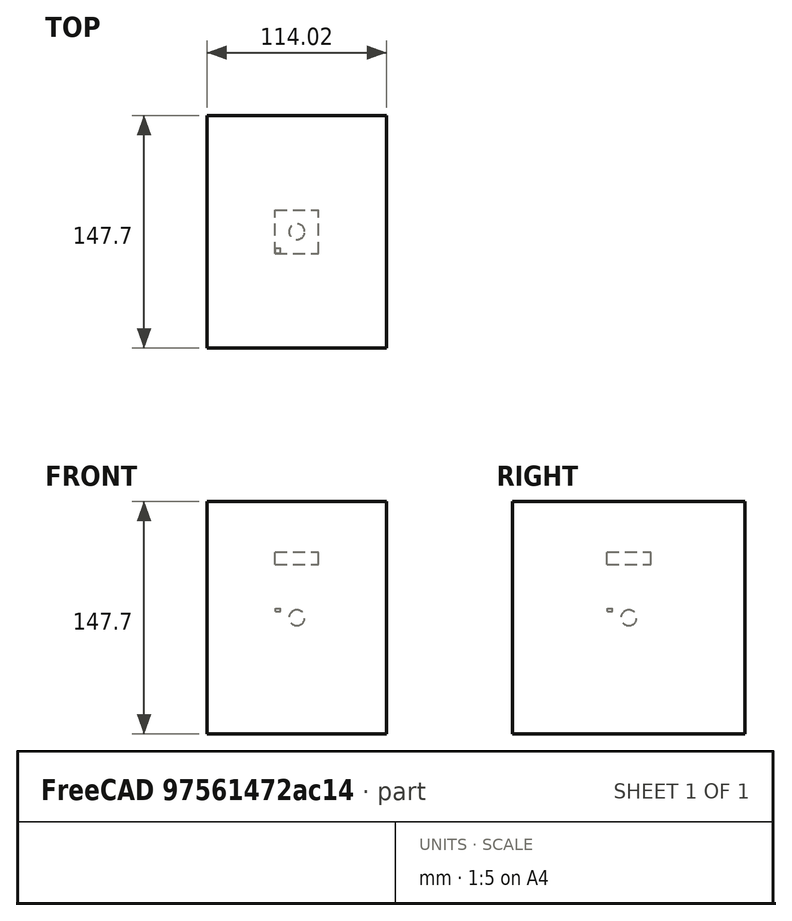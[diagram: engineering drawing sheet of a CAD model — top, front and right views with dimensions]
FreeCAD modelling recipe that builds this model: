
FCSTD DOCUMENT  (FreeCAD 1.0R39109 (Git))
Label: NewBS-NoArray-borderTest-1
License: All rights reserved
objects: App::DocumentObjectGroupPython×1272, App::Link×77, App::Part×7, Part::FeaturePython×4, App::FeaturePython×1
note: 4 computed .brp shape members not serialized (recipe doc carries the construction recipe); baked Part::Feature solids carry a one-line shape summary decoded from their .brp

FEATURE [App::DocumentObjectGroupPython] HALFPI  # scripted group (container) (typed FeaturePython)
  name = HALFPI
  value = pi/2.
FEATURE [App::DocumentObjectGroupPython] PI  # scripted group (container) (typed FeaturePython)
  name = PI
  value = 1.*pi
FEATURE [App::DocumentObjectGroupPython] TWOPI  # scripted group (container) (typed FeaturePython)
  name = TWOPI
  value = 2.*pi
FEATURE [App::DocumentObjectGroupPython] Constants  # scripted group (container) (typed FeaturePython)
  Group = -> [HALFPI,PI,TWOPI]
FEATURE [App::DocumentObjectGroupPython] Variables  # scripted group (container) (typed FeaturePython)
FEATURE [App::DocumentObjectGroupPython] Quantities  # scripted group (container) (typed FeaturePython)
FEATURE [App::DocumentObjectGroupPython] Isotopes  # scripted group (container) (typed FeaturePython)
FEATURE [App::DocumentObjectGroupPython] Elements  # scripted group (container) (typed FeaturePython)
FEATURE [App::DocumentObjectGroupPython] G4_AIR  label="G4_AIR : 1.000"  # scripted group (container) (typed FeaturePython)
  n = 1
FEATURE [App::DocumentObjectGroupPython] Air  # scripted group (container) (typed FeaturePython)
  Dunit = mg/cm3
  Dvalue = 1.29
  Group = -> [G4_AIR]
  RINDEX = AirRINDEX
  conduct = 2
  density = 1
  expand = 3
  name = Air
  specific = 4
FEATURE [App::DocumentObjectGroupPython] SY  # scripted group (container) (typed FeaturePython)
  coldim = 1
  values = 100000/MeV
FEATURE [App::DocumentObjectGroupPython] RS  # scripted group (container) (typed FeaturePython)
  coldim = 1
  values = 1
FEATURE [App::DocumentObjectGroupPython] FTC  # scripted group (container) (typed FeaturePython)
  coldim = 1
  values = 21.5*ns
FEATURE [App::DocumentObjectGroupPython] STC  # scripted group (container) (typed FeaturePython)
  coldim = 1
  values = 43.8*ns
FEATURE [App::DocumentObjectGroupPython] RY1  # scripted group (container) (typed FeaturePython)
  coldim = 1
  values = 95
FEATURE [App::DocumentObjectGroupPython] RY2  # scripted group (container) (typed FeaturePython)
  coldim = 1
  values = 5
FEATURE [App::DocumentObjectGroupPython] YR  # scripted group (container) (typed FeaturePython)
  coldim = 1
  values = 0.8
FEATURE [App::DocumentObjectGroupPython] SCINTLAR  # scripted group (container) (typed FeaturePython)
  coldim = 2
  values = <blob: 2358 chars omitted>
FEATURE [App::DocumentObjectGroupPython] RINDEXLAR  # scripted group (container) (typed FeaturePython)
  coldim = 2
  values = <blob: 9384 chars omitted>
FEATURE [App::DocumentObjectGroupPython] ABSLENGTHLAR  # scripted group (container) (typed FeaturePython)
  coldim = 2
  values = 7.74901*eV 10.0*m 7.77525*eV 10.0*m 7.80167*eV 10.0*m 7.82827*eV 10.0*m 7.85506*eV 10.0*m 7.88202*eV 10.0*m 7.90917*eV 10.0*m 7.93651*eV 10.0*m 7.96404*eV 10.0*m 7.99176*eV 10.0*m 8.01968*eV 10.0*m 8.04779*eV 10.0*m 8.07609*eV 10.0*m 8.1046*eV 10.0*m 8.13331*eV 10.0*m 8.16222*eV 10.0*m 8.19134*eV 10.0*m 8.22067*eV 10.0*m 8.25021*eV 10.0*m 8.27996*eV 10.0*m 8.30993*eV 10.0*m 8.34012*eV 10.0*m 8.37052*eV 10.0*m 8.40115*eV 10.0*m 8.432*eV 10.0*m 8.46308*eV 10.0*m 8.4944*eV 10.0*m 8.52594*eV 10.0*m 8.55772*eV 10.0*m 8.58973*eV 10.0*m 8.62199*eV 10.0*m 8.65449*eV 10.0*m 8.68723*eV 10.0*m 8.72023*eV 10.0*m 8.75347*eV 10.0*m 8.78697*eV 10.0*m 8.82073*eV 10.0*m 8.85475*eV 10.0*m 8.88903*eV 10.0*m 8.92358*eV 10.0*m 8.9584*eV 10.0*m 8.99349*eV 10.0*m 9.02885*eV 10.0*m 9.0645*eV 10.0*m 9.10043*eV 10.0*m 9.13664*eV 10.0*m 9.17314*eV 10.0*m 9.20994*eV 10.0*m 9.24703*eV 10.0*m 9.28442*eV 10.0*m 9.32212*eV 10.0*m 9.36012*eV 10.0*m 9.39844*eV 10.0*m 9.43707*eV 10.0*m 9.47602*eV 10.0*m 9.51529*eV 10.0*m 9.55489*eV 10.0*m 9.59481*eV 10.0*m 9.63508*eV 10.0*m 9.67568*eV 10.0*m 9.71663*eV 10.0*m 9.75792*eV 10.0*m 9.79957*eV 10.0*m 9.84158*eV 10.0*m 9.88394*eV 10.0*m 9.92668*eV 10.0*m 9.96978*eV 10.0*m 10.0133*eV 10.0*m 10.0571*eV 10.0*m 10.1014*eV 10.0*m 10.146*eV 10.0*m 10.191*eV 10.0*m 10.2365*eV 10.0*m 10.2823*eV 10.0*m 10.3286*eV 10.0*m 10.3752*eV 10.0*m 10.4223*eV 10.0*m 10.4699*eV 10.0*m 10.5178*eV 10.0*m 10.5662*eV 10.0*m 10.6151*eV 10.0*m 10.6644*eV 10.0*m 10.7142*eV 10.0*m 10.7644*eV 10.0*m 10.8151*eV 10.0*m 10.8663*eV 10.0*m 10.9179*eV 10.0*m 10.9701*eV 10.0*m 11.0228*eV 10.0*m 11.076*eV 10.0*m 11.1296*eV 10.0*m 11.1839*eV 10.0*m 11.2386*eV 10.0*m 11.2939*eV 10.0*m 11.3497*eV 10.0*m 11.4061*eV 10.0*m 11.463*eV 10.0*m 11.5206*eV 10.0*m 11.5787*eV 10.0*m 11.6373*eV 10.0*m
FEATURE [App::DocumentObjectGroupPython] RAYLEIGHLAR  # scripted group (container) (typed FeaturePython)
  coldim = 2
  values = 7.74901*eV 90.0*cm 7.77525*eV 90.0*cm 7.80167*eV 90.0*cm 7.82827*eV 90.0*cm 7.85506*eV 90.0*cm 7.88202*eV 90.0*cm 7.90917*eV 90.0*cm 7.93651*eV 90.0*cm 7.96404*eV 90.0*cm 7.99176*eV 90.0*cm 8.01968*eV 90.0*cm 8.04779*eV 90.0*cm 8.07609*eV 90.0*cm 8.1046*eV 90.0*cm 8.13331*eV 90.0*cm 8.16222*eV 90.0*cm 8.19134*eV 90.0*cm 8.22067*eV 90.0*cm 8.25021*eV 90.0*cm 8.27996*eV 90.0*cm 8.30993*eV 90.0*cm 8.34012*eV 90.0*cm 8.37052*eV 90.0*cm 8.40115*eV 90.0*cm 8.432*eV 90.0*cm 8.46308*eV 90.0*cm 8.4944*eV 90.0*cm 8.52594*eV 90.0*cm 8.55772*eV 90.0*cm 8.58973*eV 90.0*cm 8.62199*eV 90.0*cm 8.65449*eV 90.0*cm 8.68723*eV 90.0*cm 8.72023*eV 90.0*cm 8.75347*eV 90.0*cm 8.78697*eV 90.0*cm 8.82073*eV 90.0*cm 8.85475*eV 90.0*cm 8.88903*eV 90.0*cm 8.92358*eV 90.0*cm 8.9584*eV 90.0*cm 8.99349*eV 90.0*cm 9.02885*eV 90.0*cm 9.0645*eV 90.0*cm 9.10043*eV 90.0*cm 9.13664*eV 90.0*cm 9.17314*eV 90.0*cm 9.20994*eV 90.0*cm 9.24703*eV 90.0*cm 9.28442*eV 90.0*cm 9.32212*eV 90.0*cm 9.36012*eV 90.0*cm 9.39844*eV 90.0*cm 9.43707*eV 90.0*cm 9.47602*eV 90.0*cm 9.51529*eV 90.0*cm 9.55489*eV 90.0*cm 9.59481*eV 90.0*cm 9.63508*eV 90.0*cm 9.67568*eV 90.0*cm 9.71663*eV 90.0*cm 9.75792*eV 90.0*cm 9.79957*eV 90.0*cm 9.84158*eV 90.0*cm 9.88394*eV 90.0*cm 9.92668*eV 90.0*cm 9.96978*eV 90.0*cm 10.0133*eV 90.0*cm 10.0571*eV 90.0*cm 10.1014*eV 90.0*cm 10.146*eV 90.0*cm 10.191*eV 90.0*cm 10.2365*eV 90.0*cm 10.2823*eV 90.0*cm 10.3286*eV 90.0*cm 10.3752*eV 90.0*cm 10.4223*eV 90.0*cm 10.4699*eV 90.0*cm 10.5178*eV 90.0*cm 10.5662*eV 90.0*cm 10.6151*eV 90.0*cm 10.6644*eV 90.0*cm 10.7142*eV 90.0*cm 10.7644*eV 90.0*cm 10.8151*eV 90.0*cm 10.8663*eV 90.0*cm 10.9179*eV 90.0*cm 10.9701*eV 90.0*cm 11.0228*eV 90.0*cm 11.076*eV 90.0*cm 11.1296*eV 90.0*cm 11.1839*eV 90.0*cm 11.2386*eV 90.0*cm 11.2939*eV 90.0*cm 11.3497*eV 90.0*cm 11.4061*eV 90.0*cm 11.463*eV 90.0*cm 11.5206*eV 90.0*cm 11.5787*eV 90.0*cm 11.6373*eV 90.0*cm
FEATURE [App::DocumentObjectGroupPython] REFLECTIVITY  # scripted group (container) (typed FeaturePython)
  coldim = 2
  values = 2.034*eV 0.98 2.068*eV 0.98 2.103*eV 0.98 2.139*eV 0.98 2.177*eV 0.98 2.216*eV 0.98 2.256*eV 0.98 2.298*eV 0.98 2.341*eV 0.98 2.386*eV 0.98 2.433*eV 0.98 2.481*eV 0.98 2.532*eV 0.98 2.585*eV 0.98 2.64*eV 0.98 2.697*eV 0.98 2.757*eV 0.98 2.82*eV 0.98 2.885*eV 0.98 2.954*eV 0.98 3.026*eV 0.98 3.102*eV 0.98 3.181*eV 0.98 3.265*eV 0.98 3.353*eV 0.98 3.446*eV 0.98 3.545*eV 0.98 3.649*eV 0.98 3.76*eV 0.98 3.877*eV 0.98 4.002*eV 0.98 4.136*eV 0.98 5.0*eV 0.98 6.0*eV 0.98 7.0*eV 0.98 8.0*eV 0.98 9.0*eV 0.98 9.0*eV 0.98 10.0*eV 0.98 11.0*eV 0.98 11.6*eV 0.98
FEATURE [App::DocumentObjectGroupPython] EFFICIENCY  # scripted group (container) (typed FeaturePython)
  coldim = 2
  values = 2.034*eV 1 2.068*eV 1 2.103*eV 1 2.139*eV 1 2.177*eV 1 2.216*eV 1 2.256*eV 1 2.298*eV 1 2.341*eV 1 2.386*eV 1 2.433*eV 1 2.481*eV 1 2.532*eV 1 2.585*eV 1 2.64*eV 1 2.697*eV 1 2.757*eV 1 2.82*eV 1 2.885*eV 1 2.954*eV 1 3.026*eV 1 3.102*eV 1 3.181*eV  1 3.265*eV 1 3.353*eV 1 3.446*eV 1 3.545*eV 1 3.649*eV 1 3.76*eV 1 3.877*eV 1 4.002*eV 1 4.136*eV 1 5.0*eV 1 6.0*eV 1 7.0*eV 1 8.0*eV 1 9.0*eV 1 9.0*eV 1 10.0*eV 1 11.0*eV 1 11.6*eV 1
FEATURE [App::DocumentObjectGroupPython] AirRINDEX  # scripted group (container) (typed FeaturePython)
  coldim = 2
  values = 2.034*eV 1 2.068*eV 1 2.103*eV 1 2.139*eV 1 2.177*eV 1 2.216*eV 1 2.256*eV 1 2.298*eV 1 2.341*eV 1 2.386*eV 1 2.433*eV 1 2.481*eV 1 2.532*eV 1 2.585*eV 1 2.64*eV 1 2.697*eV 1 2.757*eV 1 2.82*eV 1 2.885*eV 1 2.954*eV 1 3.026*eV 1 3.102*eV 1 3.181*eV 1 3.265*eV 1 3.353*eV 1 3.446*eV 1 3.545*eV 1 3.649*eV 1 3.76*eV 1 3.877*eV 1 4.002*eV 1 4.136*eV 1 5.0*eV 1 6.0*eV 1 7.0*eV 1 8.0*eV 1 9.0*eV 1 10.0*eV 1 11.0*eV 1 11.6*eV 1
FEATURE [App::DocumentObjectGroupPython] Matrix  # scripted group (container) (typed FeaturePython)
  Group = -> [SY,RS,FTC,STC,RY1,RY2,YR,SCINTLAR,RINDEXLAR,ABSLENGTHLAR,RAYLEIGHLAR,REFLECTIVITY,EFFICIENCY,AirRINDEX]
FEATURE [App::DocumentObjectGroupPython] ScintWrap  # scripted group (container) (typed FeaturePython)
  EFFICIENCY = EFFICIENCY
  REFLECTIVITY = REFLECTIVITY
  finish = 39
  model = 0
  type = 2
  value = 1
FEATURE [App::DocumentObjectGroupPython] Surfaces  # scripted group (container) (typed FeaturePython)
  Group = -> [ScintWrap]
FEATURE [App::DocumentObjectGroupPython] Opticals  # scripted group (container) (typed FeaturePython)
  Group = -> [Matrix,Surfaces]
FEATURE [App::DocumentObjectGroupPython] G4Isotopes  # scripted group (container) (typed FeaturePython)
FEATURE [App::DocumentObjectGroupPython] H_element  # scripted group (container) (typed FeaturePython)
  Z = 1
  atom_value = 1.008
  formula = H
  name = H_element
FEATURE [App::DocumentObjectGroupPython] He_element  # scripted group (container) (typed FeaturePython)
  Z = 2
  atom_value = 4.0026
  formula = He
  name = He_element
FEATURE [App::DocumentObjectGroupPython] Li_element  # scripted group (container) (typed FeaturePython)
  Z = 3
  atom_value = 6.94
  formula = Li
  name = Li_element
FEATURE [App::DocumentObjectGroupPython] Be_element  # scripted group (container) (typed FeaturePython)
  Z = 4
  atom_value = 9.01218
  formula = Be
  name = Be_element
FEATURE [App::DocumentObjectGroupPython] B_element  # scripted group (container) (typed FeaturePython)
  Z = 5
  atom_value = 10.81
  formula = B
  name = B_element
FEATURE [App::DocumentObjectGroupPython] C_element  # scripted group (container) (typed FeaturePython)
  Z = 6
  atom_value = 12.011
  formula = C
  name = C_element
FEATURE [App::DocumentObjectGroupPython] N_element  # scripted group (container) (typed FeaturePython)
  Z = 7
  atom_value = 14.007
  formula = N
  name = N_element
FEATURE [App::DocumentObjectGroupPython] O_element  # scripted group (container) (typed FeaturePython)
  Z = 8
  atom_value = 15.999
  formula = O
  name = O_element
FEATURE [App::DocumentObjectGroupPython] F_element  # scripted group (container) (typed FeaturePython)
  Z = 9
  atom_value = 18.9984
  formula = F
  name = F_element
FEATURE [App::DocumentObjectGroupPython] Ne_element  # scripted group (container) (typed FeaturePython)
  Z = 10
  atom_value = 20.1797
  formula = Ne
  name = Ne_element
FEATURE [App::DocumentObjectGroupPython] Na_element  # scripted group (container) (typed FeaturePython)
  Z = 11
  atom_value = 22.9898
  formula = Na
  name = Na_element
FEATURE [App::DocumentObjectGroupPython] Mg_element  # scripted group (container) (typed FeaturePython)
  Z = 12
  atom_value = 24.305
  formula = Mg
  name = Mg_element
FEATURE [App::DocumentObjectGroupPython] Al_element  # scripted group (container) (typed FeaturePython)
  Z = 13
  atom_value = 26.9815
  formula = Al
  name = Al_element
FEATURE [App::DocumentObjectGroupPython] Si_element  # scripted group (container) (typed FeaturePython)
  Z = 14
  atom_value = 28.085
  formula = Si
  name = Si_element
FEATURE [App::DocumentObjectGroupPython] P_element  # scripted group (container) (typed FeaturePython)
  Z = 15
  atom_value = 30.9738
  formula = P
  name = P_element
FEATURE [App::DocumentObjectGroupPython] S_element  # scripted group (container) (typed FeaturePython)
  Z = 16
  atom_value = 32.06
  formula = S
  name = S_element
FEATURE [App::DocumentObjectGroupPython] Cl_element  # scripted group (container) (typed FeaturePython)
  Z = 17
  atom_value = 35.45
  formula = Cl
  name = Cl_element
FEATURE [App::DocumentObjectGroupPython] Ar_element  # scripted group (container) (typed FeaturePython)
  Z = 18
  atom_value = 39.95
  formula = Ar
  name = Ar_element
FEATURE [App::DocumentObjectGroupPython] K_element  # scripted group (container) (typed FeaturePython)
  Z = 19
  atom_value = 39.0983
  formula = K
  name = K_element
FEATURE [App::DocumentObjectGroupPython] Ca_element  # scripted group (container) (typed FeaturePython)
  Z = 20
  atom_value = 40.078
  formula = Ca
  name = Ca_element
FEATURE [App::DocumentObjectGroupPython] Sc_element  # scripted group (container) (typed FeaturePython)
  Z = 21
  atom_value = 44.9559
  formula = Sc
  name = Sc_element
FEATURE [App::DocumentObjectGroupPython] Ti_element  # scripted group (container) (typed FeaturePython)
  Z = 22
  atom_value = 47.867
  formula = Ti
  name = Ti_element
FEATURE [App::DocumentObjectGroupPython] V_element  # scripted group (container) (typed FeaturePython)
  Z = 23
  atom_value = 50.9415
  formula = V
  name = V_element
FEATURE [App::DocumentObjectGroupPython] Cr_element  # scripted group (container) (typed FeaturePython)
  Z = 24
  atom_value = 51.9961
  formula = Cr
  name = Cr_element
FEATURE [App::DocumentObjectGroupPython] Mn_element  # scripted group (container) (typed FeaturePython)
  Z = 25
  atom_value = 54.938
  formula = Mn
  name = Mn_element
FEATURE [App::DocumentObjectGroupPython] Fe_element  # scripted group (container) (typed FeaturePython)
  Z = 26
  atom_value = 55.845
  formula = Fe
  name = Fe_element
FEATURE [App::DocumentObjectGroupPython] Co_element  # scripted group (container) (typed FeaturePython)
  Z = 27
  atom_value = 58.9332
  formula = Co
  name = Co_element
FEATURE [App::DocumentObjectGroupPython] Ni_element  # scripted group (container) (typed FeaturePython)
  Z = 28
  atom_value = 58.6934
  formula = Ni
  name = Ni_element
FEATURE [App::DocumentObjectGroupPython] Cu_element  # scripted group (container) (typed FeaturePython)
  Z = 29
  atom_value = 63.546
  formula = Cu
  name = Cu_element
FEATURE [App::DocumentObjectGroupPython] Zn_element  # scripted group (container) (typed FeaturePython)
  Z = 30
  atom_value = 65.38
  formula = Zn
  name = Zn_element
FEATURE [App::DocumentObjectGroupPython] Ga_element  # scripted group (container) (typed FeaturePython)
  Z = 31
  atom_value = 69.723
  formula = Ga
  name = Ga_element
FEATURE [App::DocumentObjectGroupPython] Ge_element  # scripted group (container) (typed FeaturePython)
  Z = 32
  atom_value = 72.63
  formula = Ge
  name = Ge_element
FEATURE [App::DocumentObjectGroupPython] As_element  # scripted group (container) (typed FeaturePython)
  Z = 33
  atom_value = 74.9216
  formula = As
  name = As_element
FEATURE [App::DocumentObjectGroupPython] Se_element  # scripted group (container) (typed FeaturePython)
  Z = 34
  atom_value = 78.971
  formula = Se
  name = Se_element
FEATURE [App::DocumentObjectGroupPython] Br_element  # scripted group (container) (typed FeaturePython)
  Z = 35
  atom_value = 79.904
  formula = Br
  name = Br_element
FEATURE [App::DocumentObjectGroupPython] Kr_element  # scripted group (container) (typed FeaturePython)
  Z = 36
  atom_value = 83.798
  formula = Kr
  name = Kr_element
FEATURE [App::DocumentObjectGroupPython] Rb_element  # scripted group (container) (typed FeaturePython)
  Z = 37
  atom_value = 85.4678
  formula = Rb
  name = Rb_element
FEATURE [App::DocumentObjectGroupPython] Sr_element  # scripted group (container) (typed FeaturePython)
  Z = 38
  atom_value = 87.62
  formula = Sr
  name = Sr_element
FEATURE [App::DocumentObjectGroupPython] Y_element  # scripted group (container) (typed FeaturePython)
  Z = 39
  atom_value = 88.9058
  formula = Y
  name = Y_element
FEATURE [App::DocumentObjectGroupPython] Zr_element  # scripted group (container) (typed FeaturePython)
  Z = 40
  atom_value = 91.224
  formula = Zr
  name = Zr_element
FEATURE [App::DocumentObjectGroupPython] Nb_element  # scripted group (container) (typed FeaturePython)
  Z = 41
  atom_value = 92.9064
  formula = Nb
  name = Nb_element
FEATURE [App::DocumentObjectGroupPython] Mo_element  # scripted group (container) (typed FeaturePython)
  Z = 42
  atom_value = 95.95
  formula = Mo
  name = Mo_element
FEATURE [App::DocumentObjectGroupPython] Tc_element  # scripted group (container) (typed FeaturePython)
  Z = 43
  atom_value = 97
  formula = Tc
  name = Tc_element
FEATURE [App::DocumentObjectGroupPython] Ru_element  # scripted group (container) (typed FeaturePython)
  Z = 44
  atom_value = 101.07
  formula = Ru
  name = Ru_element
FEATURE [App::DocumentObjectGroupPython] Rh_element  # scripted group (container) (typed FeaturePython)
  Z = 45
  atom_value = 102.905
  formula = Rh
  name = Rh_element
FEATURE [App::DocumentObjectGroupPython] Pd_element  # scripted group (container) (typed FeaturePython)
  Z = 46
  atom_value = 106.42
  formula = Pd
  name = Pd_element
FEATURE [App::DocumentObjectGroupPython] Ag_element  # scripted group (container) (typed FeaturePython)
  Z = 47
  atom_value = 107.868
  formula = Ag
  name = Ag_element
FEATURE [App::DocumentObjectGroupPython] Cd_element  # scripted group (container) (typed FeaturePython)
  Z = 48
  atom_value = 112.414
  formula = Cd
  name = Cd_element
FEATURE [App::DocumentObjectGroupPython] In_element  # scripted group (container) (typed FeaturePython)
  Z = 49
  atom_value = 114.818
  formula = In
  name = In_element
FEATURE [App::DocumentObjectGroupPython] Sn_element  # scripted group (container) (typed FeaturePython)
  Z = 50
  atom_value = 118.71
  formula = Sn
  name = Sn_element
FEATURE [App::DocumentObjectGroupPython] Sb_element  # scripted group (container) (typed FeaturePython)
  Z = 51
  atom_value = 121.76
  formula = Sb
  name = Sb_element
FEATURE [App::DocumentObjectGroupPython] Te_element  # scripted group (container) (typed FeaturePython)
  Z = 52
  atom_value = 127.6
  formula = Te
  name = Te_element
FEATURE [App::DocumentObjectGroupPython] I_element  # scripted group (container) (typed FeaturePython)
  Z = 53
  atom_value = 126.904
  formula = I
  name = I_element
FEATURE [App::DocumentObjectGroupPython] Xe_element  # scripted group (container) (typed FeaturePython)
  Z = 54
  atom_value = 131.293
  formula = Xe
  name = Xe_element
FEATURE [App::DocumentObjectGroupPython] Cs_element  # scripted group (container) (typed FeaturePython)
  Z = 55
  atom_value = 132.905
  formula = Cs
  name = Cs_element
FEATURE [App::DocumentObjectGroupPython] Ba_element  # scripted group (container) (typed FeaturePython)
  Z = 56
  atom_value = 137.327
  formula = Ba
  name = Ba_element
FEATURE [App::DocumentObjectGroupPython] La_element  # scripted group (container) (typed FeaturePython)
  Z = 57
  atom_value = 138.905
  formula = La
  name = La_element
FEATURE [App::DocumentObjectGroupPython] Ce_element  # scripted group (container) (typed FeaturePython)
  Z = 58
  atom_value = 140.116
  formula = Ce
  name = Ce_element
FEATURE [App::DocumentObjectGroupPython] Pr_element  # scripted group (container) (typed FeaturePython)
  Z = 59
  atom_value = 140.908
  formula = Pr
  name = Pr_element
FEATURE [App::DocumentObjectGroupPython] Nd_element  # scripted group (container) (typed FeaturePython)
  Z = 60
  atom_value = 144.242
  formula = Nd
  name = Nd_element
FEATURE [App::DocumentObjectGroupPython] Pm_element  # scripted group (container) (typed FeaturePython)
  Z = 61
  atom_value = 145
  formula = Pm
  name = Pm_element
FEATURE [App::DocumentObjectGroupPython] Sm_element  # scripted group (container) (typed FeaturePython)
  Z = 62
  atom_value = 150.36
  formula = Sm
  name = Sm_element
FEATURE [App::DocumentObjectGroupPython] Eu_element  # scripted group (container) (typed FeaturePython)
  Z = 63
  atom_value = 151.964
  formula = Eu
  name = Eu_element
FEATURE [App::DocumentObjectGroupPython] Gd_element  # scripted group (container) (typed FeaturePython)
  Z = 64
  atom_value = 157.25
  formula = Gd
  name = Gd_element
FEATURE [App::DocumentObjectGroupPython] Tb_element  # scripted group (container) (typed FeaturePython)
  Z = 65
  atom_value = 158.925
  formula = Tb
  name = Tb_element
FEATURE [App::DocumentObjectGroupPython] Dy_element  # scripted group (container) (typed FeaturePython)
  Z = 66
  atom_value = 162.5
  formula = Dy
  name = Dy_element
FEATURE [App::DocumentObjectGroupPython] Ho_element  # scripted group (container) (typed FeaturePython)
  Z = 67
  atom_value = 164.93
  formula = Ho
  name = Ho_element
FEATURE [App::DocumentObjectGroupPython] Er_element  # scripted group (container) (typed FeaturePython)
  Z = 68
  atom_value = 167.259
  formula = Er
  name = Er_element
FEATURE [App::DocumentObjectGroupPython] Tm_element  # scripted group (container) (typed FeaturePython)
  Z = 69
  atom_value = 168.934
  formula = Tm
  name = Tm_element
FEATURE [App::DocumentObjectGroupPython] Yb_element  # scripted group (container) (typed FeaturePython)
  Z = 70
  atom_value = 173.045
  formula = Yb
  name = Yb_element
FEATURE [App::DocumentObjectGroupPython] Lu_element  # scripted group (container) (typed FeaturePython)
  Z = 71
  atom_value = 174.967
  formula = Lu
  name = Lu_element
FEATURE [App::DocumentObjectGroupPython] Hf_element  # scripted group (container) (typed FeaturePython)
  Z = 72
  atom_value = 178.49
  formula = Hf
  name = Hf_element
FEATURE [App::DocumentObjectGroupPython] Ta_element  # scripted group (container) (typed FeaturePython)
  Z = 73
  atom_value = 180.948
  formula = Ta
  name = Ta_element
FEATURE [App::DocumentObjectGroupPython] W_element  # scripted group (container) (typed FeaturePython)
  Z = 74
  atom_value = 183.84
  formula = W
  name = W_element
FEATURE [App::DocumentObjectGroupPython] Re_element  # scripted group (container) (typed FeaturePython)
  Z = 75
  atom_value = 186.207
  formula = Re
  name = Re_element
FEATURE [App::DocumentObjectGroupPython] Os_element  # scripted group (container) (typed FeaturePython)
  Z = 76
  atom_value = 190.23
  formula = Os
  name = Os_element
FEATURE [App::DocumentObjectGroupPython] Ir_element  # scripted group (container) (typed FeaturePython)
  Z = 77
  atom_value = 192.217
  formula = Ir
  name = Ir_element
FEATURE [App::DocumentObjectGroupPython] Pt_element  # scripted group (container) (typed FeaturePython)
  Z = 78
  atom_value = 195.084
  formula = Pt
  name = Pt_element
FEATURE [App::DocumentObjectGroupPython] Au_element  # scripted group (container) (typed FeaturePython)
  Z = 79
  atom_value = 196.967
  formula = Au
  name = Au_element
FEATURE [App::DocumentObjectGroupPython] Hg_element  # scripted group (container) (typed FeaturePython)
  Z = 80
  atom_value = 200.592
  formula = Hg
  name = Hg_element
FEATURE [App::DocumentObjectGroupPython] Tl_element  # scripted group (container) (typed FeaturePython)
  Z = 81
  atom_value = 204.38
  formula = Tl
  name = Tl_element
FEATURE [App::DocumentObjectGroupPython] Pb_element  # scripted group (container) (typed FeaturePython)
  Z = 82
  atom_value = 207.2
  formula = Pb
  name = Pb_element
FEATURE [App::DocumentObjectGroupPython] Bi_element  # scripted group (container) (typed FeaturePython)
  Z = 83
  atom_value = 208.98
  formula = Bi
  name = Bi_element
FEATURE [App::DocumentObjectGroupPython] Po_element  # scripted group (container) (typed FeaturePython)
  Z = 84
  atom_value = 209
  formula = Po
  name = Po_element
FEATURE [App::DocumentObjectGroupPython] At_element  # scripted group (container) (typed FeaturePython)
  Z = 85
  atom_value = 210
  formula = At
  name = At_element
FEATURE [App::DocumentObjectGroupPython] Rn_element  # scripted group (container) (typed FeaturePython)
  Z = 86
  atom_value = 222
  formula = Rn
  name = Rn_element
FEATURE [App::DocumentObjectGroupPython] Fr_element  # scripted group (container) (typed FeaturePython)
  Z = 87
  atom_value = 223
  formula = Fr
  name = Fr_element
FEATURE [App::DocumentObjectGroupPython] Ra_element  # scripted group (container) (typed FeaturePython)
  Z = 88
  atom_value = 226
  formula = Ra
  name = Ra_element
FEATURE [App::DocumentObjectGroupPython] Ac_element  # scripted group (container) (typed FeaturePython)
  Z = 89
  atom_value = 227
  formula = Ac
  name = Ac_element
FEATURE [App::DocumentObjectGroupPython] Th_element  # scripted group (container) (typed FeaturePython)
  Z = 90
  atom_value = 232.038
  formula = Th
  name = Th_element
FEATURE [App::DocumentObjectGroupPython] Pa_element  # scripted group (container) (typed FeaturePython)
  Z = 91
  atom_value = 231.036
  formula = Pa
  name = Pa_element
FEATURE [App::DocumentObjectGroupPython] U_element  # scripted group (container) (typed FeaturePython)
  Z = 92
  atom_value = 238.029
  formula = U
  name = U_element
FEATURE [App::DocumentObjectGroupPython] Np_element  # scripted group (container) (typed FeaturePython)
  Z = 93
  atom_value = 237
  formula = Np
  name = Np_element
FEATURE [App::DocumentObjectGroupPython] Pu_element  # scripted group (container) (typed FeaturePython)
  Z = 94
  atom_value = 244
  formula = Pu
  name = Pu_element
FEATURE [App::DocumentObjectGroupPython] Am_element  # scripted group (container) (typed FeaturePython)
  Z = 95
  atom_value = 243
  formula = Am
  name = Am_element
FEATURE [App::DocumentObjectGroupPython] Cm_element  # scripted group (container) (typed FeaturePython)
  Z = 96
  atom_value = 247
  formula = Cm
  name = Cm_element
FEATURE [App::DocumentObjectGroupPython] Bk_element  # scripted group (container) (typed FeaturePython)
  Z = 97
  atom_value = 247
  formula = Bk
  name = Bk_element
FEATURE [App::DocumentObjectGroupPython] Cf_element  # scripted group (container) (typed FeaturePython)
  Z = 98
  atom_value = 251
  formula = Cf
  name = Cf_element
FEATURE [App::DocumentObjectGroupPython] G4Elements  # scripted group (container) (typed FeaturePython)
  Group = -> [H_element,He_element,Li_element,Be_element,B_element,C_element,N_element,O_element,F_element,Ne_element,Na_element,Mg_element,Al_element,Si_element,P_element,S_element,Cl_element,Ar_element,K_element,Ca_element,Sc_element,Ti_element,V_element,Cr_element,Mn_element,Fe_element,Co_element,Ni_element,Cu_element,Zn_element,Ga_element,Ge_element,As_element,Se_element,Br_element,Kr_element,Rb_element,+61 more]
FEATURE [App::DocumentObjectGroupPython] H_element001  label="H_element : 0.101"  # scripted group (container) (typed FeaturePython)
  n = 0.101327
FEATURE [App::DocumentObjectGroupPython] C_element001  label="C_element : 0.775"  # scripted group (container) (typed FeaturePython)
  n = 0.7755
FEATURE [App::DocumentObjectGroupPython] N_element001  label="N_element : 0.035"  # scripted group (container) (typed FeaturePython)
  n = 0.035057
FEATURE [App::DocumentObjectGroupPython] O_element001  label="O_element : 0.052"  # scripted group (container) (typed FeaturePython)
  n = 0.0523159
FEATURE [App::DocumentObjectGroupPython] F_element001  label="F_element : 0.017"  # scripted group (container) (typed FeaturePython)
  n = 0.017422
FEATURE [App::DocumentObjectGroupPython] Ca_element001  label="Ca_element : 0.018"  # scripted group (container) (typed FeaturePython)
  n = 0.018378
FEATURE [App::DocumentObjectGroupPython] G4_A_150_TISSUE  label="G4_A-150_TISSUE"  # scripted group (container) (typed FeaturePython)
  Dunit = g/cm3
  Dvalue = 1.127
  Group = -> [H_element001,C_element001,N_element001,O_element001,F_element001,Ca_element001]
  conduct = 2
  density = 1
  expand = 3
  formula = G4_A-150_TISSUE
  name = G4_A-150_TISSUE
  specific = 4
FEATURE [App::DocumentObjectGroupPython] C_element002  label="C_element : 3"  # scripted group (container) (typed FeaturePython)
  n = 3
  ref = C_element
FEATURE [App::DocumentObjectGroupPython] H_element002  label="H_element : 6"  # scripted group (container) (typed FeaturePython)
  n = 6
  ref = H_element
FEATURE [App::DocumentObjectGroupPython] O_element002  label="O_element : 1"  # scripted group (container) (typed FeaturePython)
  n = 1
  ref = O_element
FEATURE [App::DocumentObjectGroupPython] G4_ACETONE  # scripted group (container) (typed FeaturePython)
  Dunit = g/cm3
  Dvalue = 0.7899
  Group = -> [C_element002,H_element002,O_element002]
  conduct = 2
  density = 1
  expand = 3
  formula = G4_ACETONE
  name = G4_ACETONE
  specific = 4
FEATURE [App::DocumentObjectGroupPython] C_element003  label="C_element : 2"  # scripted group (container) (typed FeaturePython)
  n = 2
  ref = C_element
FEATURE [App::DocumentObjectGroupPython] H_element003  label="H_element : 2"  # scripted group (container) (typed FeaturePython)
  n = 2
  ref = H_element
FEATURE [App::DocumentObjectGroupPython] G4_ACETYLENE  # scripted group (container) (typed FeaturePython)
  Dunit = g/cm3
  Dvalue = 0.0010967
  Group = -> [C_element003,H_element003]
  conduct = 2
  density = 1
  expand = 3
  formula = G4_ACETYLENE
  name = G4_ACETYLENE
  specific = 4
FEATURE [App::DocumentObjectGroupPython] C_element004  label="C_element : 5"  # scripted group (container) (typed FeaturePython)
  n = 5
  ref = C_element
FEATURE [App::DocumentObjectGroupPython] H_element004  label="H_element : 5"  # scripted group (container) (typed FeaturePython)
  n = 5
  ref = H_element
FEATURE [App::DocumentObjectGroupPython] N_element002  label="N_element : 5"  # scripted group (container) (typed FeaturePython)
  n = 5
  ref = N_element
FEATURE [App::DocumentObjectGroupPython] G4_ADENINE  # scripted group (container) (typed FeaturePython)
  Dunit = g/cm3
  Dvalue = 1.6
  Group = -> [C_element004,H_element004,N_element002]
  conduct = 2
  density = 1
  expand = 3
  formula = G4_ADENINE
  name = G4_ADENINE
  specific = 4
FEATURE [App::DocumentObjectGroupPython] H_element005  label="H_element : 0.114"  # scripted group (container) (typed FeaturePython)
  n = 0.114
FEATURE [App::DocumentObjectGroupPython] C_element005  label="C_element : 0.598"  # scripted group (container) (typed FeaturePython)
  n = 0.598
FEATURE [App::DocumentObjectGroupPython] N_element003  label="N_element : 0.007"  # scripted group (container) (typed FeaturePython)
  n = 0.007
FEATURE [App::DocumentObjectGroupPython] O_element003  label="O_element : 0.278"  # scripted group (container) (typed FeaturePython)
  n = 0.278
FEATURE [App::DocumentObjectGroupPython] Na_element001  label="Na_element : 0.001"  # scripted group (container) (typed FeaturePython)
  n = 0.001
FEATURE [App::DocumentObjectGroupPython] S_element001  label="S_element : 0.001"  # scripted group (container) (typed FeaturePython)
  n = 0.001
FEATURE [App::DocumentObjectGroupPython] Cl_element001  label="Cl_element : 0.001"  # scripted group (container) (typed FeaturePython)
  n = 0.001
FEATURE [App::DocumentObjectGroupPython] G4_ADIPOSE_TISSUE_ICRP  # scripted group (container) (typed FeaturePython)
  Dunit = g/cm3
  Dvalue = 0.95
  Group = -> [H_element005,C_element005,N_element003,O_element003,Na_element001,S_element001,Cl_element001]
  conduct = 2
  density = 1
  expand = 3
  formula = G4_ADIPOSE_TISSUE_ICRP
  name = G4_ADIPOSE_TISSUE_ICRP
  specific = 4
FEATURE [App::DocumentObjectGroupPython] C_element006  label="C_element : 0.000"  # scripted group (container) (typed FeaturePython)
  n = 0.000124
FEATURE [App::DocumentObjectGroupPython] N_element004  label="N_element : 0.755"  # scripted group (container) (typed FeaturePython)
  n = 0.755268
FEATURE [App::DocumentObjectGroupPython] O_element004  label="O_element : 0.232"  # scripted group (container) (typed FeaturePython)
  n = 0.231781
FEATURE [App::DocumentObjectGroupPython] Ar_element001  label="Ar_element : 0.013"  # scripted group (container) (typed FeaturePython)
  n = 0.012827
FEATURE [App::DocumentObjectGroupPython] G4_AIR001  label="G4_AIR"  # scripted group (container) (typed FeaturePython)
  Dunit = g/cm3
  Dvalue = 0.00120479
  Group = -> [C_element006,N_element004,O_element004,Ar_element001]
  conduct = 2
  density = 1
  expand = 3
  formula = G4_AIR
  name = G4_AIR
  specific = 4
FEATURE [App::DocumentObjectGroupPython] C_element007  label="C_element : 006"  # scripted group (container) (typed FeaturePython)
  n = 3
  ref = C_element
FEATURE [App::DocumentObjectGroupPython] H_element006  label="H_element : 7"  # scripted group (container) (typed FeaturePython)
  n = 7
  ref = H_element
FEATURE [App::DocumentObjectGroupPython] N_element005  label="N_element : 1"  # scripted group (container) (typed FeaturePython)
  n = 1
  ref = N_element
FEATURE [App::DocumentObjectGroupPython] O_element005  label="O_element : 2"  # scripted group (container) (typed FeaturePython)
  n = 2
  ref = O_element
FEATURE [App::DocumentObjectGroupPython] G4_ALANINE  # scripted group (container) (typed FeaturePython)
  Dunit = g/cm3
  Dvalue = 1.42
  Group = -> [C_element007,H_element006,N_element005,O_element005]
  conduct = 2
  density = 1
  expand = 3
  formula = G4_ALANINE
  name = G4_ALANINE
  specific = 4
FEATURE [App::DocumentObjectGroupPython] Al_element001  label="Al_element : 2"  # scripted group (container) (typed FeaturePython)
  n = 2
  ref = Al_element
FEATURE [App::DocumentObjectGroupPython] O_element006  label="O_element : 3"  # scripted group (container) (typed FeaturePython)
  n = 3
  ref = O_element
FEATURE [App::DocumentObjectGroupPython] G4_ALUMINUM_OXIDE  # scripted group (container) (typed FeaturePython)
  Dunit = g/cm3
  Dvalue = 3.97
  Group = -> [Al_element001,O_element006]
  conduct = 2
  density = 1
  expand = 3
  formula = G4_ALUMINUM_OXIDE
  name = G4_ALUMINUM_OXIDE
  specific = 4
FEATURE [App::DocumentObjectGroupPython] H_element007  label="H_element : 0.106"  # scripted group (container) (typed FeaturePython)
  n = 0.10593
FEATURE [App::DocumentObjectGroupPython] C_element008  label="C_element : 0.789"  # scripted group (container) (typed FeaturePython)
  n = 0.788974
FEATURE [App::DocumentObjectGroupPython] O_element007  label="O_element : 0.105"  # scripted group (container) (typed FeaturePython)
  n = 0.105096
FEATURE [App::DocumentObjectGroupPython] G4_AMBER  # scripted group (container) (typed FeaturePython)
  Dunit = g/cm3
  Dvalue = 1.1
  Group = -> [H_element007,C_element008,O_element007]
  conduct = 2
  density = 1
  expand = 3
  formula = G4_AMBER
  name = G4_AMBER
  specific = 4
FEATURE [App::DocumentObjectGroupPython] N_element006  label="N_element : 006"  # scripted group (container) (typed FeaturePython)
  n = 1
  ref = N_element
FEATURE [App::DocumentObjectGroupPython] H_element008  label="H_element : 3"  # scripted group (container) (typed FeaturePython)
  n = 3
  ref = H_element
FEATURE [App::DocumentObjectGroupPython] G4_AMMONIA  # scripted group (container) (typed FeaturePython)
  Dunit = g/cm3
  Dvalue = 0.000826019
  Group = -> [N_element006,H_element008]
  conduct = 2
  density = 1
  expand = 3
  formula = G4_AMMONIA
  name = G4_AMMONIA
  specific = 4
FEATURE [App::DocumentObjectGroupPython] C_element009  label="C_element : 6"  # scripted group (container) (typed FeaturePython)
  n = 6
  ref = C_element
FEATURE [App::DocumentObjectGroupPython] H_element009  label="H_element : 008"  # scripted group (container) (typed FeaturePython)
  n = 7
  ref = H_element
FEATURE [App::DocumentObjectGroupPython] N_element007  label="N_element : 007"  # scripted group (container) (typed FeaturePython)
  n = 1
  ref = N_element
FEATURE [App::DocumentObjectGroupPython] G4_ANILINE  # scripted group (container) (typed FeaturePython)
  Dunit = g/cm3
  Dvalue = 1.0235
  Group = -> [C_element009,H_element009,N_element007]
  conduct = 2
  density = 1
  expand = 3
  formula = G4_ANILINE
  name = G4_ANILINE
  specific = 4
FEATURE [App::DocumentObjectGroupPython] C_element010  label="C_element : 14"  # scripted group (container) (typed FeaturePython)
  n = 14
  ref = C_element
FEATURE [App::DocumentObjectGroupPython] H_element010  label="H_element : 10"  # scripted group (container) (typed FeaturePython)
  n = 10
  ref = H_element
FEATURE [App::DocumentObjectGroupPython] G4_ANTHRACENE  # scripted group (container) (typed FeaturePython)
  Dunit = g/cm3
  Dvalue = 1.283
  Group = -> [C_element010,H_element010]
  conduct = 2
  density = 1
  expand = 3
  formula = G4_ANTHRACENE
  name = G4_ANTHRACENE
  specific = 4
FEATURE [App::DocumentObjectGroupPython] H_element011  label="H_element : 0.065"  # scripted group (container) (typed FeaturePython)
  n = 0.0654709
FEATURE [App::DocumentObjectGroupPython] C_element011  label="C_element : 0.537"  # scripted group (container) (typed FeaturePython)
  n = 0.536944
FEATURE [App::DocumentObjectGroupPython] N_element008  label="N_element : 0.021"  # scripted group (container) (typed FeaturePython)
  n = 0.0215
FEATURE [App::DocumentObjectGroupPython] O_element008  label="O_element : 0.032"  # scripted group (container) (typed FeaturePython)
  n = 0.032085
FEATURE [App::DocumentObjectGroupPython] F_element002  label="F_element : 0.167"  # scripted group (container) (typed FeaturePython)
  n = 0.167411
FEATURE [App::DocumentObjectGroupPython] Ca_element002  label="Ca_element : 0.177"  # scripted group (container) (typed FeaturePython)
  n = 0.176589
FEATURE [App::DocumentObjectGroupPython] G4_B_100_BONE  label="G4_B-100_BONE"  # scripted group (container) (typed FeaturePython)
  Dunit = g/cm3
  Dvalue = 1.45
  Group = -> [H_element011,C_element011,N_element008,O_element008,F_element002,Ca_element002]
  conduct = 2
  density = 1
  expand = 3
  formula = G4_B-100_BONE
  name = G4_B-100_BONE
  specific = 4
FEATURE [App::DocumentObjectGroupPython] H_element012  label="H_element : 0.057"  # scripted group (container) (typed FeaturePython)
  n = 0.057441
FEATURE [App::DocumentObjectGroupPython] C_element012  label="C_element : 0.790"  # scripted group (container) (typed FeaturePython)
  n = 0.774591
FEATURE [App::DocumentObjectGroupPython] O_element009  label="O_element : 0.168"  # scripted group (container) (typed FeaturePython)
  n = 0.167968
FEATURE [App::DocumentObjectGroupPython] G4_BAKELITE  # scripted group (container) (typed FeaturePython)
  Dunit = g/cm3
  Dvalue = 1.25
  Group = -> [H_element012,C_element012,O_element009]
  conduct = 2
  density = 1
  expand = 3
  formula = G4_BAKELITE
  name = G4_BAKELITE
  specific = 4
FEATURE [App::DocumentObjectGroupPython] Ba_element001  label="Ba_element : 1"  # scripted group (container) (typed FeaturePython)
  n = 1
  ref = Ba_element
FEATURE [App::DocumentObjectGroupPython] F_element003  label="F_element : 2"  # scripted group (container) (typed FeaturePython)
  n = 2
  ref = F_element
FEATURE [App::DocumentObjectGroupPython] G4_BARIUM_FLUORIDE  # scripted group (container) (typed FeaturePython)
  Dunit = g/cm3
  Dvalue = 4.89
  Group = -> [Ba_element001,F_element003]
  conduct = 2
  density = 1
  expand = 3
  formula = G4_BARIUM_FLUORIDE
  name = G4_BARIUM_FLUORIDE
  specific = 4
FEATURE [App::DocumentObjectGroupPython] Ba_element002  label="Ba_element : 002"  # scripted group (container) (typed FeaturePython)
  n = 1
  ref = Ba_element
FEATURE [App::DocumentObjectGroupPython] S_element002  label="S_element : 1"  # scripted group (container) (typed FeaturePython)
  n = 1
  ref = S_element
FEATURE [App::DocumentObjectGroupPython] O_element010  label="O_element : 4"  # scripted group (container) (typed FeaturePython)
  n = 4
  ref = O_element
FEATURE [App::DocumentObjectGroupPython] G4_BARIUM_SULFATE  # scripted group (container) (typed FeaturePython)
  Dunit = g/cm3
  Dvalue = 4.5
  Group = -> [Ba_element002,S_element002,O_element010]
  conduct = 2
  density = 1
  expand = 3
  formula = G4_BARIUM_SULFATE
  name = G4_BARIUM_SULFATE
  specific = 4
FEATURE [App::DocumentObjectGroupPython] C_element013  label="C_element : 007"  # scripted group (container) (typed FeaturePython)
  n = 6
  ref = C_element
FEATURE [App::DocumentObjectGroupPython] H_element013  label="H_element : 009"  # scripted group (container) (typed FeaturePython)
  n = 6
  ref = H_element
FEATURE [App::DocumentObjectGroupPython] G4_BENZENE  # scripted group (container) (typed FeaturePython)
  Dunit = g/cm3
  Dvalue = 0.87865
  Group = -> [C_element013,H_element013]
  conduct = 2
  density = 1
  expand = 3
  formula = G4_BENZENE
  name = G4_BENZENE
  specific = 4
FEATURE [App::DocumentObjectGroupPython] Be_element001  label="Be_element : 1"  # scripted group (container) (typed FeaturePython)
  n = 1
  ref = Be_element
FEATURE [App::DocumentObjectGroupPython] O_element011  label="O_element : 005"  # scripted group (container) (typed FeaturePython)
  n = 1
  ref = O_element
FEATURE [App::DocumentObjectGroupPython] G4_BERYLLIUM_OXIDE  # scripted group (container) (typed FeaturePython)
  Dunit = g/cm3
  Dvalue = 3.01
  Group = -> [Be_element001,O_element011]
  conduct = 2
  density = 1
  expand = 3
  formula = G4_BERYLLIUM_OXIDE
  name = G4_BERYLLIUM_OXIDE
  specific = 4
FEATURE [App::DocumentObjectGroupPython] Bi_element001  label="Bi_element : 4"  # scripted group (container) (typed FeaturePython)
  n = 4
  ref = Bi_element
FEATURE [App::DocumentObjectGroupPython] Ge_element001  label="Ge_element : 3"  # scripted group (container) (typed FeaturePython)
  n = 3
  ref = Ge_element
FEATURE [App::DocumentObjectGroupPython] O_element012  label="O_element : 12"  # scripted group (container) (typed FeaturePython)
  n = 12
  ref = O_element
FEATURE [App::DocumentObjectGroupPython] G4_BGO  # scripted group (container) (typed FeaturePython)
  Dunit = g/cm3
  Dvalue = 7.13
  Group = -> [Bi_element001,Ge_element001,O_element012]
  conduct = 2
  density = 1
  expand = 3
  formula = G4_BGO
  name = G4_BGO
  specific = 4
FEATURE [App::DocumentObjectGroupPython] H_element014  label="H_element : 0.102"  # scripted group (container) (typed FeaturePython)
  n = 0.102
FEATURE [App::DocumentObjectGroupPython] C_element014  label="C_element : 0.110"  # scripted group (container) (typed FeaturePython)
  n = 0.11
FEATURE [App::DocumentObjectGroupPython] N_element009  label="N_element : 0.033"  # scripted group (container) (typed FeaturePython)
  n = 0.033
FEATURE [App::DocumentObjectGroupPython] O_element013  label="O_element : 0.745"  # scripted group (container) (typed FeaturePython)
  n = 0.745
FEATURE [App::DocumentObjectGroupPython] Na_element002  label="Na_element : 0.002"  # scripted group (container) (typed FeaturePython)
  n = 0.001
FEATURE [App::DocumentObjectGroupPython] P_element001  label="P_element : 0.001"  # scripted group (container) (typed FeaturePython)
  n = 0.001
FEATURE [App::DocumentObjectGroupPython] S_element003  label="S_element : 0.002"  # scripted group (container) (typed FeaturePython)
  n = 0.002
FEATURE [App::DocumentObjectGroupPython] Cl_element002  label="Cl_element : 0.003"  # scripted group (container) (typed FeaturePython)
  n = 0.003
FEATURE [App::DocumentObjectGroupPython] K_element001  label="K_element : 0.002"  # scripted group (container) (typed FeaturePython)
  n = 0.002
FEATURE [App::DocumentObjectGroupPython] Fe_element001  label="Fe_element : 0.001"  # scripted group (container) (typed FeaturePython)
  n = 0.001
FEATURE [App::DocumentObjectGroupPython] G4_BLOOD_ICRP  # scripted group (container) (typed FeaturePython)
  Dunit = g/cm3
  Dvalue = 1.06
  Group = -> [H_element014,C_element014,N_element009,O_element013,Na_element002,P_element001,S_element003,Cl_element002,K_element001,Fe_element001]
  conduct = 2
  density = 1
  expand = 3
  formula = G4_BLOOD_ICRP
  name = G4_BLOOD_ICRP
  specific = 4
FEATURE [App::DocumentObjectGroupPython] H_element015  label="H_element : 0.064"  # scripted group (container) (typed FeaturePython)
  n = 0.064
FEATURE [App::DocumentObjectGroupPython] C_element015  label="C_element : 0.278"  # scripted group (container) (typed FeaturePython)
  n = 0.278
FEATURE [App::DocumentObjectGroupPython] N_element010  label="N_element : 0.027"  # scripted group (container) (typed FeaturePython)
  n = 0.027
FEATURE [App::DocumentObjectGroupPython] O_element014  label="O_element : 0.410"  # scripted group (container) (typed FeaturePython)
  n = 0.41
FEATURE [App::DocumentObjectGroupPython] Mg_element001  label="Mg_element : 0.002"  # scripted group (container) (typed FeaturePython)
  n = 0.002
FEATURE [App::DocumentObjectGroupPython] P_element002  label="P_element : 0.070"  # scripted group (container) (typed FeaturePython)
  n = 0.07
FEATURE [App::DocumentObjectGroupPython] S_element004  label="S_element : 0.003"  # scripted group (container) (typed FeaturePython)
  n = 0.002
FEATURE [App::DocumentObjectGroupPython] Ca_element003  label="Ca_element : 0.147"  # scripted group (container) (typed FeaturePython)
  n = 0.147
FEATURE [App::DocumentObjectGroupPython] G4_BONE_COMPACT_ICRU  # scripted group (container) (typed FeaturePython)
  Dunit = g/cm3
  Dvalue = 1.85
  Group = -> [H_element015,C_element015,N_element010,O_element014,Mg_element001,P_element002,S_element004,Ca_element003]
  conduct = 2
  density = 1
  expand = 3
  formula = G4_BONE_COMPACT_ICRU
  name = G4_BONE_COMPACT_ICRU
  specific = 4
FEATURE [App::DocumentObjectGroupPython] H_element016  label="H_element : 0.034"  # scripted group (container) (typed FeaturePython)
  n = 0.034
FEATURE [App::DocumentObjectGroupPython] C_element016  label="C_element : 0.155"  # scripted group (container) (typed FeaturePython)
  n = 0.155
FEATURE [App::DocumentObjectGroupPython] N_element011  label="N_element : 0.042"  # scripted group (container) (typed FeaturePython)
  n = 0.042
FEATURE [App::DocumentObjectGroupPython] O_element015  label="O_element : 0.435"  # scripted group (container) (typed FeaturePython)
  n = 0.435
FEATURE [App::DocumentObjectGroupPython] Na_element003  label="Na_element : 0.003"  # scripted group (container) (typed FeaturePython)
  n = 0.001
FEATURE [App::DocumentObjectGroupPython] Mg_element002  label="Mg_element : 0.003"  # scripted group (container) (typed FeaturePython)
  n = 0.002
FEATURE [App::DocumentObjectGroupPython] P_element003  label="P_element : 0.103"  # scripted group (container) (typed FeaturePython)
  n = 0.103
FEATURE [App::DocumentObjectGroupPython] S_element005  label="S_element : 0.004"  # scripted group (container) (typed FeaturePython)
  n = 0.003
FEATURE [App::DocumentObjectGroupPython] Ca_element004  label="Ca_element : 0.225"  # scripted group (container) (typed FeaturePython)
  n = 0.225
FEATURE [App::DocumentObjectGroupPython] G4_BONE_CORTICAL_ICRP  # scripted group (container) (typed FeaturePython)
  Dunit = g/cm3
  Dvalue = 1.92
  Group = -> [H_element016,C_element016,N_element011,O_element015,Na_element003,Mg_element002,P_element003,S_element005,Ca_element004]
  conduct = 2
  density = 1
  expand = 3
  formula = G4_BONE_CORTICAL_ICRP
  name = G4_BONE_CORTICAL_ICRP
  specific = 4
FEATURE [App::DocumentObjectGroupPython] B_element001  label="B_element : 4"  # scripted group (container) (typed FeaturePython)
  n = 4
  ref = B_element
FEATURE [App::DocumentObjectGroupPython] C_element017  label="C_element : 1"  # scripted group (container) (typed FeaturePython)
  n = 1
  ref = C_element
FEATURE [App::DocumentObjectGroupPython] G4_BORON_CARBIDE  # scripted group (container) (typed FeaturePython)
  Dunit = g/cm3
  Dvalue = 2.52
  Group = -> [B_element001,C_element017]
  conduct = 2
  density = 1
  expand = 3
  formula = G4_BORON_CARBIDE
  name = G4_BORON_CARBIDE
  specific = 4
FEATURE [App::DocumentObjectGroupPython] B_element002  label="B_element : 2"  # scripted group (container) (typed FeaturePython)
  n = 2
  ref = B_element
FEATURE [App::DocumentObjectGroupPython] O_element016  label="O_element : 006"  # scripted group (container) (typed FeaturePython)
  n = 3
  ref = O_element
FEATURE [App::DocumentObjectGroupPython] G4_BORON_OXIDE  # scripted group (container) (typed FeaturePython)
  Dunit = g/cm3
  Dvalue = 1.812
  Group = -> [B_element002,O_element016]
  conduct = 2
  density = 1
  expand = 3
  formula = G4_BORON_OXIDE
  name = G4_BORON_OXIDE
  specific = 4
FEATURE [App::DocumentObjectGroupPython] H_element017  label="H_element : 0.107"  # scripted group (container) (typed FeaturePython)
  n = 0.107
FEATURE [App::DocumentObjectGroupPython] C_element018  label="C_element : 0.145"  # scripted group (container) (typed FeaturePython)
  n = 0.145
FEATURE [App::DocumentObjectGroupPython] N_element012  label="N_element : 0.022"  # scripted group (container) (typed FeaturePython)
  n = 0.022
FEATURE [App::DocumentObjectGroupPython] O_element017  label="O_element : 0.712"  # scripted group (container) (typed FeaturePython)
  n = 0.712
FEATURE [App::DocumentObjectGroupPython] Na_element004  label="Na_element : 0.004"  # scripted group (container) (typed FeaturePython)
  n = 0.002
FEATURE [App::DocumentObjectGroupPython] P_element004  label="P_element : 0.004"  # scripted group (container) (typed FeaturePython)
  n = 0.004
FEATURE [App::DocumentObjectGroupPython] S_element006  label="S_element : 0.005"  # scripted group (container) (typed FeaturePython)
  n = 0.002
FEATURE [App::DocumentObjectGroupPython] Cl_element003  label="Cl_element : 0.004"  # scripted group (container) (typed FeaturePython)
  n = 0.003
FEATURE [App::DocumentObjectGroupPython] K_element002  label="K_element : 0.003"  # scripted group (container) (typed FeaturePython)
  n = 0.003
FEATURE [App::DocumentObjectGroupPython] G4_BRAIN_ICRP  # scripted group (container) (typed FeaturePython)
  Dunit = g/cm3
  Dvalue = 1.04
  Group = -> [H_element017,C_element018,N_element012,O_element017,Na_element004,P_element004,S_element006,Cl_element003,K_element002]
  conduct = 2
  density = 1
  expand = 3
  formula = G4_BRAIN_ICRP
  name = G4_BRAIN_ICRP
  specific = 4
FEATURE [App::DocumentObjectGroupPython] C_element019  label="C_element : 4"  # scripted group (container) (typed FeaturePython)
  n = 4
  ref = C_element
FEATURE [App::DocumentObjectGroupPython] H_element018  label="H_element : 010"  # scripted group (container) (typed FeaturePython)
  n = 10
  ref = H_element
FEATURE [App::DocumentObjectGroupPython] G4_BUTANE  # scripted group (container) (typed FeaturePython)
  Dunit = g/cm3
  Dvalue = 0.00249343
  Group = -> [C_element019,H_element018]
  conduct = 2
  density = 1
  expand = 3
  formula = G4_BUTANE
  name = G4_BUTANE
  specific = 4
FEATURE [App::DocumentObjectGroupPython] C_element020  label="C_element : 008"  # scripted group (container) (typed FeaturePython)
  n = 4
  ref = C_element
FEATURE [App::DocumentObjectGroupPython] H_element019  label="H_element : 011"  # scripted group (container) (typed FeaturePython)
  n = 10
  ref = H_element
FEATURE [App::DocumentObjectGroupPython] O_element018  label="O_element : 007"  # scripted group (container) (typed FeaturePython)
  n = 1
  ref = O_element
FEATURE [App::DocumentObjectGroupPython] G4_N_BUTYL_ALCOHOL  label="G4_N-BUTYL_ALCOHOL"  # scripted group (container) (typed FeaturePython)
  Dunit = g/cm3
  Dvalue = 0.8098
  Group = -> [C_element020,H_element019,O_element018]
  conduct = 2
  density = 1
  expand = 3
  formula = G4_N-BUTYL_ALCOHOL
  name = G4_N-BUTYL_ALCOHOL
  specific = 4
FEATURE [App::DocumentObjectGroupPython] H_element020  label="H_element : 0.025"  # scripted group (container) (typed FeaturePython)
  n = 0.02468
FEATURE [App::DocumentObjectGroupPython] C_element021  label="C_element : 0.502"  # scripted group (container) (typed FeaturePython)
  n = 0.501611
FEATURE [App::DocumentObjectGroupPython] O_element019  label="O_element : 0.005"  # scripted group (container) (typed FeaturePython)
  n = 0.004527
FEATURE [App::DocumentObjectGroupPython] F_element004  label="F_element : 0.465"  # scripted group (container) (typed FeaturePython)
  n = 0.465209
FEATURE [App::DocumentObjectGroupPython] Si_element001  label="Si_element : 0.004"  # scripted group (container) (typed FeaturePython)
  n = 0.003973
FEATURE [App::DocumentObjectGroupPython] G4_C_552  label="G4_C-552"  # scripted group (container) (typed FeaturePython)
  Dunit = g/cm3
  Dvalue = 1.76
  Group = -> [H_element020,C_element021,O_element019,F_element004,Si_element001]
  conduct = 2
  density = 1
  expand = 3
  formula = G4_C-552
  name = G4_C-552
  specific = 4
FEATURE [App::DocumentObjectGroupPython] Cd_element001  label="Cd_element : 1"  # scripted group (container) (typed FeaturePython)
  n = 1
  ref = Cd_element
FEATURE [App::DocumentObjectGroupPython] Te_element001  label="Te_element : 1"  # scripted group (container) (typed FeaturePython)
  n = 1
  ref = Te_element
FEATURE [App::DocumentObjectGroupPython] G4_CADMIUM_TELLURIDE  # scripted group (container) (typed FeaturePython)
  Dunit = g/cm3
  Dvalue = 6.2
  Group = -> [Cd_element001,Te_element001]
  conduct = 2
  density = 1
  expand = 3
  formula = G4_CADMIUM_TELLURIDE
  name = G4_CADMIUM_TELLURIDE
  specific = 4
FEATURE [App::DocumentObjectGroupPython] Cd_element002  label="Cd_element : 002"  # scripted group (container) (typed FeaturePython)
  n = 1
  ref = Cd_element
FEATURE [App::DocumentObjectGroupPython] W_element001  label="W_element : 1"  # scripted group (container) (typed FeaturePython)
  n = 1
  ref = W_element
FEATURE [App::DocumentObjectGroupPython] O_element020  label="O_element : 008"  # scripted group (container) (typed FeaturePython)
  n = 4
  ref = O_element
FEATURE [App::DocumentObjectGroupPython] G4_CADMIUM_TUNGSTATE  # scripted group (container) (typed FeaturePython)
  Dunit = g/cm3
  Dvalue = 7.9
  Group = -> [Cd_element002,W_element001,O_element020]
  conduct = 2
  density = 1
  expand = 3
  formula = G4_CADMIUM_TUNGSTATE
  name = G4_CADMIUM_TUNGSTATE
  specific = 4
FEATURE [App::DocumentObjectGroupPython] Ca_element005  label="Ca_element : 1"  # scripted group (container) (typed FeaturePython)
  n = 1
  ref = Ca_element
FEATURE [App::DocumentObjectGroupPython] C_element022  label="C_element : 009"  # scripted group (container) (typed FeaturePython)
  n = 1
  ref = C_element
FEATURE [App::DocumentObjectGroupPython] O_element021  label="O_element : 009"  # scripted group (container) (typed FeaturePython)
  n = 3
  ref = O_element
FEATURE [App::DocumentObjectGroupPython] G4_CALCIUM_CARBONATE  # scripted group (container) (typed FeaturePython)
  Dunit = g/cm3
  Dvalue = 2.8
  Group = -> [Ca_element005,C_element022,O_element021]
  conduct = 2
  density = 1
  expand = 3
  formula = G4_CALCIUM_CARBONATE
  name = G4_CALCIUM_CARBONATE
  specific = 4
FEATURE [App::DocumentObjectGroupPython] Ca_element006  label="Ca_element : 002"  # scripted group (container) (typed FeaturePython)
  n = 1
  ref = Ca_element
FEATURE [App::DocumentObjectGroupPython] F_element005  label="F_element : 003"  # scripted group (container) (typed FeaturePython)
  n = 2
  ref = F_element
FEATURE [App::DocumentObjectGroupPython] G4_CALCIUM_FLUORIDE  # scripted group (container) (typed FeaturePython)
  Dunit = g/cm3
  Dvalue = 3.18
  Group = -> [Ca_element006,F_element005]
  conduct = 2
  density = 1
  expand = 3
  formula = G4_CALCIUM_FLUORIDE
  name = G4_CALCIUM_FLUORIDE
  specific = 4
FEATURE [App::DocumentObjectGroupPython] Ca_element007  label="Ca_element : 003"  # scripted group (container) (typed FeaturePython)
  n = 1
  ref = Ca_element
FEATURE [App::DocumentObjectGroupPython] O_element022  label="O_element : 010"  # scripted group (container) (typed FeaturePython)
  n = 1
  ref = O_element
FEATURE [App::DocumentObjectGroupPython] G4_CALCIUM_OXIDE  # scripted group (container) (typed FeaturePython)
  Dunit = g/cm3
  Dvalue = 3.3
  Group = -> [Ca_element007,O_element022]
  conduct = 2
  density = 1
  expand = 3
  formula = G4_CALCIUM_OXIDE
  name = G4_CALCIUM_OXIDE
  specific = 4
FEATURE [App::DocumentObjectGroupPython] Ca_element008  label="Ca_element : 004"  # scripted group (container) (typed FeaturePython)
  n = 1
  ref = Ca_element
FEATURE [App::DocumentObjectGroupPython] S_element007  label="S_element : 002"  # scripted group (container) (typed FeaturePython)
  n = 1
  ref = S_element
FEATURE [App::DocumentObjectGroupPython] O_element023  label="O_element : 011"  # scripted group (container) (typed FeaturePython)
  n = 4
  ref = O_element
FEATURE [App::DocumentObjectGroupPython] G4_CALCIUM_SULFATE  # scripted group (container) (typed FeaturePython)
  Dunit = g/cm3
  Dvalue = 2.96
  Group = -> [Ca_element008,S_element007,O_element023]
  conduct = 2
  density = 1
  expand = 3
  formula = G4_CALCIUM_SULFATE
  name = G4_CALCIUM_SULFATE
  specific = 4
FEATURE [App::DocumentObjectGroupPython] Ca_element009  label="Ca_element : 005"  # scripted group (container) (typed FeaturePython)
  n = 1
  ref = Ca_element
FEATURE [App::DocumentObjectGroupPython] W_element002  label="W_element : 002"  # scripted group (container) (typed FeaturePython)
  n = 1
  ref = W_element
FEATURE [App::DocumentObjectGroupPython] O_element024  label="O_element : 012"  # scripted group (container) (typed FeaturePython)
  n = 4
  ref = O_element
FEATURE [App::DocumentObjectGroupPython] G4_CALCIUM_TUNGSTATE  # scripted group (container) (typed FeaturePython)
  Dunit = g/cm3
  Dvalue = 6.062
  Group = -> [Ca_element009,W_element002,O_element024]
  conduct = 2
  density = 1
  expand = 3
  formula = G4_CALCIUM_TUNGSTATE
  name = G4_CALCIUM_TUNGSTATE
  specific = 4
FEATURE [App::DocumentObjectGroupPython] C_element023  label="C_element : 010"  # scripted group (container) (typed FeaturePython)
  n = 1
  ref = C_element
FEATURE [App::DocumentObjectGroupPython] O_element025  label="O_element : 013"  # scripted group (container) (typed FeaturePython)
  n = 2
  ref = O_element
FEATURE [App::DocumentObjectGroupPython] G4_CARBON_DIOXIDE  # scripted group (container) (typed FeaturePython)
  Dunit = g/cm3
  Dvalue = 0.00184212
  Group = -> [C_element023,O_element025]
  conduct = 2
  density = 1
  expand = 3
  formula = G4_CARBON_DIOXIDE
  name = G4_CARBON_DIOXIDE
  specific = 4
FEATURE [App::DocumentObjectGroupPython] C_element024  label="C_element : 011"  # scripted group (container) (typed FeaturePython)
  n = 1
  ref = C_element
FEATURE [App::DocumentObjectGroupPython] Cl_element004  label="Cl_element : 4"  # scripted group (container) (typed FeaturePython)
  n = 4
  ref = Cl_element
FEATURE [App::DocumentObjectGroupPython] G4_CARBON_TETRACHLORIDE  # scripted group (container) (typed FeaturePython)
  Dunit = g/cm3
  Dvalue = 1.594
  Group = -> [C_element024,Cl_element004]
  conduct = 2
  density = 1
  expand = 3
  formula = G4_CARBON_TETRACHLORIDE
  name = G4_CARBON_TETRACHLORIDE
  specific = 4
FEATURE [App::DocumentObjectGroupPython] C_element025  label="C_element : 012"  # scripted group (container) (typed FeaturePython)
  n = 6
  ref = C_element
FEATURE [App::DocumentObjectGroupPython] H_element021  label="H_element : 012"  # scripted group (container) (typed FeaturePython)
  n = 10
  ref = H_element
FEATURE [App::DocumentObjectGroupPython] O_element026  label="O_element : 5"  # scripted group (container) (typed FeaturePython)
  n = 5
  ref = O_element
FEATURE [App::DocumentObjectGroupPython] G4_CELLULOSE_CELLOPHANE  # scripted group (container) (typed FeaturePython)
  Dunit = g/cm3
  Dvalue = 1.42
  Group = -> [C_element025,H_element021,O_element026]
  conduct = 2
  density = 1
  expand = 3
  formula = G4_CELLULOSE_CELLOPHANE
  name = G4_CELLULOSE_CELLOPHANE
  specific = 4
FEATURE [App::DocumentObjectGroupPython] H_element022  label="H_element : 0.067"  # scripted group (container) (typed FeaturePython)
  n = 0.067125
FEATURE [App::DocumentObjectGroupPython] C_element026  label="C_element : 0.545"  # scripted group (container) (typed FeaturePython)
  n = 0.545403
FEATURE [App::DocumentObjectGroupPython] O_element027  label="O_element : 0.387"  # scripted group (container) (typed FeaturePython)
  n = 0.387472
FEATURE [App::DocumentObjectGroupPython] G4_CELLULOSE_BUTYRATE  # scripted group (container) (typed FeaturePython)
  Dunit = g/cm3
  Dvalue = 1.2
  Group = -> [H_element022,C_element026,O_element027]
  conduct = 2
  density = 1
  expand = 3
  formula = G4_CELLULOSE_BUTYRATE
  name = G4_CELLULOSE_BUTYRATE
  specific = 4
FEATURE [App::DocumentObjectGroupPython] H_element023  label="H_element : 0.029"  # scripted group (container) (typed FeaturePython)
  n = 0.029216
FEATURE [App::DocumentObjectGroupPython] C_element027  label="C_element : 0.271"  # scripted group (container) (typed FeaturePython)
  n = 0.271296
FEATURE [App::DocumentObjectGroupPython] N_element013  label="N_element : 0.121"  # scripted group (container) (typed FeaturePython)
  n = 0.121276
FEATURE [App::DocumentObjectGroupPython] O_element028  label="O_element : 0.578"  # scripted group (container) (typed FeaturePython)
  n = 0.578212
FEATURE [App::DocumentObjectGroupPython] G4_CELLULOSE_NITRATE  # scripted group (container) (typed FeaturePython)
  Dunit = g/cm3
  Dvalue = 1.49
  Group = -> [H_element023,C_element027,N_element013,O_element028]
  conduct = 2
  density = 1
  expand = 3
  formula = G4_CELLULOSE_NITRATE
  name = G4_CELLULOSE_NITRATE
  specific = 4
FEATURE [App::DocumentObjectGroupPython] H_element024  label="H_element : 0.108"  # scripted group (container) (typed FeaturePython)
  n = 0.107596
FEATURE [App::DocumentObjectGroupPython] N_element014  label="N_element : 0.001"  # scripted group (container) (typed FeaturePython)
  n = 0.0008
FEATURE [App::DocumentObjectGroupPython] O_element029  label="O_element : 0.875"  # scripted group (container) (typed FeaturePython)
  n = 0.874976
FEATURE [App::DocumentObjectGroupPython] S_element008  label="S_element : 0.015"  # scripted group (container) (typed FeaturePython)
  n = 0.014627
FEATURE [App::DocumentObjectGroupPython] Ce_element001  label="Ce_element : 0.002"  # scripted group (container) (typed FeaturePython)
  n = 0.002001
FEATURE [App::DocumentObjectGroupPython] G4_CERIC_SULFATE  # scripted group (container) (typed FeaturePython)
  Dunit = g/cm3
  Dvalue = 1.03
  Group = -> [H_element024,N_element014,O_element029,S_element008,Ce_element001]
  conduct = 2
  density = 1
  expand = 3
  formula = G4_CERIC_SULFATE
  name = G4_CERIC_SULFATE
  specific = 4
FEATURE [App::DocumentObjectGroupPython] Cs_element001  label="Cs_element : 1"  # scripted group (container) (typed FeaturePython)
  n = 1
  ref = Cs_element
FEATURE [App::DocumentObjectGroupPython] F_element006  label="F_element : 1"  # scripted group (container) (typed FeaturePython)
  n = 1
  ref = F_element
FEATURE [App::DocumentObjectGroupPython] G4_CESIUM_FLUORIDE  # scripted group (container) (typed FeaturePython)
  Dunit = g/cm3
  Dvalue = 4.115
  Group = -> [Cs_element001,F_element006]
  conduct = 2
  density = 1
  expand = 3
  formula = G4_CESIUM_FLUORIDE
  name = G4_CESIUM_FLUORIDE
  specific = 4
FEATURE [App::DocumentObjectGroupPython] Cs_element002  label="Cs_element : 002"  # scripted group (container) (typed FeaturePython)
  n = 1
  ref = Cs_element
FEATURE [App::DocumentObjectGroupPython] I_element001  label="I_element : 1"  # scripted group (container) (typed FeaturePython)
  n = 1
  ref = I_element
FEATURE [App::DocumentObjectGroupPython] G4_CESIUM_IODIDE001  label="G4_CESIUM_IODIDE"  # scripted group (container) (typed FeaturePython)
  Dunit = g/cm3
  Dvalue = 4.51
  Group = -> [Cs_element002,I_element001]
  conduct = 2
  density = 1
  expand = 3
  formula = G4_CESIUM_IODIDE
  name = G4_CESIUM_IODIDE
  specific = 4
FEATURE [App::DocumentObjectGroupPython] C_element028  label="C_element : 013"  # scripted group (container) (typed FeaturePython)
  n = 6
  ref = C_element
FEATURE [App::DocumentObjectGroupPython] H_element025  label="H_element : 013"  # scripted group (container) (typed FeaturePython)
  n = 5
  ref = H_element
FEATURE [App::DocumentObjectGroupPython] Cl_element005  label="Cl_element : 1"  # scripted group (container) (typed FeaturePython)
  n = 1
  ref = Cl_element
FEATURE [App::DocumentObjectGroupPython] G4_CHLOROBENZENE  # scripted group (container) (typed FeaturePython)
  Dunit = g/cm3
  Dvalue = 1.1058
  Group = -> [C_element028,H_element025,Cl_element005]
  conduct = 2
  density = 1
  expand = 3
  formula = G4_CHLOROBENZENE
  name = G4_CHLOROBENZENE
  specific = 4
FEATURE [App::DocumentObjectGroupPython] C_element029  label="C_element : 014"  # scripted group (container) (typed FeaturePython)
  n = 1
  ref = C_element
FEATURE [App::DocumentObjectGroupPython] H_element026  label="H_element : 1"  # scripted group (container) (typed FeaturePython)
  n = 1
  ref = H_element
FEATURE [App::DocumentObjectGroupPython] Cl_element006  label="Cl_element : 3"  # scripted group (container) (typed FeaturePython)
  n = 3
  ref = Cl_element
FEATURE [App::DocumentObjectGroupPython] G4_CHLOROFORM  # scripted group (container) (typed FeaturePython)
  Dunit = g/cm3
  Dvalue = 1.4832
  Group = -> [C_element029,H_element026,Cl_element006]
  conduct = 2
  density = 1
  expand = 3
  formula = G4_CHLOROFORM
  name = G4_CHLOROFORM
  specific = 4
FEATURE [App::DocumentObjectGroupPython] H_element027  label="H_element : 0.010"  # scripted group (container) (typed FeaturePython)
  n = 0.01
FEATURE [App::DocumentObjectGroupPython] C_element030  label="C_element : 0.001"  # scripted group (container) (typed FeaturePython)
  n = 0.001
FEATURE [App::DocumentObjectGroupPython] O_element030  label="O_element : 0.529"  # scripted group (container) (typed FeaturePython)
  n = 0.529107
FEATURE [App::DocumentObjectGroupPython] Na_element005  label="Na_element : 0.016"  # scripted group (container) (typed FeaturePython)
  n = 0.016
FEATURE [App::DocumentObjectGroupPython] Mg_element003  label="Mg_element : 0.004"  # scripted group (container) (typed FeaturePython)
  n = 0.002
FEATURE [App::DocumentObjectGroupPython] Al_element002  label="Al_element : 0.034"  # scripted group (container) (typed FeaturePython)
  n = 0.033872
FEATURE [App::DocumentObjectGroupPython] Si_element002  label="Si_element : 0.337"  # scripted group (container) (typed FeaturePython)
  n = 0.337021
FEATURE [App::DocumentObjectGroupPython] K_element003  label="K_element : 0.013"  # scripted group (container) (typed FeaturePython)
  n = 0.013
FEATURE [App::DocumentObjectGroupPython] Ca_element010  label="Ca_element : 0.044"  # scripted group (container) (typed FeaturePython)
  n = 0.044
FEATURE [App::DocumentObjectGroupPython] Fe_element002  label="Fe_element : 0.014"  # scripted group (container) (typed FeaturePython)
  n = 0.014
FEATURE [App::DocumentObjectGroupPython] G4_CONCRETE  # scripted group (container) (typed FeaturePython)
  Dunit = g/cm3
  Dvalue = 2.3
  Group = -> [H_element027,C_element030,O_element030,Na_element005,Mg_element003,Al_element002,Si_element002,K_element003,Ca_element010,Fe_element002]
  conduct = 2
  density = 1
  expand = 3
  formula = G4_CONCRETE
  name = G4_CONCRETE
  specific = 4
FEATURE [App::DocumentObjectGroupPython] C_element031  label="C_element : 015"  # scripted group (container) (typed FeaturePython)
  n = 6
  ref = C_element
FEATURE [App::DocumentObjectGroupPython] H_element028  label="H_element : 12"  # scripted group (container) (typed FeaturePython)
  n = 12
  ref = H_element
FEATURE [App::DocumentObjectGroupPython] G4_CYCLOHEXANE  # scripted group (container) (typed FeaturePython)
  Dunit = g/cm3
  Dvalue = 0.779
  Group = -> [C_element031,H_element028]
  conduct = 2
  density = 1
  expand = 3
  formula = G4_CYCLOHEXANE
  name = G4_CYCLOHEXANE
  specific = 4
FEATURE [App::DocumentObjectGroupPython] C_element032  label="C_element : 016"  # scripted group (container) (typed FeaturePython)
  n = 6
  ref = C_element
FEATURE [App::DocumentObjectGroupPython] H_element029  label="H_element : 4"  # scripted group (container) (typed FeaturePython)
  n = 4
  ref = H_element
FEATURE [App::DocumentObjectGroupPython] Cl_element007  label="Cl_element : 2"  # scripted group (container) (typed FeaturePython)
  n = 2
  ref = Cl_element
FEATURE [App::DocumentObjectGroupPython] G4_1_2_DICHLOROBENZENE  label="G4_1.2-DICHLOROBENZENE"  # scripted group (container) (typed FeaturePython)
  Dunit = g/cm3
  Dvalue = 1.3048
  Group = -> [C_element032,H_element029,Cl_element007]
  conduct = 2
  density = 1
  expand = 3
  formula = G4_1.2-DICHLOROBENZENE
  name = G4_1.2-DICHLOROBENZENE
  specific = 4
FEATURE [App::DocumentObjectGroupPython] C_element033  label="C_element : 017"  # scripted group (container) (typed FeaturePython)
  n = 4
  ref = C_element
FEATURE [App::DocumentObjectGroupPython] H_element030  label="H_element : 8"  # scripted group (container) (typed FeaturePython)
  n = 8
  ref = H_element
FEATURE [App::DocumentObjectGroupPython] O_element031  label="O_element : 014"  # scripted group (container) (typed FeaturePython)
  n = 1
  ref = O_element
FEATURE [App::DocumentObjectGroupPython] Cl_element008  label="Cl_element : 005"  # scripted group (container) (typed FeaturePython)
  n = 2
  ref = Cl_element
FEATURE [App::DocumentObjectGroupPython] G4_DICHLORODIETHYL_ETHER  # scripted group (container) (typed FeaturePython)
  Dunit = g/cm3
  Dvalue = 1.2199
  Group = -> [C_element033,H_element030,O_element031,Cl_element008]
  conduct = 2
  density = 1
  expand = 3
  formula = G4_DICHLORODIETHYL_ETHER
  name = G4_DICHLORODIETHYL_ETHER
  specific = 4
FEATURE [App::DocumentObjectGroupPython] C_element034  label="C_element : 018"  # scripted group (container) (typed FeaturePython)
  n = 2
  ref = C_element
FEATURE [App::DocumentObjectGroupPython] H_element031  label="H_element : 014"  # scripted group (container) (typed FeaturePython)
  n = 4
  ref = H_element
FEATURE [App::DocumentObjectGroupPython] Cl_element009  label="Cl_element : 006"  # scripted group (container) (typed FeaturePython)
  n = 2
  ref = Cl_element
FEATURE [App::DocumentObjectGroupPython] G4_1_2_DICHLOROETHANE  label="G4_1.2-DICHLOROETHANE"  # scripted group (container) (typed FeaturePython)
  Dunit = g/cm3
  Dvalue = 1.2351
  Group = -> [C_element034,H_element031,Cl_element009]
  conduct = 2
  density = 1
  expand = 3
  formula = G4_1.2-DICHLOROETHANE
  name = G4_1.2-DICHLOROETHANE
  specific = 4
FEATURE [App::DocumentObjectGroupPython] C_element035  label="C_element : 019"  # scripted group (container) (typed FeaturePython)
  n = 4
  ref = C_element
FEATURE [App::DocumentObjectGroupPython] H_element032  label="H_element : 015"  # scripted group (container) (typed FeaturePython)
  n = 10
  ref = H_element
FEATURE [App::DocumentObjectGroupPython] O_element032  label="O_element : 015"  # scripted group (container) (typed FeaturePython)
  n = 1
  ref = O_element
FEATURE [App::DocumentObjectGroupPython] G4_DIETHYL_ETHER  # scripted group (container) (typed FeaturePython)
  Dunit = g/cm3
  Dvalue = 0.71378
  Group = -> [C_element035,H_element032,O_element032]
  conduct = 2
  density = 1
  expand = 3
  formula = G4_DIETHYL_ETHER
  name = G4_DIETHYL_ETHER
  specific = 4
FEATURE [App::DocumentObjectGroupPython] C_element036  label="C_element : 020"  # scripted group (container) (typed FeaturePython)
  n = 3
  ref = C_element
FEATURE [App::DocumentObjectGroupPython] H_element033  label="H_element : 016"  # scripted group (container) (typed FeaturePython)
  n = 7
  ref = H_element
FEATURE [App::DocumentObjectGroupPython] N_element015  label="N_element : 008"  # scripted group (container) (typed FeaturePython)
  n = 1
  ref = N_element
FEATURE [App::DocumentObjectGroupPython] O_element033  label="O_element : 016"  # scripted group (container) (typed FeaturePython)
  n = 1
  ref = O_element
FEATURE [App::DocumentObjectGroupPython] G4_N_N_DIMETHYL_FORMAMIDE  label="G4_N.N-DIMETHYL_FORMAMIDE"  # scripted group (container) (typed FeaturePython)
  Dunit = g/cm3
  Dvalue = 0.9487
  Group = -> [C_element036,H_element033,N_element015,O_element033]
  conduct = 2
  density = 1
  expand = 3
  formula = G4_N.N-DIMETHYL_FORMAMIDE
  name = G4_N.N-DIMETHYL_FORMAMIDE
  specific = 4
FEATURE [App::DocumentObjectGroupPython] C_element037  label="C_element : 021"  # scripted group (container) (typed FeaturePython)
  n = 2
  ref = C_element
FEATURE [App::DocumentObjectGroupPython] H_element034  label="H_element : 017"  # scripted group (container) (typed FeaturePython)
  n = 6
  ref = H_element
FEATURE [App::DocumentObjectGroupPython] O_element034  label="O_element : 017"  # scripted group (container) (typed FeaturePython)
  n = 1
  ref = O_element
FEATURE [App::DocumentObjectGroupPython] S_element009  label="S_element : 003"  # scripted group (container) (typed FeaturePython)
  n = 1
  ref = S_element
FEATURE [App::DocumentObjectGroupPython] G4_DIMETHYL_SULFOXIDE  # scripted group (container) (typed FeaturePython)
  Dunit = g/cm3
  Dvalue = 1.1014
  Group = -> [C_element037,H_element034,O_element034,S_element009]
  conduct = 2
  density = 1
  expand = 3
  formula = G4_DIMETHYL_SULFOXIDE
  name = G4_DIMETHYL_SULFOXIDE
  specific = 4
FEATURE [App::DocumentObjectGroupPython] C_element038  label="C_element : 022"  # scripted group (container) (typed FeaturePython)
  n = 2
  ref = C_element
FEATURE [App::DocumentObjectGroupPython] H_element035  label="H_element : 018"  # scripted group (container) (typed FeaturePython)
  n = 6
  ref = H_element
FEATURE [App::DocumentObjectGroupPython] G4_ETHANE  # scripted group (container) (typed FeaturePython)
  Dunit = g/cm3
  Dvalue = 0.00125324
  Group = -> [C_element038,H_element035]
  conduct = 2
  density = 1
  expand = 3
  formula = G4_ETHANE
  name = G4_ETHANE
  specific = 4
FEATURE [App::DocumentObjectGroupPython] C_element039  label="C_element : 023"  # scripted group (container) (typed FeaturePython)
  n = 2
  ref = C_element
FEATURE [App::DocumentObjectGroupPython] H_element036  label="H_element : 019"  # scripted group (container) (typed FeaturePython)
  n = 6
  ref = H_element
FEATURE [App::DocumentObjectGroupPython] O_element035  label="O_element : 018"  # scripted group (container) (typed FeaturePython)
  n = 1
  ref = O_element
FEATURE [App::DocumentObjectGroupPython] G4_ETHYL_ALCOHOL  # scripted group (container) (typed FeaturePython)
  Dunit = g/cm3
  Dvalue = 0.7893
  Group = -> [C_element039,H_element036,O_element035]
  conduct = 2
  density = 1
  expand = 3
  formula = G4_ETHYL_ALCOHOL
  name = G4_ETHYL_ALCOHOL
  specific = 4
FEATURE [App::DocumentObjectGroupPython] H_element037  label="H_element : 0.090"  # scripted group (container) (typed FeaturePython)
  n = 0.090027
FEATURE [App::DocumentObjectGroupPython] C_element040  label="C_element : 0.585"  # scripted group (container) (typed FeaturePython)
  n = 0.585182
FEATURE [App::DocumentObjectGroupPython] O_element036  label="O_element : 0.325"  # scripted group (container) (typed FeaturePython)
  n = 0.324791
FEATURE [App::DocumentObjectGroupPython] G4_ETHYL_CELLULOSE  # scripted group (container) (typed FeaturePython)
  Dunit = g/cm3
  Dvalue = 1.13
  Group = -> [H_element037,C_element040,O_element036]
  conduct = 2
  density = 1
  expand = 3
  formula = G4_ETHYL_CELLULOSE
  name = G4_ETHYL_CELLULOSE
  specific = 4
FEATURE [App::DocumentObjectGroupPython] C_element041  label="C_element : 024"  # scripted group (container) (typed FeaturePython)
  n = 2
  ref = C_element
FEATURE [App::DocumentObjectGroupPython] H_element038  label="H_element : 020"  # scripted group (container) (typed FeaturePython)
  n = 4
  ref = H_element
FEATURE [App::DocumentObjectGroupPython] G4_ETHYLENE  # scripted group (container) (typed FeaturePython)
  Dunit = g/cm3
  Dvalue = 0.00117497
  Group = -> [C_element041,H_element038]
  conduct = 2
  density = 1
  expand = 3
  formula = G4_ETHYLENE
  name = G4_ETHYLENE
  specific = 4
FEATURE [App::DocumentObjectGroupPython] H_element039  label="H_element : 0.096"  # scripted group (container) (typed FeaturePython)
  n = 0.096
FEATURE [App::DocumentObjectGroupPython] C_element042  label="C_element : 0.195"  # scripted group (container) (typed FeaturePython)
  n = 0.195
FEATURE [App::DocumentObjectGroupPython] N_element016  label="N_element : 0.057"  # scripted group (container) (typed FeaturePython)
  n = 0.057
FEATURE [App::DocumentObjectGroupPython] O_element037  label="O_element : 0.646"  # scripted group (container) (typed FeaturePython)
  n = 0.646
FEATURE [App::DocumentObjectGroupPython] Na_element006  label="Na_element : 0.017"  # scripted group (container) (typed FeaturePython)
  n = 0.001
FEATURE [App::DocumentObjectGroupPython] P_element005  label="P_element : 0.104"  # scripted group (container) (typed FeaturePython)
  n = 0.001
FEATURE [App::DocumentObjectGroupPython] S_element010  label="S_element : 0.016"  # scripted group (container) (typed FeaturePython)
  n = 0.003
FEATURE [App::DocumentObjectGroupPython] Cl_element010  label="Cl_element : 0.005"  # scripted group (container) (typed FeaturePython)
  n = 0.001
FEATURE [App::DocumentObjectGroupPython] G4_EYE_LENS_ICRP  # scripted group (container) (typed FeaturePython)
  Dunit = g/cm3
  Dvalue = 1.07
  Group = -> [H_element039,C_element042,N_element016,O_element037,Na_element006,P_element005,S_element010,Cl_element010]
  conduct = 2
  density = 1
  expand = 3
  formula = G4_EYE_LENS_ICRP
  name = G4_EYE_LENS_ICRP
  specific = 4
FEATURE [App::DocumentObjectGroupPython] Fe_element003  label="Fe_element : 2"  # scripted group (container) (typed FeaturePython)
  n = 2
  ref = Fe_element
FEATURE [App::DocumentObjectGroupPython] O_element038  label="O_element : 019"  # scripted group (container) (typed FeaturePython)
  n = 3
  ref = O_element
FEATURE [App::DocumentObjectGroupPython] G4_FERRIC_OXIDE  # scripted group (container) (typed FeaturePython)
  Dunit = g/cm3
  Dvalue = 5.2
  Group = -> [Fe_element003,O_element038]
  conduct = 2
  density = 1
  expand = 3
  formula = G4_FERRIC_OXIDE
  name = G4_FERRIC_OXIDE
  specific = 4
FEATURE [App::DocumentObjectGroupPython] Fe_element004  label="Fe_element : 1"  # scripted group (container) (typed FeaturePython)
  n = 1
  ref = Fe_element
FEATURE [App::DocumentObjectGroupPython] B_element003  label="B_element : 1"  # scripted group (container) (typed FeaturePython)
  n = 1
  ref = B_element
FEATURE [App::DocumentObjectGroupPython] G4_FERROBORIDE  # scripted group (container) (typed FeaturePython)
  Dunit = g/cm3
  Dvalue = 7.15
  Group = -> [Fe_element004,B_element003]
  conduct = 2
  density = 1
  expand = 3
  formula = G4_FERROBORIDE
  name = G4_FERROBORIDE
  specific = 4
FEATURE [App::DocumentObjectGroupPython] Fe_element005  label="Fe_element : 003"  # scripted group (container) (typed FeaturePython)
  n = 1
  ref = Fe_element
FEATURE [App::DocumentObjectGroupPython] O_element039  label="O_element : 020"  # scripted group (container) (typed FeaturePython)
  n = 1
  ref = O_element
FEATURE [App::DocumentObjectGroupPython] G4_FERROUS_OXIDE  # scripted group (container) (typed FeaturePython)
  Dunit = g/cm3
  Dvalue = 5.7
  Group = -> [Fe_element005,O_element039]
  conduct = 2
  density = 1
  expand = 3
  formula = G4_FERROUS_OXIDE
  name = G4_FERROUS_OXIDE
  specific = 4
FEATURE [App::DocumentObjectGroupPython] H_element040  label="H_element : 0.115"  # scripted group (container) (typed FeaturePython)
  n = 0.108259
FEATURE [App::DocumentObjectGroupPython] N_element017  label="N_element : 0.000"  # scripted group (container) (typed FeaturePython)
  n = 2.7e-05
FEATURE [App::DocumentObjectGroupPython] O_element040  label="O_element : 0.879"  # scripted group (container) (typed FeaturePython)
  n = 0.878636
FEATURE [App::DocumentObjectGroupPython] Na_element007  label="Na_element : 0.000"  # scripted group (container) (typed FeaturePython)
  n = 2.2e-05
FEATURE [App::DocumentObjectGroupPython] S_element011  label="S_element : 0.013"  # scripted group (container) (typed FeaturePython)
  n = 0.012968
FEATURE [App::DocumentObjectGroupPython] Cl_element011  label="Cl_element : 0.000"  # scripted group (container) (typed FeaturePython)
  n = 3.4e-05
FEATURE [App::DocumentObjectGroupPython] Fe_element006  label="Fe_element : 0.000"  # scripted group (container) (typed FeaturePython)
  n = 5.4e-05
FEATURE [App::DocumentObjectGroupPython] G4_FERROUS_SULFATE  # scripted group (container) (typed FeaturePython)
  Dunit = g/cm3
  Dvalue = 1.024
  Group = -> [H_element040,N_element017,O_element040,Na_element007,S_element011,Cl_element011,Fe_element006]
  conduct = 2
  density = 1
  expand = 3
  formula = G4_FERROUS_SULFATE
  name = G4_FERROUS_SULFATE
  specific = 4
FEATURE [App::DocumentObjectGroupPython] C_element043  label="C_element : 0.099"  # scripted group (container) (typed FeaturePython)
  n = 0.099335
FEATURE [App::DocumentObjectGroupPython] F_element007  label="F_element : 0.314"  # scripted group (container) (typed FeaturePython)
  n = 0.314247
FEATURE [App::DocumentObjectGroupPython] Cl_element012  label="Cl_element : 0.586"  # scripted group (container) (typed FeaturePython)
  n = 0.586418
FEATURE [App::DocumentObjectGroupPython] G4_FREON_12  label="G4_FREON-12"  # scripted group (container) (typed FeaturePython)
  Dunit = g/cm3
  Dvalue = 1.12
  Group = -> [C_element043,F_element007,Cl_element012]
  conduct = 2
  density = 1
  expand = 3
  formula = G4_FREON-12
  name = G4_FREON-12
  specific = 4
FEATURE [App::DocumentObjectGroupPython] C_element044  label="C_element : 0.057"  # scripted group (container) (typed FeaturePython)
  n = 0.057245
FEATURE [App::DocumentObjectGroupPython] F_element008  label="F_element : 0.181"  # scripted group (container) (typed FeaturePython)
  n = 0.181096
FEATURE [App::DocumentObjectGroupPython] Br_element001  label="Br_element : 0.762"  # scripted group (container) (typed FeaturePython)
  n = 0.761659
FEATURE [App::DocumentObjectGroupPython] G4_FREON_12B2  label="G4_FREON-12B2"  # scripted group (container) (typed FeaturePython)
  Dunit = g/cm3
  Dvalue = 1.8
  Group = -> [C_element044,F_element008,Br_element001]
  conduct = 2
  density = 1
  expand = 3
  formula = G4_FREON-12B2
  name = G4_FREON-12B2
  specific = 4
FEATURE [App::DocumentObjectGroupPython] C_element045  label="C_element : 0.115"  # scripted group (container) (typed FeaturePython)
  n = 0.114983
FEATURE [App::DocumentObjectGroupPython] F_element009  label="F_element : 0.546"  # scripted group (container) (typed FeaturePython)
  n = 0.545621
FEATURE [App::DocumentObjectGroupPython] Cl_element013  label="Cl_element : 0.339"  # scripted group (container) (typed FeaturePython)
  n = 0.339396
FEATURE [App::DocumentObjectGroupPython] G4_FREON_13  label="G4_FREON-13"  # scripted group (container) (typed FeaturePython)
  Dunit = g/cm3
  Dvalue = 0.95
  Group = -> [C_element045,F_element009,Cl_element013]
  conduct = 2
  density = 1
  expand = 3
  formula = G4_FREON-13
  name = G4_FREON-13
  specific = 4
FEATURE [App::DocumentObjectGroupPython] C_element046  label="C_element : 025"  # scripted group (container) (typed FeaturePython)
  n = 1
  ref = C_element
FEATURE [App::DocumentObjectGroupPython] F_element010  label="F_element : 3"  # scripted group (container) (typed FeaturePython)
  n = 3
  ref = F_element
FEATURE [App::DocumentObjectGroupPython] Br_element002  label="Br_element : 1"  # scripted group (container) (typed FeaturePython)
  n = 1
  ref = Br_element
FEATURE [App::DocumentObjectGroupPython] G4_FREON_13B1  label="G4_FREON-13B1"  # scripted group (container) (typed FeaturePython)
  Dunit = g/cm3
  Dvalue = 1.5
  Group = -> [C_element046,F_element010,Br_element002]
  conduct = 2
  density = 1
  expand = 3
  formula = G4_FREON-13B1
  name = G4_FREON-13B1
  specific = 4
FEATURE [App::DocumentObjectGroupPython] C_element047  label="C_element : 0.061"  # scripted group (container) (typed FeaturePython)
  n = 0.061309
FEATURE [App::DocumentObjectGroupPython] F_element011  label="F_element : 0.291"  # scripted group (container) (typed FeaturePython)
  n = 0.290924
FEATURE [App::DocumentObjectGroupPython] I_element002  label="I_element : 0.648"  # scripted group (container) (typed FeaturePython)
  n = 0.647767
FEATURE [App::DocumentObjectGroupPython] G4_FREON_13I1  label="G4_FREON-13I1"  # scripted group (container) (typed FeaturePython)
  Dunit = g/cm3
  Dvalue = 1.8
  Group = -> [C_element047,F_element011,I_element002]
  conduct = 2
  density = 1
  expand = 3
  formula = G4_FREON-13I1
  name = G4_FREON-13I1
  specific = 4
FEATURE [App::DocumentObjectGroupPython] Gd_element001  label="Gd_element : 2"  # scripted group (container) (typed FeaturePython)
  n = 2
  ref = Gd_element
FEATURE [App::DocumentObjectGroupPython] O_element041  label="O_element : 021"  # scripted group (container) (typed FeaturePython)
  n = 2
  ref = O_element
FEATURE [App::DocumentObjectGroupPython] S_element012  label="S_element : 004"  # scripted group (container) (typed FeaturePython)
  n = 1
  ref = S_element
FEATURE [App::DocumentObjectGroupPython] G4_GADOLINIUM_OXYSULFIDE  # scripted group (container) (typed FeaturePython)
  Dunit = g/cm3
  Dvalue = 7.44
  Group = -> [Gd_element001,O_element041,S_element012]
  conduct = 2
  density = 1
  expand = 3
  formula = G4_GADOLINIUM_OXYSULFIDE
  name = G4_GADOLINIUM_OXYSULFIDE
  specific = 4
FEATURE [App::DocumentObjectGroupPython] Ga_element001  label="Ga_element : 1"  # scripted group (container) (typed FeaturePython)
  n = 1
  ref = Ga_element
FEATURE [App::DocumentObjectGroupPython] As_element001  label="As_element : 1"  # scripted group (container) (typed FeaturePython)
  n = 1
  ref = As_element
FEATURE [App::DocumentObjectGroupPython] G4_GALLIUM_ARSENIDE  # scripted group (container) (typed FeaturePython)
  Dunit = g/cm3
  Dvalue = 5.31
  Group = -> [Ga_element001,As_element001]
  conduct = 2
  density = 1
  expand = 3
  formula = G4_GALLIUM_ARSENIDE
  name = G4_GALLIUM_ARSENIDE
  specific = 4
FEATURE [App::DocumentObjectGroupPython] H_element041  label="H_element : 0.081"  # scripted group (container) (typed FeaturePython)
  n = 0.08118
FEATURE [App::DocumentObjectGroupPython] C_element048  label="C_element : 0.416"  # scripted group (container) (typed FeaturePython)
  n = 0.41606
FEATURE [App::DocumentObjectGroupPython] N_element018  label="N_element : 0.111"  # scripted group (container) (typed FeaturePython)
  n = 0.11124
FEATURE [App::DocumentObjectGroupPython] O_element042  label="O_element : 0.381"  # scripted group (container) (typed FeaturePython)
  n = 0.38064
FEATURE [App::DocumentObjectGroupPython] S_element013  label="S_element : 0.011"  # scripted group (container) (typed FeaturePython)
  n = 0.01088
FEATURE [App::DocumentObjectGroupPython] G4_GEL_PHOTO_EMULSION  # scripted group (container) (typed FeaturePython)
  Dunit = g/cm3
  Dvalue = 1.2914
  Group = -> [H_element041,C_element048,N_element018,O_element042,S_element013]
  conduct = 2
  density = 1
  expand = 3
  formula = G4_GEL_PHOTO_EMULSION
  name = G4_GEL_PHOTO_EMULSION
  specific = 4
FEATURE [App::DocumentObjectGroupPython] B_element004  label="B_element : 0.040"  # scripted group (container) (typed FeaturePython)
  n = 0.0400639
FEATURE [App::DocumentObjectGroupPython] O_element043  label="O_element : 0.540"  # scripted group (container) (typed FeaturePython)
  n = 0.539561
FEATURE [App::DocumentObjectGroupPython] Na_element008  label="Na_element : 0.028"  # scripted group (container) (typed FeaturePython)
  n = 0.0281909
FEATURE [App::DocumentObjectGroupPython] Al_element003  label="Al_element : 0.012"  # scripted group (container) (typed FeaturePython)
  n = 0.011644
FEATURE [App::DocumentObjectGroupPython] Si_element003  label="Si_element : 0.377"  # scripted group (container) (typed FeaturePython)
  n = 0.377219
FEATURE [App::DocumentObjectGroupPython] K_element004  label="K_element : 0.014"  # scripted group (container) (typed FeaturePython)
  n = 0.00332099
FEATURE [App::DocumentObjectGroupPython] G4_Pyrex_Glass  # scripted group (container) (typed FeaturePython)
  Dunit = g/cm3
  Dvalue = 2.23
  Group = -> [B_element004,O_element043,Na_element008,Al_element003,Si_element003,K_element004]
  conduct = 2
  density = 1
  expand = 3
  formula = G4_Pyrex_Glass
  name = G4_Pyrex_Glass
  specific = 4
FEATURE [App::DocumentObjectGroupPython] O_element044  label="O_element : 0.156"  # scripted group (container) (typed FeaturePython)
  n = 0.156453
FEATURE [App::DocumentObjectGroupPython] Si_element004  label="Si_element : 0.081"  # scripted group (container) (typed FeaturePython)
  n = 0.080866
FEATURE [App::DocumentObjectGroupPython] Ti_element001  label="Ti_element : 0.008"  # scripted group (container) (typed FeaturePython)
  n = 0.008092
FEATURE [App::DocumentObjectGroupPython] As_element002  label="As_element : 0.003"  # scripted group (container) (typed FeaturePython)
  n = 0.002651
FEATURE [App::DocumentObjectGroupPython] Pb_element001  label="Pb_element : 0.752"  # scripted group (container) (typed FeaturePython)
  n = 0.751938
FEATURE [App::DocumentObjectGroupPython] G4_GLASS_LEAD  # scripted group (container) (typed FeaturePython)
  Dunit = g/cm3
  Dvalue = 6.22
  Group = -> [O_element044,Si_element004,Ti_element001,As_element002,Pb_element001]
  conduct = 2
  density = 1
  expand = 3
  formula = G4_GLASS_LEAD
  name = G4_GLASS_LEAD
  specific = 4
FEATURE [App::DocumentObjectGroupPython] O_element045  label="O_element : 0.460"  # scripted group (container) (typed FeaturePython)
  n = 0.4598
FEATURE [App::DocumentObjectGroupPython] Na_element009  label="Na_element : 0.096"  # scripted group (container) (typed FeaturePython)
  n = 0.0964411
FEATURE [App::DocumentObjectGroupPython] Si_element005  label="Si_element : 0.378"  # scripted group (container) (typed FeaturePython)
  n = 0.336553
FEATURE [App::DocumentObjectGroupPython] Ca_element011  label="Ca_element : 0.107"  # scripted group (container) (typed FeaturePython)
  n = 0.107205
FEATURE [App::DocumentObjectGroupPython] G4_GLASS_PLATE  # scripted group (container) (typed FeaturePython)
  Dunit = g/cm3
  Dvalue = 2.4
  Group = -> [O_element045,Na_element009,Si_element005,Ca_element011]
  conduct = 2
  density = 1
  expand = 3
  formula = G4_GLASS_PLATE
  name = G4_GLASS_PLATE
  specific = 4
FEATURE [App::DocumentObjectGroupPython] C_element049  label="C_element : 026"  # scripted group (container) (typed FeaturePython)
  n = 5
  ref = C_element
FEATURE [App::DocumentObjectGroupPython] H_element042  label="H_element : 021"  # scripted group (container) (typed FeaturePython)
  n = 10
  ref = H_element
FEATURE [App::DocumentObjectGroupPython] N_element019  label="N_element : 2"  # scripted group (container) (typed FeaturePython)
  n = 2
  ref = N_element
FEATURE [App::DocumentObjectGroupPython] O_element046  label="O_element : 022"  # scripted group (container) (typed FeaturePython)
  n = 3
  ref = O_element
FEATURE [App::DocumentObjectGroupPython] G4_GLUTAMINE  # scripted group (container) (typed FeaturePython)
  Dunit = g/cm3
  Dvalue = 1.46
  Group = -> [C_element049,H_element042,N_element019,O_element046]
  conduct = 2
  density = 1
  expand = 3
  formula = G4_GLUTAMINE
  name = G4_GLUTAMINE
  specific = 4
FEATURE [App::DocumentObjectGroupPython] C_element050  label="C_element : 027"  # scripted group (container) (typed FeaturePython)
  n = 3
  ref = C_element
FEATURE [App::DocumentObjectGroupPython] H_element043  label="H_element : 022"  # scripted group (container) (typed FeaturePython)
  n = 8
  ref = H_element
FEATURE [App::DocumentObjectGroupPython] O_element047  label="O_element : 023"  # scripted group (container) (typed FeaturePython)
  n = 3
  ref = O_element
FEATURE [App::DocumentObjectGroupPython] G4_GLYCEROL  # scripted group (container) (typed FeaturePython)
  Dunit = g/cm3
  Dvalue = 1.2613
  Group = -> [C_element050,H_element043,O_element047]
  conduct = 2
  density = 1
  expand = 3
  formula = G4_GLYCEROL
  name = G4_GLYCEROL
  specific = 4
FEATURE [App::DocumentObjectGroupPython] C_element051  label="C_element : 028"  # scripted group (container) (typed FeaturePython)
  n = 5
  ref = C_element
FEATURE [App::DocumentObjectGroupPython] H_element044  label="H_element : 023"  # scripted group (container) (typed FeaturePython)
  n = 5
  ref = H_element
FEATURE [App::DocumentObjectGroupPython] N_element020  label="N_element : 009"  # scripted group (container) (typed FeaturePython)
  n = 5
  ref = N_element
FEATURE [App::DocumentObjectGroupPython] O_element048  label="O_element : 024"  # scripted group (container) (typed FeaturePython)
  n = 1
  ref = O_element
FEATURE [App::DocumentObjectGroupPython] G4_GUANINE  # scripted group (container) (typed FeaturePython)
  Dunit = g/cm3
  Dvalue = 2.2
  Group = -> [C_element051,H_element044,N_element020,O_element048]
  conduct = 2
  density = 1
  expand = 3
  formula = G4_GUANINE
  name = G4_GUANINE
  specific = 4
FEATURE [App::DocumentObjectGroupPython] Ca_element012  label="Ca_element : 006"  # scripted group (container) (typed FeaturePython)
  n = 1
  ref = Ca_element
FEATURE [App::DocumentObjectGroupPython] S_element014  label="S_element : 005"  # scripted group (container) (typed FeaturePython)
  n = 1
  ref = S_element
FEATURE [App::DocumentObjectGroupPython] O_element049  label="O_element : 6"  # scripted group (container) (typed FeaturePython)
  n = 6
  ref = O_element
FEATURE [App::DocumentObjectGroupPython] H_element045  label="H_element : 024"  # scripted group (container) (typed FeaturePython)
  n = 4
  ref = H_element
FEATURE [App::DocumentObjectGroupPython] G4_GYPSUM  # scripted group (container) (typed FeaturePython)
  Dunit = g/cm3
  Dvalue = 2.32
  Group = -> [Ca_element012,S_element014,O_element049,H_element045]
  conduct = 2
  density = 1
  expand = 3
  formula = G4_GYPSUM
  name = G4_GYPSUM
  specific = 4
FEATURE [App::DocumentObjectGroupPython] C_element052  label="C_element : 7"  # scripted group (container) (typed FeaturePython)
  n = 7
  ref = C_element
FEATURE [App::DocumentObjectGroupPython] H_element046  label="H_element : 16"  # scripted group (container) (typed FeaturePython)
  n = 16
  ref = H_element
FEATURE [App::DocumentObjectGroupPython] G4_N_HEPTANE  label="G4_N-HEPTANE"  # scripted group (container) (typed FeaturePython)
  Dunit = g/cm3
  Dvalue = 0.68376
  Group = -> [C_element052,H_element046]
  conduct = 2
  density = 1
  expand = 3
  formula = G4_N-HEPTANE
  name = G4_N-HEPTANE
  specific = 4
FEATURE [App::DocumentObjectGroupPython] C_element053  label="C_element : 029"  # scripted group (container) (typed FeaturePython)
  n = 6
  ref = C_element
FEATURE [App::DocumentObjectGroupPython] H_element047  label="H_element : 14"  # scripted group (container) (typed FeaturePython)
  n = 14
  ref = H_element
FEATURE [App::DocumentObjectGroupPython] G4_N_HEXANE  label="G4_N-HEXANE"  # scripted group (container) (typed FeaturePython)
  Dunit = g/cm3
  Dvalue = 0.6603
  Group = -> [C_element053,H_element047]
  conduct = 2
  density = 1
  expand = 3
  formula = G4_N-HEXANE
  name = G4_N-HEXANE
  specific = 4
FEATURE [App::DocumentObjectGroupPython] C_element054  label="C_element : 22"  # scripted group (container) (typed FeaturePython)
  n = 22
  ref = C_element
FEATURE [App::DocumentObjectGroupPython] H_element048  label="H_element : 025"  # scripted group (container) (typed FeaturePython)
  n = 10
  ref = H_element
FEATURE [App::DocumentObjectGroupPython] N_element021  label="N_element : 010"  # scripted group (container) (typed FeaturePython)
  n = 2
  ref = N_element
FEATURE [App::DocumentObjectGroupPython] O_element050  label="O_element : 025"  # scripted group (container) (typed FeaturePython)
  n = 5
  ref = O_element
FEATURE [App::DocumentObjectGroupPython] G4_KAPTON  # scripted group (container) (typed FeaturePython)
  Dunit = g/cm3
  Dvalue = 1.42
  Group = -> [C_element054,H_element048,N_element021,O_element050]
  conduct = 2
  density = 1
  expand = 3
  formula = G4_KAPTON
  name = G4_KAPTON
  specific = 4
FEATURE [App::DocumentObjectGroupPython] La_element001  label="La_element : 1"  # scripted group (container) (typed FeaturePython)
  n = 1
  ref = La_element
FEATURE [App::DocumentObjectGroupPython] Br_element003  label="Br_element : 002"  # scripted group (container) (typed FeaturePython)
  n = 1
  ref = Br_element
FEATURE [App::DocumentObjectGroupPython] O_element051  label="O_element : 026"  # scripted group (container) (typed FeaturePython)
  n = 1
  ref = O_element
FEATURE [App::DocumentObjectGroupPython] G4_LANTHANUM_OXYBROMIDE  # scripted group (container) (typed FeaturePython)
  Dunit = g/cm3
  Dvalue = 6.28
  Group = -> [La_element001,Br_element003,O_element051]
  conduct = 2
  density = 1
  expand = 3
  formula = G4_LANTHANUM_OXYBROMIDE
  name = G4_LANTHANUM_OXYBROMIDE
  specific = 4
FEATURE [App::DocumentObjectGroupPython] La_element002  label="La_element : 2"  # scripted group (container) (typed FeaturePython)
  n = 2
  ref = La_element
FEATURE [App::DocumentObjectGroupPython] O_element052  label="O_element : 027"  # scripted group (container) (typed FeaturePython)
  n = 2
  ref = O_element
FEATURE [App::DocumentObjectGroupPython] S_element015  label="S_element : 006"  # scripted group (container) (typed FeaturePython)
  n = 1
  ref = S_element
FEATURE [App::DocumentObjectGroupPython] G4_LANTHANUM_OXYSULFIDE  # scripted group (container) (typed FeaturePython)
  Dunit = g/cm3
  Dvalue = 5.86
  Group = -> [La_element002,O_element052,S_element015]
  conduct = 2
  density = 1
  expand = 3
  formula = G4_LANTHANUM_OXYSULFIDE
  name = G4_LANTHANUM_OXYSULFIDE
  specific = 4
FEATURE [App::DocumentObjectGroupPython] O_element053  label="O_element : 0.072"  # scripted group (container) (typed FeaturePython)
  n = 0.071682
FEATURE [App::DocumentObjectGroupPython] Pb_element002  label="Pb_element : 0.928"  # scripted group (container) (typed FeaturePython)
  n = 0.928318
FEATURE [App::DocumentObjectGroupPython] G4_LEAD_OXIDE  # scripted group (container) (typed FeaturePython)
  Dunit = g/cm3
  Dvalue = 9.53
  Group = -> [O_element053,Pb_element002]
  conduct = 2
  density = 1
  expand = 3
  formula = G4_LEAD_OXIDE
  name = G4_LEAD_OXIDE
  specific = 4
FEATURE [App::DocumentObjectGroupPython] Li_element001  label="Li_element : 1"  # scripted group (container) (typed FeaturePython)
  n = 1
  ref = Li_element
FEATURE [App::DocumentObjectGroupPython] N_element022  label="N_element : 011"  # scripted group (container) (typed FeaturePython)
  n = 1
  ref = N_element
FEATURE [App::DocumentObjectGroupPython] H_element049  label="H_element : 026"  # scripted group (container) (typed FeaturePython)
  n = 2
  ref = H_element
FEATURE [App::DocumentObjectGroupPython] G4_LITHIUM_AMIDE  # scripted group (container) (typed FeaturePython)
  Dunit = g/cm3
  Dvalue = 1.178
  Group = -> [Li_element001,N_element022,H_element049]
  conduct = 2
  density = 1
  expand = 3
  formula = G4_LITHIUM_AMIDE
  name = G4_LITHIUM_AMIDE
  specific = 4
FEATURE [App::DocumentObjectGroupPython] Li_element002  label="Li_element : 2"  # scripted group (container) (typed FeaturePython)
  n = 2
  ref = Li_element
FEATURE [App::DocumentObjectGroupPython] C_element055  label="C_element : 030"  # scripted group (container) (typed FeaturePython)
  n = 1
  ref = C_element
FEATURE [App::DocumentObjectGroupPython] O_element054  label="O_element : 028"  # scripted group (container) (typed FeaturePython)
  n = 3
  ref = O_element
FEATURE [App::DocumentObjectGroupPython] G4_LITHIUM_CARBONATE  # scripted group (container) (typed FeaturePython)
  Dunit = g/cm3
  Dvalue = 2.11
  Group = -> [Li_element002,C_element055,O_element054]
  conduct = 2
  density = 1
  expand = 3
  formula = G4_LITHIUM_CARBONATE
  name = G4_LITHIUM_CARBONATE
  specific = 4
FEATURE [App::DocumentObjectGroupPython] Li_element003  label="Li_element : 003"  # scripted group (container) (typed FeaturePython)
  n = 1
  ref = Li_element
FEATURE [App::DocumentObjectGroupPython] F_element012  label="F_element : 004"  # scripted group (container) (typed FeaturePython)
  n = 1
  ref = F_element
FEATURE [App::DocumentObjectGroupPython] G4_LITHIUM_FLUORIDE  # scripted group (container) (typed FeaturePython)
  Dunit = g/cm3
  Dvalue = 2.635
  Group = -> [Li_element003,F_element012]
  conduct = 2
  density = 1
  expand = 3
  formula = G4_LITHIUM_FLUORIDE
  name = G4_LITHIUM_FLUORIDE
  specific = 4
FEATURE [App::DocumentObjectGroupPython] Li_element004  label="Li_element : 004"  # scripted group (container) (typed FeaturePython)
  n = 1
  ref = Li_element
FEATURE [App::DocumentObjectGroupPython] H_element050  label="H_element : 027"  # scripted group (container) (typed FeaturePython)
  n = 1
  ref = H_element
FEATURE [App::DocumentObjectGroupPython] G4_LITHIUM_HYDRIDE  # scripted group (container) (typed FeaturePython)
  Dunit = g/cm3
  Dvalue = 0.82
  Group = -> [Li_element004,H_element050]
  conduct = 2
  density = 1
  expand = 3
  formula = G4_LITHIUM_HYDRIDE
  name = G4_LITHIUM_HYDRIDE
  specific = 4
FEATURE [App::DocumentObjectGroupPython] Li_element005  label="Li_element : 005"  # scripted group (container) (typed FeaturePython)
  n = 1
  ref = Li_element
FEATURE [App::DocumentObjectGroupPython] I_element003  label="I_element : 002"  # scripted group (container) (typed FeaturePython)
  n = 1
  ref = I_element
FEATURE [App::DocumentObjectGroupPython] G4_LITHIUM_IODIDE  # scripted group (container) (typed FeaturePython)
  Dunit = g/cm3
  Dvalue = 3.494
  Group = -> [Li_element005,I_element003]
  conduct = 2
  density = 1
  expand = 3
  formula = G4_LITHIUM_IODIDE
  name = G4_LITHIUM_IODIDE
  specific = 4
FEATURE [App::DocumentObjectGroupPython] Li_element006  label="Li_element : 006"  # scripted group (container) (typed FeaturePython)
  n = 2
  ref = Li_element
FEATURE [App::DocumentObjectGroupPython] O_element055  label="O_element : 029"  # scripted group (container) (typed FeaturePython)
  n = 1
  ref = O_element
FEATURE [App::DocumentObjectGroupPython] G4_LITHIUM_OXIDE  # scripted group (container) (typed FeaturePython)
  Dunit = g/cm3
  Dvalue = 2.013
  Group = -> [Li_element006,O_element055]
  conduct = 2
  density = 1
  expand = 3
  formula = G4_LITHIUM_OXIDE
  name = G4_LITHIUM_OXIDE
  specific = 4
FEATURE [App::DocumentObjectGroupPython] Li_element007  label="Li_element : 007"  # scripted group (container) (typed FeaturePython)
  n = 2
  ref = Li_element
FEATURE [App::DocumentObjectGroupPython] B_element005  label="B_element : 005"  # scripted group (container) (typed FeaturePython)
  n = 4
  ref = B_element
FEATURE [App::DocumentObjectGroupPython] O_element056  label="O_element : 7"  # scripted group (container) (typed FeaturePython)
  n = 7
  ref = O_element
FEATURE [App::DocumentObjectGroupPython] G4_LITHIUM_TETRABORATE  # scripted group (container) (typed FeaturePython)
  Dunit = g/cm3
  Dvalue = 2.44
  Group = -> [Li_element007,B_element005,O_element056]
  conduct = 2
  density = 1
  expand = 3
  formula = G4_LITHIUM_TETRABORATE
  name = G4_LITHIUM_TETRABORATE
  specific = 4
FEATURE [App::DocumentObjectGroupPython] H_element051  label="H_element : 0.105"  # scripted group (container) (typed FeaturePython)
  n = 0.105
FEATURE [App::DocumentObjectGroupPython] C_element056  label="C_element : 0.083"  # scripted group (container) (typed FeaturePython)
  n = 0.083
FEATURE [App::DocumentObjectGroupPython] N_element023  label="N_element : 0.023"  # scripted group (container) (typed FeaturePython)
  n = 0.023
FEATURE [App::DocumentObjectGroupPython] O_element057  label="O_element : 0.779"  # scripted group (container) (typed FeaturePython)
  n = 0.779
FEATURE [App::DocumentObjectGroupPython] Na_element010  label="Na_element : 0.097"  # scripted group (container) (typed FeaturePython)
  n = 0.002
FEATURE [App::DocumentObjectGroupPython] P_element006  label="P_element : 0.105"  # scripted group (container) (typed FeaturePython)
  n = 0.001
FEATURE [App::DocumentObjectGroupPython] S_element016  label="S_element : 0.017"  # scripted group (container) (typed FeaturePython)
  n = 0.002
FEATURE [App::DocumentObjectGroupPython] Cl_element014  label="Cl_element : 0.587"  # scripted group (container) (typed FeaturePython)
  n = 0.003
FEATURE [App::DocumentObjectGroupPython] K_element005  label="K_element : 0.015"  # scripted group (container) (typed FeaturePython)
  n = 0.002
FEATURE [App::DocumentObjectGroupPython] G4_LUNG_ICRP  # scripted group (container) (typed FeaturePython)
  Dunit = g/cm3
  Dvalue = 1.04
  Group = -> [H_element051,C_element056,N_element023,O_element057,Na_element010,P_element006,S_element016,Cl_element014,K_element005]
  conduct = 2
  density = 1
  expand = 3
  formula = G4_LUNG_ICRP
  name = G4_LUNG_ICRP
  specific = 4
FEATURE [App::DocumentObjectGroupPython] H_element052  label="H_element : 0.116"  # scripted group (container) (typed FeaturePython)
  n = 0.114318
FEATURE [App::DocumentObjectGroupPython] C_element057  label="C_element : 0.656"  # scripted group (container) (typed FeaturePython)
  n = 0.655824
FEATURE [App::DocumentObjectGroupPython] O_element058  label="O_element : 0.092"  # scripted group (container) (typed FeaturePython)
  n = 0.0921831
FEATURE [App::DocumentObjectGroupPython] Mg_element004  label="Mg_element : 0.135"  # scripted group (container) (typed FeaturePython)
  n = 0.134792
FEATURE [App::DocumentObjectGroupPython] Ca_element013  label="Ca_element : 0.003"  # scripted group (container) (typed FeaturePython)
  n = 0.002883
FEATURE [App::DocumentObjectGroupPython] G4_M3_WAX  # scripted group (container) (typed FeaturePython)
  Dunit = g/cm3
  Dvalue = 1.05
  Group = -> [H_element052,C_element057,O_element058,Mg_element004,Ca_element013]
  conduct = 2
  density = 1
  expand = 3
  formula = G4_M3_WAX
  name = G4_M3_WAX
  specific = 4
FEATURE [App::DocumentObjectGroupPython] Mg_element005  label="Mg_element : 1"  # scripted group (container) (typed FeaturePython)
  n = 1
  ref = Mg_element
FEATURE [App::DocumentObjectGroupPython] C_element058  label="C_element : 031"  # scripted group (container) (typed FeaturePython)
  n = 1
  ref = C_element
FEATURE [App::DocumentObjectGroupPython] O_element059  label="O_element : 030"  # scripted group (container) (typed FeaturePython)
  n = 3
  ref = O_element
FEATURE [App::DocumentObjectGroupPython] G4_MAGNESIUM_CARBONATE  # scripted group (container) (typed FeaturePython)
  Dunit = g/cm3
  Dvalue = 2.958
  Group = -> [Mg_element005,C_element058,O_element059]
  conduct = 2
  density = 1
  expand = 3
  formula = G4_MAGNESIUM_CARBONATE
  name = G4_MAGNESIUM_CARBONATE
  specific = 4
FEATURE [App::DocumentObjectGroupPython] Mg_element006  label="Mg_element : 002"  # scripted group (container) (typed FeaturePython)
  n = 1
  ref = Mg_element
FEATURE [App::DocumentObjectGroupPython] F_element013  label="F_element : 005"  # scripted group (container) (typed FeaturePython)
  n = 2
  ref = F_element
FEATURE [App::DocumentObjectGroupPython] G4_MAGNESIUM_FLUORIDE  # scripted group (container) (typed FeaturePython)
  Dunit = g/cm3
  Dvalue = 3
  Group = -> [Mg_element006,F_element013]
  conduct = 2
  density = 1
  expand = 3
  formula = G4_MAGNESIUM_FLUORIDE
  name = G4_MAGNESIUM_FLUORIDE
  specific = 4
FEATURE [App::DocumentObjectGroupPython] Mg_element007  label="Mg_element : 003"  # scripted group (container) (typed FeaturePython)
  n = 1
  ref = Mg_element
FEATURE [App::DocumentObjectGroupPython] O_element060  label="O_element : 031"  # scripted group (container) (typed FeaturePython)
  n = 1
  ref = O_element
FEATURE [App::DocumentObjectGroupPython] G4_MAGNESIUM_OXIDE  # scripted group (container) (typed FeaturePython)
  Dunit = g/cm3
  Dvalue = 3.58
  Group = -> [Mg_element007,O_element060]
  conduct = 2
  density = 1
  expand = 3
  formula = G4_MAGNESIUM_OXIDE
  name = G4_MAGNESIUM_OXIDE
  specific = 4
FEATURE [App::DocumentObjectGroupPython] Mg_element008  label="Mg_element : 004"  # scripted group (container) (typed FeaturePython)
  n = 1
  ref = Mg_element
FEATURE [App::DocumentObjectGroupPython] B_element006  label="B_element : 006"  # scripted group (container) (typed FeaturePython)
  n = 4
  ref = B_element
FEATURE [App::DocumentObjectGroupPython] O_element061  label="O_element : 032"  # scripted group (container) (typed FeaturePython)
  n = 7
  ref = O_element
FEATURE [App::DocumentObjectGroupPython] G4_MAGNESIUM_TETRABORATE  # scripted group (container) (typed FeaturePython)
  Dunit = g/cm3
  Dvalue = 2.53
  Group = -> [Mg_element008,B_element006,O_element061]
  conduct = 2
  density = 1
  expand = 3
  formula = G4_MAGNESIUM_TETRABORATE
  name = G4_MAGNESIUM_TETRABORATE
  specific = 4
FEATURE [App::DocumentObjectGroupPython] Hg_element001  label="Hg_element : 1"  # scripted group (container) (typed FeaturePython)
  n = 1
  ref = Hg_element
FEATURE [App::DocumentObjectGroupPython] I_element004  label="I_element : 2"  # scripted group (container) (typed FeaturePython)
  n = 2
  ref = I_element
FEATURE [App::DocumentObjectGroupPython] G4_MERCURIC_IODIDE  # scripted group (container) (typed FeaturePython)
  Dunit = g/cm3
  Dvalue = 6.36
  Group = -> [Hg_element001,I_element004]
  conduct = 2
  density = 1
  expand = 3
  formula = G4_MERCURIC_IODIDE
  name = G4_MERCURIC_IODIDE
  specific = 4
FEATURE [App::DocumentObjectGroupPython] C_element059  label="C_element : 032"  # scripted group (container) (typed FeaturePython)
  n = 1
  ref = C_element
FEATURE [App::DocumentObjectGroupPython] H_element053  label="H_element : 028"  # scripted group (container) (typed FeaturePython)
  n = 4
  ref = H_element
FEATURE [App::DocumentObjectGroupPython] G4_METHANE  # scripted group (container) (typed FeaturePython)
  Dunit = g/cm3
  Dvalue = 0.000667151
  Group = -> [C_element059,H_element053]
  conduct = 2
  density = 1
  expand = 3
  formula = G4_METHANE
  name = G4_METHANE
  specific = 4
FEATURE [App::DocumentObjectGroupPython] C_element060  label="C_element : 033"  # scripted group (container) (typed FeaturePython)
  n = 1
  ref = C_element
FEATURE [App::DocumentObjectGroupPython] H_element054  label="H_element : 029"  # scripted group (container) (typed FeaturePython)
  n = 4
  ref = H_element
FEATURE [App::DocumentObjectGroupPython] O_element062  label="O_element : 033"  # scripted group (container) (typed FeaturePython)
  n = 1
  ref = O_element
FEATURE [App::DocumentObjectGroupPython] G4_METHANOL  # scripted group (container) (typed FeaturePython)
  Dunit = g/cm3
  Dvalue = 0.7914
  Group = -> [C_element060,H_element054,O_element062]
  conduct = 2
  density = 1
  expand = 3
  formula = G4_METHANOL
  name = G4_METHANOL
  specific = 4
FEATURE [App::DocumentObjectGroupPython] H_element055  label="H_element : 0.134"  # scripted group (container) (typed FeaturePython)
  n = 0.13404
FEATURE [App::DocumentObjectGroupPython] C_element061  label="C_element : 0.778"  # scripted group (container) (typed FeaturePython)
  n = 0.77796
FEATURE [App::DocumentObjectGroupPython] O_element063  label="O_element : 0.035"  # scripted group (container) (typed FeaturePython)
  n = 0.03502
FEATURE [App::DocumentObjectGroupPython] Mg_element009  label="Mg_element : 0.039"  # scripted group (container) (typed FeaturePython)
  n = 0.038594
FEATURE [App::DocumentObjectGroupPython] Ti_element002  label="Ti_element : 0.014"  # scripted group (container) (typed FeaturePython)
  n = 0.014386
FEATURE [App::DocumentObjectGroupPython] G4_MIX_D_WAX  # scripted group (container) (typed FeaturePython)
  Dunit = g/cm3
  Dvalue = 0.99
  Group = -> [H_element055,C_element061,O_element063,Mg_element009,Ti_element002]
  conduct = 2
  density = 1
  expand = 3
  formula = G4_MIX_D_WAX
  name = G4_MIX_D_WAX
  specific = 4
FEATURE [App::DocumentObjectGroupPython] H_element056  label="H_element : 0.135"  # scripted group (container) (typed FeaturePython)
  n = 0.081192
FEATURE [App::DocumentObjectGroupPython] C_element062  label="C_element : 0.583"  # scripted group (container) (typed FeaturePython)
  n = 0.583442
FEATURE [App::DocumentObjectGroupPython] N_element024  label="N_element : 0.018"  # scripted group (container) (typed FeaturePython)
  n = 0.017798
FEATURE [App::DocumentObjectGroupPython] O_element064  label="O_element : 0.186"  # scripted group (container) (typed FeaturePython)
  n = 0.186381
FEATURE [App::DocumentObjectGroupPython] Mg_element010  label="Mg_element : 0.130"  # scripted group (container) (typed FeaturePython)
  n = 0.130287
FEATURE [App::DocumentObjectGroupPython] Cl_element015  label="Cl_element : 0.588"  # scripted group (container) (typed FeaturePython)
  n = 0.0009
FEATURE [App::DocumentObjectGroupPython] G4_MS20_TISSUE  # scripted group (container) (typed FeaturePython)
  Dunit = g/cm3
  Dvalue = 1
  Group = -> [H_element056,C_element062,N_element024,O_element064,Mg_element010,Cl_element015]
  conduct = 2
  density = 1
  expand = 3
  formula = G4_MS20_TISSUE
  name = G4_MS20_TISSUE
  specific = 4
FEATURE [App::DocumentObjectGroupPython] H_element057  label="H_element : 0.136"  # scripted group (container) (typed FeaturePython)
  n = 0.102
FEATURE [App::DocumentObjectGroupPython] C_element063  label="C_element : 0.143"  # scripted group (container) (typed FeaturePython)
  n = 0.143
FEATURE [App::DocumentObjectGroupPython] N_element025  label="N_element : 0.034"  # scripted group (container) (typed FeaturePython)
  n = 0.034
FEATURE [App::DocumentObjectGroupPython] O_element065  label="O_element : 0.710"  # scripted group (container) (typed FeaturePython)
  n = 0.71
FEATURE [App::DocumentObjectGroupPython] Na_element011  label="Na_element : 0.098"  # scripted group (container) (typed FeaturePython)
  n = 0.001
FEATURE [App::DocumentObjectGroupPython] P_element007  label="P_element : 0.002"  # scripted group (container) (typed FeaturePython)
  n = 0.002
FEATURE [App::DocumentObjectGroupPython] S_element017  label="S_element : 0.018"  # scripted group (container) (typed FeaturePython)
  n = 0.003
FEATURE [App::DocumentObjectGroupPython] Cl_element016  label="Cl_element : 0.589"  # scripted group (container) (typed FeaturePython)
  n = 0.001
FEATURE [App::DocumentObjectGroupPython] K_element006  label="K_element : 0.004"  # scripted group (container) (typed FeaturePython)
  n = 0.004
FEATURE [App::DocumentObjectGroupPython] G4_MUSCLE_SKELETAL_ICRP  # scripted group (container) (typed FeaturePython)
  Dunit = g/cm3
  Dvalue = 1.05
  Group = -> [H_element057,C_element063,N_element025,O_element065,Na_element011,P_element007,S_element017,Cl_element016,K_element006]
  conduct = 2
  density = 1
  expand = 3
  formula = G4_MUSCLE_SKELETAL_ICRP
  name = G4_MUSCLE_SKELETAL_ICRP
  specific = 4
FEATURE [App::DocumentObjectGroupPython] H_element058  label="H_element : 0.137"  # scripted group (container) (typed FeaturePython)
  n = 0.102102
FEATURE [App::DocumentObjectGroupPython] C_element064  label="C_element : 0.123"  # scripted group (container) (typed FeaturePython)
  n = 0.123123
FEATURE [App::DocumentObjectGroupPython] N_element026  label="N_element : 0.756"  # scripted group (container) (typed FeaturePython)
  n = 0.035035
FEATURE [App::DocumentObjectGroupPython] O_element066  label="O_element : 0.730"  # scripted group (container) (typed FeaturePython)
  n = 0.72973
FEATURE [App::DocumentObjectGroupPython] Na_element012  label="Na_element : 0.099"  # scripted group (container) (typed FeaturePython)
  n = 0.001001
FEATURE [App::DocumentObjectGroupPython] P_element008  label="P_element : 0.106"  # scripted group (container) (typed FeaturePython)
  n = 0.002002
FEATURE [App::DocumentObjectGroupPython] S_element018  label="S_element : 0.019"  # scripted group (container) (typed FeaturePython)
  n = 0.004004
FEATURE [App::DocumentObjectGroupPython] K_element007  label="K_element : 0.016"  # scripted group (container) (typed FeaturePython)
  n = 0.003003
FEATURE [App::DocumentObjectGroupPython] G4_MUSCLE_STRIATED_ICRU  # scripted group (container) (typed FeaturePython)
  Dunit = g/cm3
  Dvalue = 1.04
  Group = -> [H_element058,C_element064,N_element026,O_element066,Na_element012,P_element008,S_element018,K_element007]
  conduct = 2
  density = 1
  expand = 3
  formula = G4_MUSCLE_STRIATED_ICRU
  name = G4_MUSCLE_STRIATED_ICRU
  specific = 4
FEATURE [App::DocumentObjectGroupPython] H_element059  label="H_element : 0.098"  # scripted group (container) (typed FeaturePython)
  n = 0.0982341
FEATURE [App::DocumentObjectGroupPython] C_element065  label="C_element : 0.156"  # scripted group (container) (typed FeaturePython)
  n = 0.156214
FEATURE [App::DocumentObjectGroupPython] N_element027  label="N_element : 0.757"  # scripted group (container) (typed FeaturePython)
  n = 0.035451
FEATURE [App::DocumentObjectGroupPython] O_element067  label="O_element : 0.880"  # scripted group (container) (typed FeaturePython)
  n = 0.710101
FEATURE [App::DocumentObjectGroupPython] G4_MUSCLE_WITH_SUCROSE  # scripted group (container) (typed FeaturePython)
  Dunit = g/cm3
  Dvalue = 1.11
  Group = -> [H_element059,C_element065,N_element027,O_element067]
  conduct = 2
  density = 1
  expand = 3
  formula = G4_MUSCLE_WITH_SUCROSE
  name = G4_MUSCLE_WITH_SUCROSE
  specific = 4
FEATURE [App::DocumentObjectGroupPython] H_element060  label="H_element : 0.138"  # scripted group (container) (typed FeaturePython)
  n = 0.101969
FEATURE [App::DocumentObjectGroupPython] C_element066  label="C_element : 0.120"  # scripted group (container) (typed FeaturePython)
  n = 0.120058
FEATURE [App::DocumentObjectGroupPython] N_element028  label="N_element : 0.758"  # scripted group (container) (typed FeaturePython)
  n = 0.035451
FEATURE [App::DocumentObjectGroupPython] O_element068  label="O_element : 0.743"  # scripted group (container) (typed FeaturePython)
  n = 0.742522
FEATURE [App::DocumentObjectGroupPython] G4_MUSCLE_WITHOUT_SUCROSE  # scripted group (container) (typed FeaturePython)
  Dunit = g/cm3
  Dvalue = 1.07
  Group = -> [H_element060,C_element066,N_element028,O_element068]
  conduct = 2
  density = 1
  expand = 3
  formula = G4_MUSCLE_WITHOUT_SUCROSE
  name = G4_MUSCLE_WITHOUT_SUCROSE
  specific = 4
FEATURE [App::DocumentObjectGroupPython] C_element067  label="C_element : 10"  # scripted group (container) (typed FeaturePython)
  n = 10
  ref = C_element
FEATURE [App::DocumentObjectGroupPython] H_element061  label="H_element : 030"  # scripted group (container) (typed FeaturePython)
  n = 8
  ref = H_element
FEATURE [App::DocumentObjectGroupPython] G4_NAPHTHALENE  # scripted group (container) (typed FeaturePython)
  Dunit = g/cm3
  Dvalue = 1.145
  Group = -> [C_element067,H_element061]
  conduct = 2
  density = 1
  expand = 3
  formula = G4_NAPHTHALENE
  name = G4_NAPHTHALENE
  specific = 4
FEATURE [App::DocumentObjectGroupPython] C_element068  label="C_element : 034"  # scripted group (container) (typed FeaturePython)
  n = 6
  ref = C_element
FEATURE [App::DocumentObjectGroupPython] H_element062  label="H_element : 031"  # scripted group (container) (typed FeaturePython)
  n = 5
  ref = H_element
FEATURE [App::DocumentObjectGroupPython] N_element029  label="N_element : 012"  # scripted group (container) (typed FeaturePython)
  n = 1
  ref = N_element
FEATURE [App::DocumentObjectGroupPython] O_element069  label="O_element : 034"  # scripted group (container) (typed FeaturePython)
  n = 2
  ref = O_element
FEATURE [App::DocumentObjectGroupPython] G4_NITROBENZENE  # scripted group (container) (typed FeaturePython)
  Dunit = g/cm3
  Dvalue = 1.19867
  Group = -> [C_element068,H_element062,N_element029,O_element069]
  conduct = 2
  density = 1
  expand = 3
  formula = G4_NITROBENZENE
  name = G4_NITROBENZENE
  specific = 4
FEATURE [App::DocumentObjectGroupPython] N_element030  label="N_element : 013"  # scripted group (container) (typed FeaturePython)
  n = 2
  ref = N_element
FEATURE [App::DocumentObjectGroupPython] O_element070  label="O_element : 035"  # scripted group (container) (typed FeaturePython)
  n = 1
  ref = O_element
FEATURE [App::DocumentObjectGroupPython] G4_NITROUS_OXIDE  # scripted group (container) (typed FeaturePython)
  Dunit = g/cm3
  Dvalue = 0.00183094
  Group = -> [N_element030,O_element070]
  conduct = 2
  density = 1
  expand = 3
  formula = G4_NITROUS_OXIDE
  name = G4_NITROUS_OXIDE
  specific = 4
FEATURE [App::DocumentObjectGroupPython] H_element063  label="H_element : 0.104"  # scripted group (container) (typed FeaturePython)
  n = 0.103509
FEATURE [App::DocumentObjectGroupPython] C_element069  label="C_element : 0.648"  # scripted group (container) (typed FeaturePython)
  n = 0.648416
FEATURE [App::DocumentObjectGroupPython] N_element031  label="N_element : 0.100"  # scripted group (container) (typed FeaturePython)
  n = 0.0995361
FEATURE [App::DocumentObjectGroupPython] O_element071  label="O_element : 0.149"  # scripted group (container) (typed FeaturePython)
  n = 0.148539
FEATURE [App::DocumentObjectGroupPython] G4_NYLON_8062  label="G4_NYLON-8062"  # scripted group (container) (typed FeaturePython)
  Dunit = g/cm3
  Dvalue = 1.08
  Group = -> [H_element063,C_element069,N_element031,O_element071]
  conduct = 2
  density = 1
  expand = 3
  formula = G4_NYLON-8062
  name = G4_NYLON-8062
  specific = 4
FEATURE [App::DocumentObjectGroupPython] C_element070  label="C_element : 035"  # scripted group (container) (typed FeaturePython)
  n = 6
  ref = C_element
FEATURE [App::DocumentObjectGroupPython] H_element064  label="H_element : 11"  # scripted group (container) (typed FeaturePython)
  n = 11
  ref = H_element
FEATURE [App::DocumentObjectGroupPython] N_element032  label="N_element : 014"  # scripted group (container) (typed FeaturePython)
  n = 1
  ref = N_element
FEATURE [App::DocumentObjectGroupPython] O_element072  label="O_element : 036"  # scripted group (container) (typed FeaturePython)
  n = 1
  ref = O_element
FEATURE [App::DocumentObjectGroupPython] G4_NYLON_6_6  label="G4_NYLON-6-6"  # scripted group (container) (typed FeaturePython)
  Dunit = g/cm3
  Dvalue = 1.14
  Group = -> [C_element070,H_element064,N_element032,O_element072]
  conduct = 2
  density = 1
  expand = 3
  formula = G4_NYLON-6-6
  name = G4_NYLON-6-6
  specific = 4
FEATURE [App::DocumentObjectGroupPython] H_element065  label="H_element : 0.139"  # scripted group (container) (typed FeaturePython)
  n = 0.107062
FEATURE [App::DocumentObjectGroupPython] C_element071  label="C_element : 0.680"  # scripted group (container) (typed FeaturePython)
  n = 0.680449
FEATURE [App::DocumentObjectGroupPython] N_element033  label="N_element : 0.099"  # scripted group (container) (typed FeaturePython)
  n = 0.099189
FEATURE [App::DocumentObjectGroupPython] O_element073  label="O_element : 0.113"  # scripted group (container) (typed FeaturePython)
  n = 0.1133
FEATURE [App::DocumentObjectGroupPython] G4_NYLON_6_10  label="G4_NYLON-6-10"  # scripted group (container) (typed FeaturePython)
  Dunit = g/cm3
  Dvalue = 1.14
  Group = -> [H_element065,C_element071,N_element033,O_element073]
  conduct = 2
  density = 1
  expand = 3
  formula = G4_NYLON-6-10
  name = G4_NYLON-6-10
  specific = 4
FEATURE [App::DocumentObjectGroupPython] H_element066  label="H_element : 0.140"  # scripted group (container) (typed FeaturePython)
  n = 0.115476
FEATURE [App::DocumentObjectGroupPython] C_element072  label="C_element : 0.721"  # scripted group (container) (typed FeaturePython)
  n = 0.720818
FEATURE [App::DocumentObjectGroupPython] N_element034  label="N_element : 0.076"  # scripted group (container) (typed FeaturePython)
  n = 0.0764169
FEATURE [App::DocumentObjectGroupPython] O_element074  label="O_element : 0.087"  # scripted group (container) (typed FeaturePython)
  n = 0.0872889
FEATURE [App::DocumentObjectGroupPython] G4_NYLON_11_RILSAN  label="G4_NYLON-11_RILSAN"  # scripted group (container) (typed FeaturePython)
  Dunit = g/cm3
  Dvalue = 1.425
  Group = -> [H_element066,C_element072,N_element034,O_element074]
  conduct = 2
  density = 1
  expand = 3
  formula = G4_NYLON-11_RILSAN
  name = G4_NYLON-11_RILSAN
  specific = 4
FEATURE [App::DocumentObjectGroupPython] C_element073  label="C_element : 8"  # scripted group (container) (typed FeaturePython)
  n = 8
  ref = C_element
FEATURE [App::DocumentObjectGroupPython] H_element067  label="H_element : 18"  # scripted group (container) (typed FeaturePython)
  n = 18
  ref = H_element
FEATURE [App::DocumentObjectGroupPython] G4_OCTANE  # scripted group (container) (typed FeaturePython)
  Dunit = g/cm3
  Dvalue = 0.7026
  Group = -> [C_element073,H_element067]
  conduct = 2
  density = 1
  expand = 3
  formula = G4_OCTANE
  name = G4_OCTANE
  specific = 4
FEATURE [App::DocumentObjectGroupPython] C_element074  label="C_element : 25"  # scripted group (container) (typed FeaturePython)
  n = 25
  ref = C_element
FEATURE [App::DocumentObjectGroupPython] H_element068  label="H_element : 52"  # scripted group (container) (typed FeaturePython)
  n = 52
  ref = H_element
FEATURE [App::DocumentObjectGroupPython] G4_PARAFFIN  # scripted group (container) (typed FeaturePython)
  Dunit = g/cm3
  Dvalue = 0.93
  Group = -> [C_element074,H_element068]
  conduct = 2
  density = 1
  expand = 3
  formula = G4_PARAFFIN
  name = G4_PARAFFIN
  specific = 4
FEATURE [App::DocumentObjectGroupPython] C_element075  label="C_element : 036"  # scripted group (container) (typed FeaturePython)
  n = 5
  ref = C_element
FEATURE [App::DocumentObjectGroupPython] H_element069  label="H_element : 032"  # scripted group (container) (typed FeaturePython)
  n = 12
  ref = H_element
FEATURE [App::DocumentObjectGroupPython] G4_N_PENTANE  label="G4_N-PENTANE"  # scripted group (container) (typed FeaturePython)
  Dunit = g/cm3
  Dvalue = 0.6262
  Group = -> [C_element075,H_element069]
  conduct = 2
  density = 1
  expand = 3
  formula = G4_N-PENTANE
  name = G4_N-PENTANE
  specific = 4
FEATURE [App::DocumentObjectGroupPython] H_element070  label="H_element : 0.014"  # scripted group (container) (typed FeaturePython)
  n = 0.0141
FEATURE [App::DocumentObjectGroupPython] C_element076  label="C_element : 0.072"  # scripted group (container) (typed FeaturePython)
  n = 0.072261
FEATURE [App::DocumentObjectGroupPython] N_element035  label="N_element : 0.019"  # scripted group (container) (typed FeaturePython)
  n = 0.01932
FEATURE [App::DocumentObjectGroupPython] O_element075  label="O_element : 0.066"  # scripted group (container) (typed FeaturePython)
  n = 0.066101
FEATURE [App::DocumentObjectGroupPython] S_element019  label="S_element : 0.020"  # scripted group (container) (typed FeaturePython)
  n = 0.00189
FEATURE [App::DocumentObjectGroupPython] Br_element004  label="Br_element : 0.349"  # scripted group (container) (typed FeaturePython)
  n = 0.349103
FEATURE [App::DocumentObjectGroupPython] Ag_element001  label="Ag_element : 0.474"  # scripted group (container) (typed FeaturePython)
  n = 0.474105
FEATURE [App::DocumentObjectGroupPython] I_element005  label="I_element : 0.003"  # scripted group (container) (typed FeaturePython)
  n = 0.00312
FEATURE [App::DocumentObjectGroupPython] G4_PHOTO_EMULSION  # scripted group (container) (typed FeaturePython)
  Dunit = g/cm3
  Dvalue = 3.815
  Group = -> [H_element070,C_element076,N_element035,O_element075,S_element019,Br_element004,Ag_element001,I_element005]
  conduct = 2
  density = 1
  expand = 3
  formula = G4_PHOTO_EMULSION
  name = G4_PHOTO_EMULSION
  specific = 4
FEATURE [App::DocumentObjectGroupPython] C_element077  label="C_element : 9"  # scripted group (container) (typed FeaturePython)
  n = 9
  ref = C_element
FEATURE [App::DocumentObjectGroupPython] H_element071  label="H_element : 033"  # scripted group (container) (typed FeaturePython)
  n = 10
  ref = H_element
FEATURE [App::DocumentObjectGroupPython] G4_PLASTIC_SC_VINYLTOLUENE  # scripted group (container) (typed FeaturePython)
  Dunit = g/cm3
  Dvalue = 1.032
  Group = -> [C_element077,H_element071]
  conduct = 2
  density = 1
  expand = 3
  formula = G4_PLASTIC_SC_VINYLTOLUENE
  name = G4_PLASTIC_SC_VINYLTOLUENE
  specific = 4
FEATURE [App::DocumentObjectGroupPython] Pu_element001  label="Pu_element : 1"  # scripted group (container) (typed FeaturePython)
  n = 1
  ref = Pu_element
FEATURE [App::DocumentObjectGroupPython] O_element076  label="O_element : 037"  # scripted group (container) (typed FeaturePython)
  n = 2
  ref = O_element
FEATURE [App::DocumentObjectGroupPython] G4_PLUTONIUM_DIOXIDE  # scripted group (container) (typed FeaturePython)
  Dunit = g/cm3
  Dvalue = 11.46
  Group = -> [Pu_element001,O_element076]
  conduct = 2
  density = 1
  expand = 3
  formula = G4_PLUTONIUM_DIOXIDE
  name = G4_PLUTONIUM_DIOXIDE
  specific = 4
FEATURE [App::DocumentObjectGroupPython] C_element078  label="C_element : 037"  # scripted group (container) (typed FeaturePython)
  n = 3
  ref = C_element
FEATURE [App::DocumentObjectGroupPython] H_element072  label="H_element : 034"  # scripted group (container) (typed FeaturePython)
  n = 3
  ref = H_element
FEATURE [App::DocumentObjectGroupPython] N_element036  label="N_element : 015"  # scripted group (container) (typed FeaturePython)
  n = 1
  ref = N_element
FEATURE [App::DocumentObjectGroupPython] G4_POLYACRYLONITRILE  # scripted group (container) (typed FeaturePython)
  Dunit = g/cm3
  Dvalue = 1.17
  Group = -> [C_element078,H_element072,N_element036]
  conduct = 2
  density = 1
  expand = 3
  formula = G4_POLYACRYLONITRILE
  name = G4_POLYACRYLONITRILE
  specific = 4
FEATURE [App::DocumentObjectGroupPython] C_element079  label="C_element : 16"  # scripted group (container) (typed FeaturePython)
  n = 16
  ref = C_element
FEATURE [App::DocumentObjectGroupPython] H_element073  label="H_element : 035"  # scripted group (container) (typed FeaturePython)
  n = 14
  ref = H_element
FEATURE [App::DocumentObjectGroupPython] O_element077  label="O_element : 038"  # scripted group (container) (typed FeaturePython)
  n = 3
  ref = O_element
FEATURE [App::DocumentObjectGroupPython] G4_POLYCARBONATE  # scripted group (container) (typed FeaturePython)
  Dunit = g/cm3
  Dvalue = 1.2
  Group = -> [C_element079,H_element073,O_element077]
  conduct = 2
  density = 1
  expand = 3
  formula = G4_POLYCARBONATE
  name = G4_POLYCARBONATE
  specific = 4
FEATURE [App::DocumentObjectGroupPython] C_element080  label="C_element : 038"  # scripted group (container) (typed FeaturePython)
  n = 8
  ref = C_element
FEATURE [App::DocumentObjectGroupPython] H_element074  label="H_element : 036"  # scripted group (container) (typed FeaturePython)
  n = 7
  ref = H_element
FEATURE [App::DocumentObjectGroupPython] Cl_element017  label="Cl_element : 007"  # scripted group (container) (typed FeaturePython)
  n = 1
  ref = Cl_element
FEATURE [App::DocumentObjectGroupPython] G4_POLYCHLOROSTYRENE  # scripted group (container) (typed FeaturePython)
  Dunit = g/cm3
  Dvalue = 1.3
  Group = -> [C_element080,H_element074,Cl_element017]
  conduct = 2
  density = 1
  expand = 3
  formula = G4_POLYCHLOROSTYRENE
  name = G4_POLYCHLOROSTYRENE
  specific = 4
FEATURE [App::DocumentObjectGroupPython] C_element081  label="C_element : 039"  # scripted group (container) (typed FeaturePython)
  n = 1
  ref = C_element
FEATURE [App::DocumentObjectGroupPython] H_element075  label="H_element : 037"  # scripted group (container) (typed FeaturePython)
  n = 2
  ref = H_element
FEATURE [App::DocumentObjectGroupPython] G4_POLYETHYLENE  # scripted group (container) (typed FeaturePython)
  Dunit = g/cm3
  Dvalue = 0.94
  Group = -> [C_element081,H_element075]
  conduct = 2
  density = 1
  expand = 3
  formula = G4_POLYETHYLENE
  name = G4_POLYETHYLENE
  specific = 4
FEATURE [App::DocumentObjectGroupPython] C_element082  label="C_element : 040"  # scripted group (container) (typed FeaturePython)
  n = 10
  ref = C_element
FEATURE [App::DocumentObjectGroupPython] H_element076  label="H_element : 038"  # scripted group (container) (typed FeaturePython)
  n = 8
  ref = H_element
FEATURE [App::DocumentObjectGroupPython] O_element078  label="O_element : 039"  # scripted group (container) (typed FeaturePython)
  n = 4
  ref = O_element
FEATURE [App::DocumentObjectGroupPython] G4_MYLAR  # scripted group (container) (typed FeaturePython)
  Dunit = g/cm3
  Dvalue = 1.4
  Group = -> [C_element082,H_element076,O_element078]
  conduct = 2
  density = 1
  expand = 3
  formula = G4_MYLAR
  name = G4_MYLAR
  specific = 4
FEATURE [App::DocumentObjectGroupPython] C_element083  label="C_element : 041"  # scripted group (container) (typed FeaturePython)
  n = 5
  ref = C_element
FEATURE [App::DocumentObjectGroupPython] H_element077  label="H_element : 039"  # scripted group (container) (typed FeaturePython)
  n = 8
  ref = H_element
FEATURE [App::DocumentObjectGroupPython] O_element079  label="O_element : 040"  # scripted group (container) (typed FeaturePython)
  n = 2
  ref = O_element
FEATURE [App::DocumentObjectGroupPython] G4_PLEXIGLASS  # scripted group (container) (typed FeaturePython)
  Dunit = g/cm3
  Dvalue = 1.19
  Group = -> [C_element083,H_element077,O_element079]
  conduct = 2
  density = 1
  expand = 3
  formula = G4_PLEXIGLASS
  name = G4_PLEXIGLASS
  specific = 4
FEATURE [App::DocumentObjectGroupPython] C_element084  label="C_element : 042"  # scripted group (container) (typed FeaturePython)
  n = 1
  ref = C_element
FEATURE [App::DocumentObjectGroupPython] H_element078  label="H_element : 040"  # scripted group (container) (typed FeaturePython)
  n = 2
  ref = H_element
FEATURE [App::DocumentObjectGroupPython] O_element080  label="O_element : 041"  # scripted group (container) (typed FeaturePython)
  n = 1
  ref = O_element
FEATURE [App::DocumentObjectGroupPython] G4_POLYOXYMETHYLENE  # scripted group (container) (typed FeaturePython)
  Dunit = g/cm3
  Dvalue = 1.425
  Group = -> [C_element084,H_element078,O_element080]
  conduct = 2
  density = 1
  expand = 3
  formula = G4_POLYOXYMETHYLENE
  name = G4_POLYOXYMETHYLENE
  specific = 4
FEATURE [App::DocumentObjectGroupPython] C_element085  label="C_element : 043"  # scripted group (container) (typed FeaturePython)
  n = 2
  ref = C_element
FEATURE [App::DocumentObjectGroupPython] H_element079  label="H_element : 041"  # scripted group (container) (typed FeaturePython)
  n = 4
  ref = H_element
FEATURE [App::DocumentObjectGroupPython] G4_POLYPROPYLENE  # scripted group (container) (typed FeaturePython)
  Dunit = g/cm3
  Dvalue = 0.9
  Group = -> [C_element085,H_element079]
  conduct = 2
  density = 1
  expand = 3
  formula = G4_POLYPROPYLENE
  name = G4_POLYPROPYLENE
  specific = 4
FEATURE [App::DocumentObjectGroupPython] C_element086  label="C_element : 044"  # scripted group (container) (typed FeaturePython)
  n = 8
  ref = C_element
FEATURE [App::DocumentObjectGroupPython] H_element080  label="H_element : 042"  # scripted group (container) (typed FeaturePython)
  n = 8
  ref = H_element
FEATURE [App::DocumentObjectGroupPython] G4_POLYSTYRENE  # scripted group (container) (typed FeaturePython)
  Dunit = g/cm3
  Dvalue = 1.06
  Group = -> [C_element086,H_element080]
  conduct = 2
  density = 1
  expand = 3
  formula = G4_POLYSTYRENE
  name = G4_POLYSTYRENE
  specific = 4
FEATURE [App::DocumentObjectGroupPython] C_element087  label="C_element : 045"  # scripted group (container) (typed FeaturePython)
  n = 2
  ref = C_element
FEATURE [App::DocumentObjectGroupPython] F_element014  label="F_element : 4"  # scripted group (container) (typed FeaturePython)
  n = 4
  ref = F_element
FEATURE [App::DocumentObjectGroupPython] G4_TEFLON  # scripted group (container) (typed FeaturePython)
  Dunit = g/cm3
  Dvalue = 2.2
  Group = -> [C_element087,F_element014]
  conduct = 2
  density = 1
  expand = 3
  formula = G4_TEFLON
  name = G4_TEFLON
  specific = 4
FEATURE [App::DocumentObjectGroupPython] C_element088  label="C_element : 046"  # scripted group (container) (typed FeaturePython)
  n = 2
  ref = C_element
FEATURE [App::DocumentObjectGroupPython] F_element015  label="F_element : 006"  # scripted group (container) (typed FeaturePython)
  n = 3
  ref = F_element
FEATURE [App::DocumentObjectGroupPython] Cl_element018  label="Cl_element : 008"  # scripted group (container) (typed FeaturePython)
  n = 1
  ref = Cl_element
FEATURE [App::DocumentObjectGroupPython] G4_POLYTRIFLUOROCHLOROETHYLENE  # scripted group (container) (typed FeaturePython)
  Dunit = g/cm3
  Dvalue = 2.1
  Group = -> [C_element088,F_element015,Cl_element018]
  conduct = 2
  density = 1
  expand = 3
  formula = G4_POLYTRIFLUOROCHLOROETHYLENE
  name = G4_POLYTRIFLUOROCHLOROETHYLENE
  specific = 4
FEATURE [App::DocumentObjectGroupPython] C_element089  label="C_element : 047"  # scripted group (container) (typed FeaturePython)
  n = 4
  ref = C_element
FEATURE [App::DocumentObjectGroupPython] H_element081  label="H_element : 043"  # scripted group (container) (typed FeaturePython)
  n = 6
  ref = H_element
FEATURE [App::DocumentObjectGroupPython] O_element081  label="O_element : 042"  # scripted group (container) (typed FeaturePython)
  n = 2
  ref = O_element
FEATURE [App::DocumentObjectGroupPython] G4_POLYVINYL_ACETATE  # scripted group (container) (typed FeaturePython)
  Dunit = g/cm3
  Dvalue = 1.19
  Group = -> [C_element089,H_element081,O_element081]
  conduct = 2
  density = 1
  expand = 3
  formula = G4_POLYVINYL_ACETATE
  name = G4_POLYVINYL_ACETATE
  specific = 4
FEATURE [App::DocumentObjectGroupPython] C_element090  label="C_element : 048"  # scripted group (container) (typed FeaturePython)
  n = 2
  ref = C_element
FEATURE [App::DocumentObjectGroupPython] H_element082  label="H_element : 044"  # scripted group (container) (typed FeaturePython)
  n = 4
  ref = H_element
FEATURE [App::DocumentObjectGroupPython] O_element082  label="O_element : 043"  # scripted group (container) (typed FeaturePython)
  n = 1
  ref = O_element
FEATURE [App::DocumentObjectGroupPython] G4_POLYVINYL_ALCOHOL  # scripted group (container) (typed FeaturePython)
  Dunit = g/cm3
  Dvalue = 1.3
  Group = -> [C_element090,H_element082,O_element082]
  conduct = 2
  density = 1
  expand = 3
  formula = G4_POLYVINYL_ALCOHOL
  name = G4_POLYVINYL_ALCOHOL
  specific = 4
FEATURE [App::DocumentObjectGroupPython] C_element091  label="C_element : 049"  # scripted group (container) (typed FeaturePython)
  n = 8
  ref = C_element
FEATURE [App::DocumentObjectGroupPython] H_element083  label="H_element : 045"  # scripted group (container) (typed FeaturePython)
  n = 14
  ref = H_element
FEATURE [App::DocumentObjectGroupPython] O_element083  label="O_element : 044"  # scripted group (container) (typed FeaturePython)
  n = 2
  ref = O_element
FEATURE [App::DocumentObjectGroupPython] G4_POLYVINYL_BUTYRAL  # scripted group (container) (typed FeaturePython)
  Dunit = g/cm3
  Dvalue = 1.12
  Group = -> [C_element091,H_element083,O_element083]
  conduct = 2
  density = 1
  expand = 3
  formula = G4_POLYVINYL_BUTYRAL
  name = G4_POLYVINYL_BUTYRAL
  specific = 4
FEATURE [App::DocumentObjectGroupPython] C_element092  label="C_element : 050"  # scripted group (container) (typed FeaturePython)
  n = 2
  ref = C_element
FEATURE [App::DocumentObjectGroupPython] H_element084  label="H_element : 046"  # scripted group (container) (typed FeaturePython)
  n = 3
  ref = H_element
FEATURE [App::DocumentObjectGroupPython] Cl_element019  label="Cl_element : 009"  # scripted group (container) (typed FeaturePython)
  n = 1
  ref = Cl_element
FEATURE [App::DocumentObjectGroupPython] G4_POLYVINYL_CHLORIDE  # scripted group (container) (typed FeaturePython)
  Dunit = g/cm3
  Dvalue = 1.3
  Group = -> [C_element092,H_element084,Cl_element019]
  conduct = 2
  density = 1
  expand = 3
  formula = G4_POLYVINYL_CHLORIDE
  name = G4_POLYVINYL_CHLORIDE
  specific = 4
FEATURE [App::DocumentObjectGroupPython] C_element093  label="C_element : 051"  # scripted group (container) (typed FeaturePython)
  n = 2
  ref = C_element
FEATURE [App::DocumentObjectGroupPython] H_element085  label="H_element : 047"  # scripted group (container) (typed FeaturePython)
  n = 2
  ref = H_element
FEATURE [App::DocumentObjectGroupPython] Cl_element020  label="Cl_element : 010"  # scripted group (container) (typed FeaturePython)
  n = 2
  ref = Cl_element
FEATURE [App::DocumentObjectGroupPython] G4_POLYVINYLIDENE_CHLORIDE  # scripted group (container) (typed FeaturePython)
  Dunit = g/cm3
  Dvalue = 1.7
  Group = -> [C_element093,H_element085,Cl_element020]
  conduct = 2
  density = 1
  expand = 3
  formula = G4_POLYVINYLIDENE_CHLORIDE
  name = G4_POLYVINYLIDENE_CHLORIDE
  specific = 4
FEATURE [App::DocumentObjectGroupPython] C_element094  label="C_element : 052"  # scripted group (container) (typed FeaturePython)
  n = 2
  ref = C_element
FEATURE [App::DocumentObjectGroupPython] H_element086  label="H_element : 048"  # scripted group (container) (typed FeaturePython)
  n = 2
  ref = H_element
FEATURE [App::DocumentObjectGroupPython] F_element016  label="F_element : 007"  # scripted group (container) (typed FeaturePython)
  n = 2
  ref = F_element
FEATURE [App::DocumentObjectGroupPython] G4_POLYVINYLIDENE_FLUORIDE  # scripted group (container) (typed FeaturePython)
  Dunit = g/cm3
  Dvalue = 1.76
  Group = -> [C_element094,H_element086,F_element016]
  conduct = 2
  density = 1
  expand = 3
  formula = G4_POLYVINYLIDENE_FLUORIDE
  name = G4_POLYVINYLIDENE_FLUORIDE
  specific = 4
FEATURE [App::DocumentObjectGroupPython] C_element095  label="C_element : 053"  # scripted group (container) (typed FeaturePython)
  n = 6
  ref = C_element
FEATURE [App::DocumentObjectGroupPython] H_element087  label="H_element : 9"  # scripted group (container) (typed FeaturePython)
  n = 9
  ref = H_element
FEATURE [App::DocumentObjectGroupPython] N_element037  label="N_element : 016"  # scripted group (container) (typed FeaturePython)
  n = 1
  ref = N_element
FEATURE [App::DocumentObjectGroupPython] O_element084  label="O_element : 045"  # scripted group (container) (typed FeaturePython)
  n = 1
  ref = O_element
FEATURE [App::DocumentObjectGroupPython] G4_POLYVINYL_PYRROLIDONE  # scripted group (container) (typed FeaturePython)
  Dunit = g/cm3
  Dvalue = 1.25
  Group = -> [C_element095,H_element087,N_element037,O_element084]
  conduct = 2
  density = 1
  expand = 3
  formula = G4_POLYVINYL_PYRROLIDONE
  name = G4_POLYVINYL_PYRROLIDONE
  specific = 4
FEATURE [App::DocumentObjectGroupPython] K_element008  label="K_element : 1"  # scripted group (container) (typed FeaturePython)
  n = 1
  ref = K_element
FEATURE [App::DocumentObjectGroupPython] I_element006  label="I_element : 003"  # scripted group (container) (typed FeaturePython)
  n = 1
  ref = I_element
FEATURE [App::DocumentObjectGroupPython] G4_POTASSIUM_IODIDE  # scripted group (container) (typed FeaturePython)
  Dunit = g/cm3
  Dvalue = 3.13
  Group = -> [K_element008,I_element006]
  conduct = 2
  density = 1
  expand = 3
  formula = G4_POTASSIUM_IODIDE
  name = G4_POTASSIUM_IODIDE
  specific = 4
FEATURE [App::DocumentObjectGroupPython] K_element009  label="K_element : 2"  # scripted group (container) (typed FeaturePython)
  n = 2
  ref = K_element
FEATURE [App::DocumentObjectGroupPython] O_element085  label="O_element : 046"  # scripted group (container) (typed FeaturePython)
  n = 1
  ref = O_element
FEATURE [App::DocumentObjectGroupPython] G4_POTASSIUM_OXIDE  # scripted group (container) (typed FeaturePython)
  Dunit = g/cm3
  Dvalue = 2.32
  Group = -> [K_element009,O_element085]
  conduct = 2
  density = 1
  expand = 3
  formula = G4_POTASSIUM_OXIDE
  name = G4_POTASSIUM_OXIDE
  specific = 4
FEATURE [App::DocumentObjectGroupPython] C_element096  label="C_element : 054"  # scripted group (container) (typed FeaturePython)
  n = 3
  ref = C_element
FEATURE [App::DocumentObjectGroupPython] H_element088  label="H_element : 049"  # scripted group (container) (typed FeaturePython)
  n = 8
  ref = H_element
FEATURE [App::DocumentObjectGroupPython] G4_PROPANE  # scripted group (container) (typed FeaturePython)
  Dunit = g/cm3
  Dvalue = 0.00187939
  Group = -> [C_element096,H_element088]
  conduct = 2
  density = 1
  expand = 3
  formula = G4_PROPANE
  name = G4_PROPANE
  specific = 4
FEATURE [App::DocumentObjectGroupPython] C_element097  label="C_element : 055"  # scripted group (container) (typed FeaturePython)
  n = 3
  ref = C_element
FEATURE [App::DocumentObjectGroupPython] H_element089  label="H_element : 050"  # scripted group (container) (typed FeaturePython)
  n = 8
  ref = H_element
FEATURE [App::DocumentObjectGroupPython] G4_lPROPANE  # scripted group (container) (typed FeaturePython)
  Dunit = g/cm3
  Dvalue = 0.43
  Group = -> [C_element097,H_element089]
  conduct = 2
  density = 1
  expand = 3
  formula = G4_lPROPANE
  name = G4_lPROPANE
  specific = 4
FEATURE [App::DocumentObjectGroupPython] C_element098  label="C_element : 056"  # scripted group (container) (typed FeaturePython)
  n = 3
  ref = C_element
FEATURE [App::DocumentObjectGroupPython] H_element090  label="H_element : 051"  # scripted group (container) (typed FeaturePython)
  n = 8
  ref = H_element
FEATURE [App::DocumentObjectGroupPython] O_element086  label="O_element : 047"  # scripted group (container) (typed FeaturePython)
  n = 1
  ref = O_element
FEATURE [App::DocumentObjectGroupPython] G4_N_PROPYL_ALCOHOL  label="G4_N-PROPYL_ALCOHOL"  # scripted group (container) (typed FeaturePython)
  Dunit = g/cm3
  Dvalue = 0.8035
  Group = -> [C_element098,H_element090,O_element086]
  conduct = 2
  density = 1
  expand = 3
  formula = G4_N-PROPYL_ALCOHOL
  name = G4_N-PROPYL_ALCOHOL
  specific = 4
FEATURE [App::DocumentObjectGroupPython] C_element099  label="C_element : 057"  # scripted group (container) (typed FeaturePython)
  n = 5
  ref = C_element
FEATURE [App::DocumentObjectGroupPython] H_element091  label="H_element : 052"  # scripted group (container) (typed FeaturePython)
  n = 5
  ref = H_element
FEATURE [App::DocumentObjectGroupPython] N_element038  label="N_element : 017"  # scripted group (container) (typed FeaturePython)
  n = 1
  ref = N_element
FEATURE [App::DocumentObjectGroupPython] G4_PYRIDINE  # scripted group (container) (typed FeaturePython)
  Dunit = g/cm3
  Dvalue = 0.9819
  Group = -> [C_element099,H_element091,N_element038]
  conduct = 2
  density = 1
  expand = 3
  formula = G4_PYRIDINE
  name = G4_PYRIDINE
  specific = 4
FEATURE [App::DocumentObjectGroupPython] H_element092  label="H_element : 0.144"  # scripted group (container) (typed FeaturePython)
  n = 0.143711
FEATURE [App::DocumentObjectGroupPython] C_element100  label="C_element : 0.856"  # scripted group (container) (typed FeaturePython)
  n = 0.856289
FEATURE [App::DocumentObjectGroupPython] G4_RUBBER_BUTYL  # scripted group (container) (typed FeaturePython)
  Dunit = g/cm3
  Dvalue = 0.92
  Group = -> [H_element092,C_element100]
  conduct = 2
  density = 1
  expand = 3
  formula = G4_RUBBER_BUTYL
  name = G4_RUBBER_BUTYL
  specific = 4
FEATURE [App::DocumentObjectGroupPython] H_element093  label="H_element : 0.118"  # scripted group (container) (typed FeaturePython)
  n = 0.118371
FEATURE [App::DocumentObjectGroupPython] C_element101  label="C_element : 0.882"  # scripted group (container) (typed FeaturePython)
  n = 0.881629
FEATURE [App::DocumentObjectGroupPython] G4_RUBBER_NATURAL  # scripted group (container) (typed FeaturePython)
  Dunit = g/cm3
  Dvalue = 0.92
  Group = -> [H_element093,C_element101]
  conduct = 2
  density = 1
  expand = 3
  formula = G4_RUBBER_NATURAL
  name = G4_RUBBER_NATURAL
  specific = 4
FEATURE [App::DocumentObjectGroupPython] H_element094  label="H_element : 0.145"  # scripted group (container) (typed FeaturePython)
  n = 0.05692
FEATURE [App::DocumentObjectGroupPython] C_element102  label="C_element : 0.543"  # scripted group (container) (typed FeaturePython)
  n = 0.542646
FEATURE [App::DocumentObjectGroupPython] Cl_element021  label="Cl_element : 0.400"  # scripted group (container) (typed FeaturePython)
  n = 0.400434
FEATURE [App::DocumentObjectGroupPython] G4_RUBBER_NEOPRENE  # scripted group (container) (typed FeaturePython)
  Dunit = g/cm3
  Dvalue = 1.23
  Group = -> [H_element094,C_element102,Cl_element021]
  conduct = 2
  density = 1
  expand = 3
  formula = G4_RUBBER_NEOPRENE
  name = G4_RUBBER_NEOPRENE
  specific = 4
FEATURE [App::DocumentObjectGroupPython] Si_element006  label="Si_element : 1"  # scripted group (container) (typed FeaturePython)
  n = 1
  ref = Si_element
FEATURE [App::DocumentObjectGroupPython] O_element087  label="O_element : 048"  # scripted group (container) (typed FeaturePython)
  n = 2
  ref = O_element
FEATURE [App::DocumentObjectGroupPython] G4_SILICON_DIOXIDE002  label="G4_SILICON_DIOXIDE"  # scripted group (container) (typed FeaturePython)
  Dunit = g/cm3
  Dvalue = 2.32
  Group = -> [Si_element006,O_element087]
  conduct = 2
  density = 1
  expand = 3
  formula = G4_SILICON_DIOXIDE
  name = G4_SILICON_DIOXIDE
  specific = 4
FEATURE [App::DocumentObjectGroupPython] Ag_element002  label="Ag_element : 1"  # scripted group (container) (typed FeaturePython)
  n = 1
  ref = Ag_element
FEATURE [App::DocumentObjectGroupPython] Br_element005  label="Br_element : 003"  # scripted group (container) (typed FeaturePython)
  n = 1
  ref = Br_element
FEATURE [App::DocumentObjectGroupPython] G4_SILVER_BROMIDE  # scripted group (container) (typed FeaturePython)
  Dunit = g/cm3
  Dvalue = 6.473
  Group = -> [Ag_element002,Br_element005]
  conduct = 2
  density = 1
  expand = 3
  formula = G4_SILVER_BROMIDE
  name = G4_SILVER_BROMIDE
  specific = 4
FEATURE [App::DocumentObjectGroupPython] Ag_element003  label="Ag_element : 002"  # scripted group (container) (typed FeaturePython)
  n = 1
  ref = Ag_element
FEATURE [App::DocumentObjectGroupPython] Cl_element022  label="Cl_element : 011"  # scripted group (container) (typed FeaturePython)
  n = 1
  ref = Cl_element
FEATURE [App::DocumentObjectGroupPython] G4_SILVER_CHLORIDE  # scripted group (container) (typed FeaturePython)
  Dunit = g/cm3
  Dvalue = 5.56
  Group = -> [Ag_element003,Cl_element022]
  conduct = 2
  density = 1
  expand = 3
  formula = G4_SILVER_CHLORIDE
  name = G4_SILVER_CHLORIDE
  specific = 4
FEATURE [App::DocumentObjectGroupPython] Br_element006  label="Br_element : 0.423"  # scripted group (container) (typed FeaturePython)
  n = 0.422895
FEATURE [App::DocumentObjectGroupPython] Ag_element004  label="Ag_element : 0.574"  # scripted group (container) (typed FeaturePython)
  n = 0.573748
FEATURE [App::DocumentObjectGroupPython] I_element007  label="I_element : 0.649"  # scripted group (container) (typed FeaturePython)
  n = 0.003357
FEATURE [App::DocumentObjectGroupPython] G4_SILVER_HALIDES  # scripted group (container) (typed FeaturePython)
  Dunit = g/cm3
  Dvalue = 6.47
  Group = -> [Br_element006,Ag_element004,I_element007]
  conduct = 2
  density = 1
  expand = 3
  formula = G4_SILVER_HALIDES
  name = G4_SILVER_HALIDES
  specific = 4
FEATURE [App::DocumentObjectGroupPython] Ag_element005  label="Ag_element : 003"  # scripted group (container) (typed FeaturePython)
  n = 1
  ref = Ag_element
FEATURE [App::DocumentObjectGroupPython] I_element008  label="I_element : 004"  # scripted group (container) (typed FeaturePython)
  n = 1
  ref = I_element
FEATURE [App::DocumentObjectGroupPython] G4_SILVER_IODIDE  # scripted group (container) (typed FeaturePython)
  Dunit = g/cm3
  Dvalue = 6.01
  Group = -> [Ag_element005,I_element008]
  conduct = 2
  density = 1
  expand = 3
  formula = G4_SILVER_IODIDE
  name = G4_SILVER_IODIDE
  specific = 4
FEATURE [App::DocumentObjectGroupPython] H_element095  label="H_element : 0.100"  # scripted group (container) (typed FeaturePython)
  n = 0.1
FEATURE [App::DocumentObjectGroupPython] C_element103  label="C_element : 0.204"  # scripted group (container) (typed FeaturePython)
  n = 0.204
FEATURE [App::DocumentObjectGroupPython] N_element039  label="N_element : 0.759"  # scripted group (container) (typed FeaturePython)
  n = 0.042
FEATURE [App::DocumentObjectGroupPython] O_element088  label="O_element : 0.645"  # scripted group (container) (typed FeaturePython)
  n = 0.645
FEATURE [App::DocumentObjectGroupPython] Na_element013  label="Na_element : 0.100"  # scripted group (container) (typed FeaturePython)
  n = 0.002
FEATURE [App::DocumentObjectGroupPython] P_element009  label="P_element : 0.107"  # scripted group (container) (typed FeaturePython)
  n = 0.001
FEATURE [App::DocumentObjectGroupPython] S_element020  label="S_element : 0.021"  # scripted group (container) (typed FeaturePython)
  n = 0.002
FEATURE [App::DocumentObjectGroupPython] Cl_element023  label="Cl_element : 0.590"  # scripted group (container) (typed FeaturePython)
  n = 0.003
FEATURE [App::DocumentObjectGroupPython] K_element010  label="K_element : 0.001"  # scripted group (container) (typed FeaturePython)
  n = 0.001
FEATURE [App::DocumentObjectGroupPython] G4_SKIN_ICRP  # scripted group (container) (typed FeaturePython)
  Dunit = g/cm3
  Dvalue = 1.09
  Group = -> [H_element095,C_element103,N_element039,O_element088,Na_element013,P_element009,S_element020,Cl_element023,K_element010]
  conduct = 2
  density = 1
  expand = 3
  formula = G4_SKIN_ICRP
  name = G4_SKIN_ICRP
  specific = 4
FEATURE [App::DocumentObjectGroupPython] Na_element014  label="Na_element : 2"  # scripted group (container) (typed FeaturePython)
  n = 2
  ref = Na_element
FEATURE [App::DocumentObjectGroupPython] C_element104  label="C_element : 058"  # scripted group (container) (typed FeaturePython)
  n = 1
  ref = C_element
FEATURE [App::DocumentObjectGroupPython] O_element089  label="O_element : 049"  # scripted group (container) (typed FeaturePython)
  n = 3
  ref = O_element
FEATURE [App::DocumentObjectGroupPython] G4_SODIUM_CARBONATE  # scripted group (container) (typed FeaturePython)
  Dunit = g/cm3
  Dvalue = 2.532
  Group = -> [Na_element014,C_element104,O_element089]
  conduct = 2
  density = 1
  expand = 3
  formula = G4_SODIUM_CARBONATE
  name = G4_SODIUM_CARBONATE
  specific = 4
FEATURE [App::DocumentObjectGroupPython] Na_element015  label="Na_element : 1"  # scripted group (container) (typed FeaturePython)
  n = 1
  ref = Na_element
FEATURE [App::DocumentObjectGroupPython] I_element009  label="I_element : 005"  # scripted group (container) (typed FeaturePython)
  n = 1
  ref = I_element
FEATURE [App::DocumentObjectGroupPython] G4_SODIUM_IODIDE  # scripted group (container) (typed FeaturePython)
  Dunit = g/cm3
  Dvalue = 3.667
  Group = -> [Na_element015,I_element009]
  conduct = 2
  density = 1
  expand = 3
  formula = G4_SODIUM_IODIDE
  name = G4_SODIUM_IODIDE
  specific = 4
FEATURE [App::DocumentObjectGroupPython] Na_element016  label="Na_element : 003"  # scripted group (container) (typed FeaturePython)
  n = 2
  ref = Na_element
FEATURE [App::DocumentObjectGroupPython] O_element090  label="O_element : 050"  # scripted group (container) (typed FeaturePython)
  n = 1
  ref = O_element
FEATURE [App::DocumentObjectGroupPython] G4_SODIUM_MONOXIDE  # scripted group (container) (typed FeaturePython)
  Dunit = g/cm3
  Dvalue = 2.27
  Group = -> [Na_element016,O_element090]
  conduct = 2
  density = 1
  expand = 3
  formula = G4_SODIUM_MONOXIDE
  name = G4_SODIUM_MONOXIDE
  specific = 4
FEATURE [App::DocumentObjectGroupPython] Na_element017  label="Na_element : 004"  # scripted group (container) (typed FeaturePython)
  n = 1
  ref = Na_element
FEATURE [App::DocumentObjectGroupPython] N_element040  label="N_element : 018"  # scripted group (container) (typed FeaturePython)
  n = 1
  ref = N_element
FEATURE [App::DocumentObjectGroupPython] O_element091  label="O_element : 051"  # scripted group (container) (typed FeaturePython)
  n = 3
  ref = O_element
FEATURE [App::DocumentObjectGroupPython] G4_SODIUM_NITRATE  # scripted group (container) (typed FeaturePython)
  Dunit = g/cm3
  Dvalue = 2.261
  Group = -> [Na_element017,N_element040,O_element091]
  conduct = 2
  density = 1
  expand = 3
  formula = G4_SODIUM_NITRATE
  name = G4_SODIUM_NITRATE
  specific = 4
FEATURE [App::DocumentObjectGroupPython] C_element105  label="C_element : 059"  # scripted group (container) (typed FeaturePython)
  n = 14
  ref = C_element
FEATURE [App::DocumentObjectGroupPython] H_element096  label="H_element : 053"  # scripted group (container) (typed FeaturePython)
  n = 12
  ref = H_element
FEATURE [App::DocumentObjectGroupPython] G4_STILBENE  # scripted group (container) (typed FeaturePython)
  Dunit = g/cm3
  Dvalue = 0.9707
  Group = -> [C_element105,H_element096]
  conduct = 2
  density = 1
  expand = 3
  formula = G4_STILBENE
  name = G4_STILBENE
  specific = 4
FEATURE [App::DocumentObjectGroupPython] C_element106  label="C_element : 12"  # scripted group (container) (typed FeaturePython)
  n = 12
  ref = C_element
FEATURE [App::DocumentObjectGroupPython] H_element097  label="H_element : 22"  # scripted group (container) (typed FeaturePython)
  n = 22
  ref = H_element
FEATURE [App::DocumentObjectGroupPython] O_element092  label="O_element : 11"  # scripted group (container) (typed FeaturePython)
  n = 11
  ref = O_element
FEATURE [App::DocumentObjectGroupPython] G4_SUCROSE  # scripted group (container) (typed FeaturePython)
  Dunit = g/cm3
  Dvalue = 1.5805
  Group = -> [C_element106,H_element097,O_element092]
  conduct = 2
  density = 1
  expand = 3
  formula = G4_SUCROSE
  name = G4_SUCROSE
  specific = 4
FEATURE [App::DocumentObjectGroupPython] C_element107  label="C_element : 18"  # scripted group (container) (typed FeaturePython)
  n = 18
  ref = C_element
FEATURE [App::DocumentObjectGroupPython] H_element098  label="H_element : 054"  # scripted group (container) (typed FeaturePython)
  n = 14
  ref = H_element
FEATURE [App::DocumentObjectGroupPython] G4_TERPHENYL  # scripted group (container) (typed FeaturePython)
  Dunit = g/cm3
  Dvalue = 1.24
  Group = -> [C_element107,H_element098]
  conduct = 2
  density = 1
  expand = 3
  formula = G4_TERPHENYL
  name = G4_TERPHENYL
  specific = 4
FEATURE [App::DocumentObjectGroupPython] H_element099  label="H_element : 0.146"  # scripted group (container) (typed FeaturePython)
  n = 0.106
FEATURE [App::DocumentObjectGroupPython] C_element108  label="C_element : 0.883"  # scripted group (container) (typed FeaturePython)
  n = 0.099
FEATURE [App::DocumentObjectGroupPython] N_element041  label="N_element : 0.020"  # scripted group (container) (typed FeaturePython)
  n = 0.02
FEATURE [App::DocumentObjectGroupPython] O_element093  label="O_element : 0.766"  # scripted group (container) (typed FeaturePython)
  n = 0.766
FEATURE [App::DocumentObjectGroupPython] Na_element018  label="Na_element : 0.101"  # scripted group (container) (typed FeaturePython)
  n = 0.002
FEATURE [App::DocumentObjectGroupPython] P_element010  label="P_element : 0.108"  # scripted group (container) (typed FeaturePython)
  n = 0.001
FEATURE [App::DocumentObjectGroupPython] S_element021  label="S_element : 0.022"  # scripted group (container) (typed FeaturePython)
  n = 0.002
FEATURE [App::DocumentObjectGroupPython] Cl_element024  label="Cl_element : 0.002"  # scripted group (container) (typed FeaturePython)
  n = 0.002
FEATURE [App::DocumentObjectGroupPython] K_element011  label="K_element : 0.017"  # scripted group (container) (typed FeaturePython)
  n = 0.002
FEATURE [App::DocumentObjectGroupPython] G4_TESTIS_ICRP  # scripted group (container) (typed FeaturePython)
  Dunit = g/cm3
  Dvalue = 1.04
  Group = -> [H_element099,C_element108,N_element041,O_element093,Na_element018,P_element010,S_element021,Cl_element024,K_element011]
  conduct = 2
  density = 1
  expand = 3
  formula = G4_TESTIS_ICRP
  name = G4_TESTIS_ICRP
  specific = 4
FEATURE [App::DocumentObjectGroupPython] C_element109  label="C_element : 060"  # scripted group (container) (typed FeaturePython)
  n = 2
  ref = C_element
FEATURE [App::DocumentObjectGroupPython] Cl_element025  label="Cl_element : 012"  # scripted group (container) (typed FeaturePython)
  n = 4
  ref = Cl_element
FEATURE [App::DocumentObjectGroupPython] G4_TETRACHLOROETHYLENE  # scripted group (container) (typed FeaturePython)
  Dunit = g/cm3
  Dvalue = 1.625
  Group = -> [C_element109,Cl_element025]
  conduct = 2
  density = 1
  expand = 3
  formula = G4_TETRACHLOROETHYLENE
  name = G4_TETRACHLOROETHYLENE
  specific = 4
FEATURE [App::DocumentObjectGroupPython] Tl_element001  label="Tl_element : 1"  # scripted group (container) (typed FeaturePython)
  n = 1
  ref = Tl_element
FEATURE [App::DocumentObjectGroupPython] Cl_element026  label="Cl_element : 013"  # scripted group (container) (typed FeaturePython)
  n = 1
  ref = Cl_element
FEATURE [App::DocumentObjectGroupPython] G4_THALLIUM_CHLORIDE  # scripted group (container) (typed FeaturePython)
  Dunit = g/cm3
  Dvalue = 7.004
  Group = -> [Tl_element001,Cl_element026]
  conduct = 2
  density = 1
  expand = 3
  formula = G4_THALLIUM_CHLORIDE
  name = G4_THALLIUM_CHLORIDE
  specific = 4
FEATURE [App::DocumentObjectGroupPython] H_element100  label="H_element : 0.147"  # scripted group (container) (typed FeaturePython)
  n = 0.105
FEATURE [App::DocumentObjectGroupPython] C_element110  label="C_element : 0.256"  # scripted group (container) (typed FeaturePython)
  n = 0.256
FEATURE [App::DocumentObjectGroupPython] N_element042  label="N_element : 0.760"  # scripted group (container) (typed FeaturePython)
  n = 0.027
FEATURE [App::DocumentObjectGroupPython] O_element094  label="O_element : 0.602"  # scripted group (container) (typed FeaturePython)
  n = 0.602
FEATURE [App::DocumentObjectGroupPython] Na_element019  label="Na_element : 0.102"  # scripted group (container) (typed FeaturePython)
  n = 0.001
FEATURE [App::DocumentObjectGroupPython] P_element011  label="P_element : 0.109"  # scripted group (container) (typed FeaturePython)
  n = 0.002
FEATURE [App::DocumentObjectGroupPython] S_element022  label="S_element : 0.023"  # scripted group (container) (typed FeaturePython)
  n = 0.003
FEATURE [App::DocumentObjectGroupPython] Cl_element027  label="Cl_element : 0.591"  # scripted group (container) (typed FeaturePython)
  n = 0.002
FEATURE [App::DocumentObjectGroupPython] K_element012  label="K_element : 0.018"  # scripted group (container) (typed FeaturePython)
  n = 0.002
FEATURE [App::DocumentObjectGroupPython] G4_TISSUE_SOFT_ICRP  # scripted group (container) (typed FeaturePython)
  Dunit = g/cm3
  Dvalue = 1.03
  Group = -> [H_element100,C_element110,N_element042,O_element094,Na_element019,P_element011,S_element022,Cl_element027,K_element012]
  conduct = 2
  density = 1
  expand = 3
  formula = G4_TISSUE_SOFT_ICRP
  name = G4_TISSUE_SOFT_ICRP
  specific = 4
FEATURE [App::DocumentObjectGroupPython] H_element101  label="H_element : 0.148"  # scripted group (container) (typed FeaturePython)
  n = 0.101
FEATURE [App::DocumentObjectGroupPython] C_element111  label="C_element : 0.111"  # scripted group (container) (typed FeaturePython)
  n = 0.111
FEATURE [App::DocumentObjectGroupPython] N_element043  label="N_element : 0.026"  # scripted group (container) (typed FeaturePython)
  n = 0.026
FEATURE [App::DocumentObjectGroupPython] O_element095  label="O_element : 0.762"  # scripted group (container) (typed FeaturePython)
  n = 0.762
FEATURE [App::DocumentObjectGroupPython] G4_TISSUE_SOFT_ICRU_4  label="G4_TISSUE_SOFT_ICRU-4"  # scripted group (container) (typed FeaturePython)
  Dunit = g/cm3
  Dvalue = 1
  Group = -> [H_element101,C_element111,N_element043,O_element095]
  conduct = 2
  density = 1
  expand = 3
  formula = G4_TISSUE_SOFT_ICRU-4
  name = G4_TISSUE_SOFT_ICRU-4
  specific = 4
FEATURE [App::DocumentObjectGroupPython] H_element102  label="H_element : 0.149"  # scripted group (container) (typed FeaturePython)
  n = 0.101869
FEATURE [App::DocumentObjectGroupPython] C_element112  label="C_element : 0.456"  # scripted group (container) (typed FeaturePython)
  n = 0.456179
FEATURE [App::DocumentObjectGroupPython] N_element044  label="N_element : 0.761"  # scripted group (container) (typed FeaturePython)
  n = 0.035172
FEATURE [App::DocumentObjectGroupPython] O_element096  label="O_element : 0.407"  # scripted group (container) (typed FeaturePython)
  n = 0.40678
FEATURE [App::DocumentObjectGroupPython] G4_TISSUE_METHANE  label="G4_TISSUE-METHANE"  # scripted group (container) (typed FeaturePython)
  Dunit = g/cm3
  Dvalue = 0.00106409
  Group = -> [H_element102,C_element112,N_element044,O_element096]
  conduct = 2
  density = 1
  expand = 3
  formula = G4_TISSUE-METHANE
  name = G4_TISSUE-METHANE
  specific = 4
FEATURE [App::DocumentObjectGroupPython] H_element103  label="H_element : 0.103"  # scripted group (container) (typed FeaturePython)
  n = 0.102672
FEATURE [App::DocumentObjectGroupPython] C_element113  label="C_element : 0.569"  # scripted group (container) (typed FeaturePython)
  n = 0.56894
FEATURE [App::DocumentObjectGroupPython] N_element045  label="N_element : 0.762"  # scripted group (container) (typed FeaturePython)
  n = 0.035022
FEATURE [App::DocumentObjectGroupPython] O_element097  label="O_element : 0.293"  # scripted group (container) (typed FeaturePython)
  n = 0.293366
FEATURE [App::DocumentObjectGroupPython] G4_TISSUE_PROPANE  label="G4_TISSUE-PROPANE"  # scripted group (container) (typed FeaturePython)
  Dunit = g/cm3
  Dvalue = 0.00182628
  Group = -> [H_element103,C_element113,N_element045,O_element097]
  conduct = 2
  density = 1
  expand = 3
  formula = G4_TISSUE-PROPANE
  name = G4_TISSUE-PROPANE
  specific = 4
FEATURE [App::DocumentObjectGroupPython] Ti_element003  label="Ti_element : 1"  # scripted group (container) (typed FeaturePython)
  n = 1
  ref = Ti_element
FEATURE [App::DocumentObjectGroupPython] O_element098  label="O_element : 052"  # scripted group (container) (typed FeaturePython)
  n = 2
  ref = O_element
FEATURE [App::DocumentObjectGroupPython] G4_TITANIUM_DIOXIDE  # scripted group (container) (typed FeaturePython)
  Dunit = g/cm3
  Dvalue = 4.26
  Group = -> [Ti_element003,O_element098]
  conduct = 2
  density = 1
  expand = 3
  formula = G4_TITANIUM_DIOXIDE
  name = G4_TITANIUM_DIOXIDE
  specific = 4
FEATURE [App::DocumentObjectGroupPython] C_element114  label="C_element : 061"  # scripted group (container) (typed FeaturePython)
  n = 7
  ref = C_element
FEATURE [App::DocumentObjectGroupPython] H_element104  label="H_element : 055"  # scripted group (container) (typed FeaturePython)
  n = 8
  ref = H_element
FEATURE [App::DocumentObjectGroupPython] G4_TOLUENE  # scripted group (container) (typed FeaturePython)
  Dunit = g/cm3
  Dvalue = 0.8669
  Group = -> [C_element114,H_element104]
  conduct = 2
  density = 1
  expand = 3
  formula = G4_TOLUENE
  name = G4_TOLUENE
  specific = 4
FEATURE [App::DocumentObjectGroupPython] C_element115  label="C_element : 062"  # scripted group (container) (typed FeaturePython)
  n = 2
  ref = C_element
FEATURE [App::DocumentObjectGroupPython] H_element105  label="H_element : 056"  # scripted group (container) (typed FeaturePython)
  n = 1
  ref = H_element
FEATURE [App::DocumentObjectGroupPython] Cl_element028  label="Cl_element : 014"  # scripted group (container) (typed FeaturePython)
  n = 3
  ref = Cl_element
FEATURE [App::DocumentObjectGroupPython] G4_TRICHLOROETHYLENE  # scripted group (container) (typed FeaturePython)
  Dunit = g/cm3
  Dvalue = 1.46
  Group = -> [C_element115,H_element105,Cl_element028]
  conduct = 2
  density = 1
  expand = 3
  formula = G4_TRICHLOROETHYLENE
  name = G4_TRICHLOROETHYLENE
  specific = 4
FEATURE [App::DocumentObjectGroupPython] C_element116  label="C_element : 063"  # scripted group (container) (typed FeaturePython)
  n = 6
  ref = C_element
FEATURE [App::DocumentObjectGroupPython] H_element106  label="H_element : 15"  # scripted group (container) (typed FeaturePython)
  n = 15
  ref = H_element
FEATURE [App::DocumentObjectGroupPython] O_element099  label="O_element : 053"  # scripted group (container) (typed FeaturePython)
  n = 4
  ref = O_element
FEATURE [App::DocumentObjectGroupPython] P_element012  label="P_element : 1"  # scripted group (container) (typed FeaturePython)
  n = 1
  ref = P_element
FEATURE [App::DocumentObjectGroupPython] G4_TRIETHYL_PHOSPHATE  # scripted group (container) (typed FeaturePython)
  Dunit = g/cm3
  Dvalue = 1.07
  Group = -> [C_element116,H_element106,O_element099,P_element012]
  conduct = 2
  density = 1
  expand = 3
  formula = G4_TRIETHYL_PHOSPHATE
  name = G4_TRIETHYL_PHOSPHATE
  specific = 4
FEATURE [App::DocumentObjectGroupPython] W_element003  label="W_element : 003"  # scripted group (container) (typed FeaturePython)
  n = 1
  ref = W_element
FEATURE [App::DocumentObjectGroupPython] F_element017  label="F_element : 6"  # scripted group (container) (typed FeaturePython)
  n = 6
  ref = F_element
FEATURE [App::DocumentObjectGroupPython] G4_TUNGSTEN_HEXAFLUORIDE  # scripted group (container) (typed FeaturePython)
  Dunit = g/cm3
  Dvalue = 2.4
  Group = -> [W_element003,F_element017]
  conduct = 2
  density = 1
  expand = 3
  formula = G4_TUNGSTEN_HEXAFLUORIDE
  name = G4_TUNGSTEN_HEXAFLUORIDE
  specific = 4
FEATURE [App::DocumentObjectGroupPython] U_element001  label="U_element : 1"  # scripted group (container) (typed FeaturePython)
  n = 1
  ref = U_element
FEATURE [App::DocumentObjectGroupPython] C_element117  label="C_element : 064"  # scripted group (container) (typed FeaturePython)
  n = 2
  ref = C_element
FEATURE [App::DocumentObjectGroupPython] G4_URANIUM_DICARBIDE  # scripted group (container) (typed FeaturePython)
  Dunit = g/cm3
  Dvalue = 11.28
  Group = -> [U_element001,C_element117]
  conduct = 2
  density = 1
  expand = 3
  formula = G4_URANIUM_DICARBIDE
  name = G4_URANIUM_DICARBIDE
  specific = 4
FEATURE [App::DocumentObjectGroupPython] U_element002  label="U_element : 002"  # scripted group (container) (typed FeaturePython)
  n = 1
  ref = U_element
FEATURE [App::DocumentObjectGroupPython] C_element118  label="C_element : 065"  # scripted group (container) (typed FeaturePython)
  n = 1
  ref = C_element
FEATURE [App::DocumentObjectGroupPython] G4_URANIUM_MONOCARBIDE  # scripted group (container) (typed FeaturePython)
  Dunit = g/cm3
  Dvalue = 13.63
  Group = -> [U_element002,C_element118]
  conduct = 2
  density = 1
  expand = 3
  formula = G4_URANIUM_MONOCARBIDE
  name = G4_URANIUM_MONOCARBIDE
  specific = 4
FEATURE [App::DocumentObjectGroupPython] U_element003  label="U_element : 003"  # scripted group (container) (typed FeaturePython)
  n = 1
  ref = U_element
FEATURE [App::DocumentObjectGroupPython] O_element100  label="O_element : 054"  # scripted group (container) (typed FeaturePython)
  n = 2
  ref = O_element
FEATURE [App::DocumentObjectGroupPython] G4_URANIUM_OXIDE  # scripted group (container) (typed FeaturePython)
  Dunit = g/cm3
  Dvalue = 10.96
  Group = -> [U_element003,O_element100]
  conduct = 2
  density = 1
  expand = 3
  formula = G4_URANIUM_OXIDE
  name = G4_URANIUM_OXIDE
  specific = 4
FEATURE [App::DocumentObjectGroupPython] C_element119  label="C_element : 066"  # scripted group (container) (typed FeaturePython)
  n = 1
  ref = C_element
FEATURE [App::DocumentObjectGroupPython] H_element107  label="H_element : 057"  # scripted group (container) (typed FeaturePython)
  n = 4
  ref = H_element
FEATURE [App::DocumentObjectGroupPython] N_element046  label="N_element : 019"  # scripted group (container) (typed FeaturePython)
  n = 2
  ref = N_element
FEATURE [App::DocumentObjectGroupPython] O_element101  label="O_element : 055"  # scripted group (container) (typed FeaturePython)
  n = 1
  ref = O_element
FEATURE [App::DocumentObjectGroupPython] G4_UREA  # scripted group (container) (typed FeaturePython)
  Dunit = g/cm3
  Dvalue = 1.323
  Group = -> [C_element119,H_element107,N_element046,O_element101]
  conduct = 2
  density = 1
  expand = 3
  formula = G4_UREA
  name = G4_UREA
  specific = 4
FEATURE [App::DocumentObjectGroupPython] C_element120  label="C_element : 067"  # scripted group (container) (typed FeaturePython)
  n = 5
  ref = C_element
FEATURE [App::DocumentObjectGroupPython] H_element108  label="H_element : 058"  # scripted group (container) (typed FeaturePython)
  n = 11
  ref = H_element
FEATURE [App::DocumentObjectGroupPython] N_element047  label="N_element : 020"  # scripted group (container) (typed FeaturePython)
  n = 1
  ref = N_element
FEATURE [App::DocumentObjectGroupPython] O_element102  label="O_element : 056"  # scripted group (container) (typed FeaturePython)
  n = 2
  ref = O_element
FEATURE [App::DocumentObjectGroupPython] G4_VALINE  # scripted group (container) (typed FeaturePython)
  Dunit = g/cm3
  Dvalue = 1.23
  Group = -> [C_element120,H_element108,N_element047,O_element102]
  conduct = 2
  density = 1
  expand = 3
  formula = G4_VALINE
  name = G4_VALINE
  specific = 4
FEATURE [App::DocumentObjectGroupPython] H_element109  label="H_element : 0.009"  # scripted group (container) (typed FeaturePython)
  n = 0.009417
FEATURE [App::DocumentObjectGroupPython] C_element121  label="C_element : 0.281"  # scripted group (container) (typed FeaturePython)
  n = 0.280555
FEATURE [App::DocumentObjectGroupPython] F_element018  label="F_element : 0.710"  # scripted group (container) (typed FeaturePython)
  n = 0.710028
FEATURE [App::DocumentObjectGroupPython] G4_VITON  # scripted group (container) (typed FeaturePython)
  Dunit = g/cm3
  Dvalue = 1.8
  Group = -> [H_element109,C_element121,F_element018]
  conduct = 2
  density = 1
  expand = 3
  formula = G4_VITON
  name = G4_VITON
  specific = 4
FEATURE [App::DocumentObjectGroupPython] H_element110  label="H_element : 059"  # scripted group (container) (typed FeaturePython)
  n = 2
  ref = H_element
FEATURE [App::DocumentObjectGroupPython] O_element103  label="O_element : 057"  # scripted group (container) (typed FeaturePython)
  n = 1
  ref = O_element
FEATURE [App::DocumentObjectGroupPython] G4_WATER  # scripted group (container) (typed FeaturePython)
  Dunit = g/cm3
  Dvalue = 1
  Group = -> [H_element110,O_element103]
  conduct = 2
  density = 1
  expand = 3
  formula = G4_WATER
  name = G4_WATER
  specific = 4
FEATURE [App::DocumentObjectGroupPython] H_element111  label="H_element : 060"  # scripted group (container) (typed FeaturePython)
  n = 2
  ref = H_element
FEATURE [App::DocumentObjectGroupPython] O_element104  label="O_element : 058"  # scripted group (container) (typed FeaturePython)
  n = 1
  ref = O_element
FEATURE [App::DocumentObjectGroupPython] G4_WATER_VAPOR  # scripted group (container) (typed FeaturePython)
  Dunit = g/cm3
  Dvalue = 0.000756182
  Group = -> [H_element111,O_element104]
  conduct = 2
  density = 1
  expand = 3
  formula = G4_WATER_VAPOR
  name = G4_WATER_VAPOR
  specific = 4
FEATURE [App::DocumentObjectGroupPython] C_element122  label="C_element : 068"  # scripted group (container) (typed FeaturePython)
  n = 8
  ref = C_element
FEATURE [App::DocumentObjectGroupPython] H_element112  label="H_element : 061"  # scripted group (container) (typed FeaturePython)
  n = 10
  ref = H_element
FEATURE [App::DocumentObjectGroupPython] G4_XYLENE  # scripted group (container) (typed FeaturePython)
  Dunit = g/cm3
  Dvalue = 0.87
  Group = -> [C_element122,H_element112]
  conduct = 2
  density = 1
  expand = 3
  formula = G4_XYLENE
  name = G4_XYLENE
  specific = 4
FEATURE [App::DocumentObjectGroupPython] C_element123  label="C_element : 069"  # scripted group (container) (typed FeaturePython)
  n = 1
  ref = C_element
FEATURE [App::DocumentObjectGroupPython] G4_GRAPHITE  # scripted group (container) (typed FeaturePython)
  Dunit = g/cm3
  Dvalue = 2.21
  Group = -> [C_element123]
  conduct = 2
  density = 1
  expand = 3
  formula = G4_GRAPHITE
  name = G4_GRAPHITE
  specific = 4
FEATURE [App::DocumentObjectGroupPython] NIST  # scripted group (container) (typed FeaturePython)
  Group = -> [G4_A_150_TISSUE,G4_ACETONE,G4_ACETYLENE,G4_ADENINE,G4_ADIPOSE_TISSUE_ICRP,G4_AIR001,G4_ALANINE,G4_ALUMINUM_OXIDE,G4_AMBER,G4_AMMONIA,G4_ANILINE,G4_ANTHRACENE,G4_B_100_BONE,G4_BAKELITE,G4_BARIUM_FLUORIDE,G4_BARIUM_SULFATE,G4_BENZENE,G4_BERYLLIUM_OXIDE,G4_BGO,G4_BLOOD_ICRP,G4_BONE_COMPACT_ICRU,G4_BONE_CORTICAL_ICRP,G4_BORON_CARBIDE,G4_BORON_OXIDE,G4_BRAIN_ICRP,G4_BUTANE,G4_N_BUTYL_ALCOHOL,G4_C_552,+152 more]
FEATURE [App::DocumentObjectGroupPython] H_element113  label="H_element : 062"  # scripted group (container) (typed FeaturePython)
  n = 1
  ref = H_element
FEATURE [App::DocumentObjectGroupPython] G4_H  # scripted group (container) (typed FeaturePython)
  Dunit = g/cm3
  Dvalue = 8.3748e-05
  Group = -> [H_element113]
  conduct = 2
  density = 1
  expand = 3
  formula = H
  name = G4_H
  specific = 4
FEATURE [App::DocumentObjectGroupPython] He_element001  label="He_element : 1"  # scripted group (container) (typed FeaturePython)
  n = 1
  ref = He_element
FEATURE [App::DocumentObjectGroupPython] G4_He  # scripted group (container) (typed FeaturePython)
  Dunit = g/cm3
  Dvalue = 0.000166322
  Group = -> [He_element001]
  conduct = 2
  density = 1
  expand = 3
  formula = He
  name = G4_He
  specific = 4
FEATURE [App::DocumentObjectGroupPython] Li_element008  label="Li_element : 008"  # scripted group (container) (typed FeaturePython)
  n = 1
  ref = Li_element
FEATURE [App::DocumentObjectGroupPython] G4_Li  # scripted group (container) (typed FeaturePython)
  Dunit = g/cm3
  Dvalue = 0.534
  Group = -> [Li_element008]
  conduct = 2
  density = 1
  expand = 3
  formula = Li
  name = G4_Li
  specific = 4
FEATURE [App::DocumentObjectGroupPython] Be_element002  label="Be_element : 002"  # scripted group (container) (typed FeaturePython)
  n = 1
  ref = Be_element
FEATURE [App::DocumentObjectGroupPython] G4_Be  # scripted group (container) (typed FeaturePython)
  Dunit = g/cm3
  Dvalue = 1.848
  Group = -> [Be_element002]
  conduct = 2
  density = 1
  expand = 3
  formula = Be
  name = G4_Be
  specific = 4
FEATURE [App::DocumentObjectGroupPython] B_element007  label="B_element : 007"  # scripted group (container) (typed FeaturePython)
  n = 1
  ref = B_element
FEATURE [App::DocumentObjectGroupPython] G4_B  # scripted group (container) (typed FeaturePython)
  Dunit = g/cm3
  Dvalue = 2.37
  Group = -> [B_element007]
  conduct = 2
  density = 1
  expand = 3
  formula = B
  name = G4_B
  specific = 4
FEATURE [App::DocumentObjectGroupPython] C_element124  label="C_element : 070"  # scripted group (container) (typed FeaturePython)
  n = 1
  ref = C_element
FEATURE [App::DocumentObjectGroupPython] G4_C  # scripted group (container) (typed FeaturePython)
  Dunit = g/cm3
  Dvalue = 2
  Group = -> [C_element124]
  conduct = 2
  density = 1
  expand = 3
  formula = C
  name = G4_C
  specific = 4
FEATURE [App::DocumentObjectGroupPython] N_element048  label="N_element : 021"  # scripted group (container) (typed FeaturePython)
  n = 1
  ref = N_element
FEATURE [App::DocumentObjectGroupPython] G4_N  # scripted group (container) (typed FeaturePython)
  Dunit = g/cm3
  Dvalue = 0.0011652
  Group = -> [N_element048]
  conduct = 2
  density = 1
  expand = 3
  formula = N
  name = G4_N
  specific = 4
FEATURE [App::DocumentObjectGroupPython] O_element105  label="O_element : 059"  # scripted group (container) (typed FeaturePython)
  n = 1
  ref = O_element
FEATURE [App::DocumentObjectGroupPython] G4_O  # scripted group (container) (typed FeaturePython)
  Dunit = g/cm3
  Dvalue = 0.00133151
  Group = -> [O_element105]
  conduct = 2
  density = 1
  expand = 3
  formula = O
  name = G4_O
  specific = 4
FEATURE [App::DocumentObjectGroupPython] F_element019  label="F_element : 008"  # scripted group (container) (typed FeaturePython)
  n = 1
  ref = F_element
FEATURE [App::DocumentObjectGroupPython] G4_F  # scripted group (container) (typed FeaturePython)
  Dunit = g/cm3
  Dvalue = 0.00158029
  Group = -> [F_element019]
  conduct = 2
  density = 1
  expand = 3
  formula = F
  name = G4_F
  specific = 4
FEATURE [App::DocumentObjectGroupPython] Ne_element001  label="Ne_element : 1"  # scripted group (container) (typed FeaturePython)
  n = 1
  ref = Ne_element
FEATURE [App::DocumentObjectGroupPython] G4_Ne  # scripted group (container) (typed FeaturePython)
  Dunit = g/cm3
  Dvalue = 0.000838505
  Group = -> [Ne_element001]
  conduct = 2
  density = 1
  expand = 3
  formula = Ne
  name = G4_Ne
  specific = 4
FEATURE [App::DocumentObjectGroupPython] Na_element020  label="Na_element : 005"  # scripted group (container) (typed FeaturePython)
  n = 1
  ref = Na_element
FEATURE [App::DocumentObjectGroupPython] G4_Na  # scripted group (container) (typed FeaturePython)
  Dunit = g/cm3
  Dvalue = 0.971
  Group = -> [Na_element020]
  conduct = 2
  density = 1
  expand = 3
  formula = Na
  name = G4_Na
  specific = 4
FEATURE [App::DocumentObjectGroupPython] Mg_element011  label="Mg_element : 005"  # scripted group (container) (typed FeaturePython)
  n = 1
  ref = Mg_element
FEATURE [App::DocumentObjectGroupPython] G4_Mg  # scripted group (container) (typed FeaturePython)
  Dunit = g/cm3
  Dvalue = 1.74
  Group = -> [Mg_element011]
  conduct = 2
  density = 1
  expand = 3
  formula = Mg
  name = G4_Mg
  specific = 4
FEATURE [App::DocumentObjectGroupPython] Al_element004  label="Al_element : 1"  # scripted group (container) (typed FeaturePython)
  n = 1
  ref = Al_element
FEATURE [App::DocumentObjectGroupPython] G4_Al  # scripted group (container) (typed FeaturePython)
  Dunit = g/cm3
  Dvalue = 2.699
  Group = -> [Al_element004]
  conduct = 2
  density = 1
  expand = 3
  formula = Al
  name = G4_Al
  specific = 4
FEATURE [App::DocumentObjectGroupPython] Si_element007  label="Si_element : 002"  # scripted group (container) (typed FeaturePython)
  n = 1
  ref = Si_element
FEATURE [App::DocumentObjectGroupPython] G4_Si  # scripted group (container) (typed FeaturePython)
  Dunit = g/cm3
  Dvalue = 2.33
  Group = -> [Si_element007]
  conduct = 2
  density = 1
  expand = 3
  formula = Si
  name = G4_Si
  specific = 4
FEATURE [App::DocumentObjectGroupPython] P_element013  label="P_element : 002"  # scripted group (container) (typed FeaturePython)
  n = 1
  ref = P_element
FEATURE [App::DocumentObjectGroupPython] G4_P  # scripted group (container) (typed FeaturePython)
  Dunit = g/cm3
  Dvalue = 2.2
  Group = -> [P_element013]
  conduct = 2
  density = 1
  expand = 3
  formula = P
  name = G4_P
  specific = 4
FEATURE [App::DocumentObjectGroupPython] S_element023  label="S_element : 007"  # scripted group (container) (typed FeaturePython)
  n = 1
  ref = S_element
FEATURE [App::DocumentObjectGroupPython] G4_S  # scripted group (container) (typed FeaturePython)
  Dunit = g/cm3
  Dvalue = 2
  Group = -> [S_element023]
  conduct = 2
  density = 1
  expand = 3
  formula = S
  name = G4_S
  specific = 4
FEATURE [App::DocumentObjectGroupPython] Cl_element029  label="Cl_element : 015"  # scripted group (container) (typed FeaturePython)
  n = 1
  ref = Cl_element
FEATURE [App::DocumentObjectGroupPython] G4_Cl  # scripted group (container) (typed FeaturePython)
  Dunit = g/cm3
  Dvalue = 0.00299473
  Group = -> [Cl_element029]
  conduct = 2
  density = 1
  expand = 3
  formula = Cl
  name = G4_Cl
  specific = 4
FEATURE [App::DocumentObjectGroupPython] Ar_element002  label="Ar_element : 1"  # scripted group (container) (typed FeaturePython)
  n = 1
  ref = Ar_element
FEATURE [App::DocumentObjectGroupPython] G4_Ar  # scripted group (container) (typed FeaturePython)
  Dunit = g/cm3
  Dvalue = 0.00166201
  Group = -> [Ar_element002]
  conduct = 2
  density = 1
  expand = 3
  formula = Ar
  name = G4_Ar
  specific = 4
FEATURE [App::DocumentObjectGroupPython] K_element013  label="K_element : 003"  # scripted group (container) (typed FeaturePython)
  n = 1
  ref = K_element
FEATURE [App::DocumentObjectGroupPython] G4_K  # scripted group (container) (typed FeaturePython)
  Dunit = g/cm3
  Dvalue = 0.862
  Group = -> [K_element013]
  conduct = 2
  density = 1
  expand = 3
  formula = K
  name = G4_K
  specific = 4
FEATURE [App::DocumentObjectGroupPython] Ca_element014  label="Ca_element : 007"  # scripted group (container) (typed FeaturePython)
  n = 1
  ref = Ca_element
FEATURE [App::DocumentObjectGroupPython] G4_Ca  # scripted group (container) (typed FeaturePython)
  Dunit = g/cm3
  Dvalue = 1.55
  Group = -> [Ca_element014]
  conduct = 2
  density = 1
  expand = 3
  formula = Ca
  name = G4_Ca
  specific = 4
FEATURE [App::DocumentObjectGroupPython] Sc_element001  label="Sc_element : 1"  # scripted group (container) (typed FeaturePython)
  n = 1
  ref = Sc_element
FEATURE [App::DocumentObjectGroupPython] G4_Sc  # scripted group (container) (typed FeaturePython)
  Dunit = g/cm3
  Dvalue = 2.989
  Group = -> [Sc_element001]
  conduct = 2
  density = 1
  expand = 3
  formula = Sc
  name = G4_Sc
  specific = 4
FEATURE [App::DocumentObjectGroupPython] Ti_element004  label="Ti_element : 002"  # scripted group (container) (typed FeaturePython)
  n = 1
  ref = Ti_element
FEATURE [App::DocumentObjectGroupPython] G4_Ti  # scripted group (container) (typed FeaturePython)
  Dunit = g/cm3
  Dvalue = 4.54
  Group = -> [Ti_element004]
  conduct = 2
  density = 1
  expand = 3
  formula = Ti
  name = G4_Ti
  specific = 4
FEATURE [App::DocumentObjectGroupPython] V_element001  label="V_element : 1"  # scripted group (container) (typed FeaturePython)
  n = 1
  ref = V_element
FEATURE [App::DocumentObjectGroupPython] G4_V  # scripted group (container) (typed FeaturePython)
  Dunit = g/cm3
  Dvalue = 6.11
  Group = -> [V_element001]
  conduct = 2
  density = 1
  expand = 3
  formula = V
  name = G4_V
  specific = 4
FEATURE [App::DocumentObjectGroupPython] Cr_element001  label="Cr_element : 1"  # scripted group (container) (typed FeaturePython)
  n = 1
  ref = Cr_element
FEATURE [App::DocumentObjectGroupPython] G4_Cr  # scripted group (container) (typed FeaturePython)
  Dunit = g/cm3
  Dvalue = 7.18
  Group = -> [Cr_element001]
  conduct = 2
  density = 1
  expand = 3
  formula = Cr
  name = G4_Cr
  specific = 4
FEATURE [App::DocumentObjectGroupPython] Mn_element001  label="Mn_element : 1"  # scripted group (container) (typed FeaturePython)
  n = 1
  ref = Mn_element
FEATURE [App::DocumentObjectGroupPython] G4_Mn  # scripted group (container) (typed FeaturePython)
  Dunit = g/cm3
  Dvalue = 7.44
  Group = -> [Mn_element001]
  conduct = 2
  density = 1
  expand = 3
  formula = Mn
  name = G4_Mn
  specific = 4
FEATURE [App::DocumentObjectGroupPython] Fe_element007  label="Fe_element : 004"  # scripted group (container) (typed FeaturePython)
  n = 1
  ref = Fe_element
FEATURE [App::DocumentObjectGroupPython] G4_Fe  # scripted group (container) (typed FeaturePython)
  Dunit = g/cm3
  Dvalue = 7.874
  Group = -> [Fe_element007]
  conduct = 2
  density = 1
  expand = 3
  formula = Fe
  name = G4_Fe
  specific = 4
FEATURE [App::DocumentObjectGroupPython] Co_element001  label="Co_element : 1"  # scripted group (container) (typed FeaturePython)
  n = 1
  ref = Co_element
FEATURE [App::DocumentObjectGroupPython] G4_Co  # scripted group (container) (typed FeaturePython)
  Dunit = g/cm3
  Dvalue = 8.9
  Group = -> [Co_element001]
  conduct = 2
  density = 1
  expand = 3
  formula = Co
  name = G4_Co
  specific = 4
FEATURE [App::DocumentObjectGroupPython] Ni_element001  label="Ni_element : 1"  # scripted group (container) (typed FeaturePython)
  n = 1
  ref = Ni_element
FEATURE [App::DocumentObjectGroupPython] G4_Ni  # scripted group (container) (typed FeaturePython)
  Dunit = g/cm3
  Dvalue = 8.902
  Group = -> [Ni_element001]
  conduct = 2
  density = 1
  expand = 3
  formula = Ni
  name = G4_Ni
  specific = 4
FEATURE [App::DocumentObjectGroupPython] Cu_element001  label="Cu_element : 1"  # scripted group (container) (typed FeaturePython)
  n = 1
  ref = Cu_element
FEATURE [App::DocumentObjectGroupPython] G4_Cu  # scripted group (container) (typed FeaturePython)
  Dunit = g/cm3
  Dvalue = 8.96
  Group = -> [Cu_element001]
  conduct = 2
  density = 1
  expand = 3
  formula = Cu
  name = G4_Cu
  specific = 4
FEATURE [App::DocumentObjectGroupPython] Zn_element001  label="Zn_element : 1"  # scripted group (container) (typed FeaturePython)
  n = 1
  ref = Zn_element
FEATURE [App::DocumentObjectGroupPython] G4_Zn  # scripted group (container) (typed FeaturePython)
  Dunit = g/cm3
  Dvalue = 7.133
  Group = -> [Zn_element001]
  conduct = 2
  density = 1
  expand = 3
  formula = Zn
  name = G4_Zn
  specific = 4
FEATURE [App::DocumentObjectGroupPython] Ga_element002  label="Ga_element : 002"  # scripted group (container) (typed FeaturePython)
  n = 1
  ref = Ga_element
FEATURE [App::DocumentObjectGroupPython] G4_Ga  # scripted group (container) (typed FeaturePython)
  Dunit = g/cm3
  Dvalue = 5.904
  Group = -> [Ga_element002]
  conduct = 2
  density = 1
  expand = 3
  formula = Ga
  name = G4_Ga
  specific = 4
FEATURE [App::DocumentObjectGroupPython] Ge_element002  label="Ge_element : 1"  # scripted group (container) (typed FeaturePython)
  n = 1
  ref = Ge_element
FEATURE [App::DocumentObjectGroupPython] G4_Ge  # scripted group (container) (typed FeaturePython)
  Dunit = g/cm3
  Dvalue = 5.323
  Group = -> [Ge_element002]
  conduct = 2
  density = 1
  expand = 3
  formula = Ge
  name = G4_Ge
  specific = 4
FEATURE [App::DocumentObjectGroupPython] As_element003  label="As_element : 002"  # scripted group (container) (typed FeaturePython)
  n = 1
  ref = As_element
FEATURE [App::DocumentObjectGroupPython] G4_As  # scripted group (container) (typed FeaturePython)
  Dunit = g/cm3
  Dvalue = 5.73
  Group = -> [As_element003]
  conduct = 2
  density = 1
  expand = 3
  formula = As
  name = G4_As
  specific = 4
FEATURE [App::DocumentObjectGroupPython] Se_element001  label="Se_element : 1"  # scripted group (container) (typed FeaturePython)
  n = 1
  ref = Se_element
FEATURE [App::DocumentObjectGroupPython] G4_Se  # scripted group (container) (typed FeaturePython)
  Dunit = g/cm3
  Dvalue = 4.5
  Group = -> [Se_element001]
  conduct = 2
  density = 1
  expand = 3
  formula = Se
  name = G4_Se
  specific = 4
FEATURE [App::DocumentObjectGroupPython] Br_element007  label="Br_element : 004"  # scripted group (container) (typed FeaturePython)
  n = 1
  ref = Br_element
FEATURE [App::DocumentObjectGroupPython] G4_Br  # scripted group (container) (typed FeaturePython)
  Dunit = g/cm3
  Dvalue = 0.0070721
  Group = -> [Br_element007]
  conduct = 2
  density = 1
  expand = 3
  formula = Br
  name = G4_Br
  specific = 4
FEATURE [App::DocumentObjectGroupPython] Kr_element001  label="Kr_element : 1"  # scripted group (container) (typed FeaturePython)
  n = 1
  ref = Kr_element
FEATURE [App::DocumentObjectGroupPython] G4_Kr  # scripted group (container) (typed FeaturePython)
  Dunit = g/cm3
  Dvalue = 0.00347832
  Group = -> [Kr_element001]
  conduct = 2
  density = 1
  expand = 3
  formula = Kr
  name = G4_Kr
  specific = 4
FEATURE [App::DocumentObjectGroupPython] Rb_element001  label="Rb_element : 1"  # scripted group (container) (typed FeaturePython)
  n = 1
  ref = Rb_element
FEATURE [App::DocumentObjectGroupPython] G4_Rb  # scripted group (container) (typed FeaturePython)
  Dunit = g/cm3
  Dvalue = 1.532
  Group = -> [Rb_element001]
  conduct = 2
  density = 1
  expand = 3
  formula = Rb
  name = G4_Rb
  specific = 4
FEATURE [App::DocumentObjectGroupPython] Sr_element001  label="Sr_element : 1"  # scripted group (container) (typed FeaturePython)
  n = 1
  ref = Sr_element
FEATURE [App::DocumentObjectGroupPython] G4_Sr  # scripted group (container) (typed FeaturePython)
  Dunit = g/cm3
  Dvalue = 2.54
  Group = -> [Sr_element001]
  conduct = 2
  density = 1
  expand = 3
  formula = Sr
  name = G4_Sr
  specific = 4
FEATURE [App::DocumentObjectGroupPython] Y_element001  label="Y_element : 1"  # scripted group (container) (typed FeaturePython)
  n = 1
  ref = Y_element
FEATURE [App::DocumentObjectGroupPython] G4_Y  # scripted group (container) (typed FeaturePython)
  Dunit = g/cm3
  Dvalue = 4.469
  Group = -> [Y_element001]
  conduct = 2
  density = 1
  expand = 3
  formula = Y
  name = G4_Y
  specific = 4
FEATURE [App::DocumentObjectGroupPython] Zr_element001  label="Zr_element : 1"  # scripted group (container) (typed FeaturePython)
  n = 1
  ref = Zr_element
FEATURE [App::DocumentObjectGroupPython] G4_Zr  # scripted group (container) (typed FeaturePython)
  Dunit = g/cm3
  Dvalue = 6.506
  Group = -> [Zr_element001]
  conduct = 2
  density = 1
  expand = 3
  formula = Zr
  name = G4_Zr
  specific = 4
FEATURE [App::DocumentObjectGroupPython] Nb_element001  label="Nb_element : 1"  # scripted group (container) (typed FeaturePython)
  n = 1
  ref = Nb_element
FEATURE [App::DocumentObjectGroupPython] G4_Nb  # scripted group (container) (typed FeaturePython)
  Dunit = g/cm3
  Dvalue = 8.57
  Group = -> [Nb_element001]
  conduct = 2
  density = 1
  expand = 3
  formula = Nb
  name = G4_Nb
  specific = 4
FEATURE [App::DocumentObjectGroupPython] Mo_element001  label="Mo_element : 1"  # scripted group (container) (typed FeaturePython)
  n = 1
  ref = Mo_element
FEATURE [App::DocumentObjectGroupPython] G4_Mo  # scripted group (container) (typed FeaturePython)
  Dunit = g/cm3
  Dvalue = 10.22
  Group = -> [Mo_element001]
  conduct = 2
  density = 1
  expand = 3
  formula = Mo
  name = G4_Mo
  specific = 4
FEATURE [App::DocumentObjectGroupPython] Tc_element001  label="Tc_element : 1"  # scripted group (container) (typed FeaturePython)
  n = 1
  ref = Tc_element
FEATURE [App::DocumentObjectGroupPython] G4_Tc  # scripted group (container) (typed FeaturePython)
  Dunit = g/cm3
  Dvalue = 11.5
  Group = -> [Tc_element001]
  conduct = 2
  density = 1
  expand = 3
  formula = Tc
  name = G4_Tc
  specific = 4
FEATURE [App::DocumentObjectGroupPython] Ru_element001  label="Ru_element : 1"  # scripted group (container) (typed FeaturePython)
  n = 1
  ref = Ru_element
FEATURE [App::DocumentObjectGroupPython] G4_Ru  # scripted group (container) (typed FeaturePython)
  Dunit = g/cm3
  Dvalue = 12.41
  Group = -> [Ru_element001]
  conduct = 2
  density = 1
  expand = 3
  formula = Ru
  name = G4_Ru
  specific = 4
FEATURE [App::DocumentObjectGroupPython] Rh_element001  label="Rh_element : 1"  # scripted group (container) (typed FeaturePython)
  n = 1
  ref = Rh_element
FEATURE [App::DocumentObjectGroupPython] G4_Rh  # scripted group (container) (typed FeaturePython)
  Dunit = g/cm3
  Dvalue = 12.41
  Group = -> [Rh_element001]
  conduct = 2
  density = 1
  expand = 3
  formula = Rh
  name = G4_Rh
  specific = 4
FEATURE [App::DocumentObjectGroupPython] Pd_element001  label="Pd_element : 1"  # scripted group (container) (typed FeaturePython)
  n = 1
  ref = Pd_element
FEATURE [App::DocumentObjectGroupPython] G4_Pd  # scripted group (container) (typed FeaturePython)
  Dunit = g/cm3
  Dvalue = 12.02
  Group = -> [Pd_element001]
  conduct = 2
  density = 1
  expand = 3
  formula = Pd
  name = G4_Pd
  specific = 4
FEATURE [App::DocumentObjectGroupPython] Ag_element006  label="Ag_element : 004"  # scripted group (container) (typed FeaturePython)
  n = 1
  ref = Ag_element
FEATURE [App::DocumentObjectGroupPython] G4_Ag  # scripted group (container) (typed FeaturePython)
  Dunit = g/cm3
  Dvalue = 10.5
  Group = -> [Ag_element006]
  conduct = 2
  density = 1
  expand = 3
  formula = Ag
  name = G4_Ag
  specific = 4
FEATURE [App::DocumentObjectGroupPython] Cd_element003  label="Cd_element : 003"  # scripted group (container) (typed FeaturePython)
  n = 1
  ref = Cd_element
FEATURE [App::DocumentObjectGroupPython] G4_Cd  # scripted group (container) (typed FeaturePython)
  Dunit = g/cm3
  Dvalue = 8.65
  Group = -> [Cd_element003]
  conduct = 2
  density = 1
  expand = 3
  formula = Cd
  name = G4_Cd
  specific = 4
FEATURE [App::DocumentObjectGroupPython] In_element001  label="In_element : 1"  # scripted group (container) (typed FeaturePython)
  n = 1
  ref = In_element
FEATURE [App::DocumentObjectGroupPython] G4_In  # scripted group (container) (typed FeaturePython)
  Dunit = g/cm3
  Dvalue = 7.31
  Group = -> [In_element001]
  conduct = 2
  density = 1
  expand = 3
  formula = In
  name = G4_In
  specific = 4
FEATURE [App::DocumentObjectGroupPython] Sn_element001  label="Sn_element : 1"  # scripted group (container) (typed FeaturePython)
  n = 1
  ref = Sn_element
FEATURE [App::DocumentObjectGroupPython] G4_Sn  # scripted group (container) (typed FeaturePython)
  Dunit = g/cm3
  Dvalue = 7.31
  Group = -> [Sn_element001]
  conduct = 2
  density = 1
  expand = 3
  formula = Sn
  name = G4_Sn
  specific = 4
FEATURE [App::DocumentObjectGroupPython] Sb_element001  label="Sb_element : 1"  # scripted group (container) (typed FeaturePython)
  n = 1
  ref = Sb_element
FEATURE [App::DocumentObjectGroupPython] G4_Sb  # scripted group (container) (typed FeaturePython)
  Dunit = g/cm3
  Dvalue = 6.691
  Group = -> [Sb_element001]
  conduct = 2
  density = 1
  expand = 3
  formula = Sb
  name = G4_Sb
  specific = 4
FEATURE [App::DocumentObjectGroupPython] Te_element002  label="Te_element : 002"  # scripted group (container) (typed FeaturePython)
  n = 1
  ref = Te_element
FEATURE [App::DocumentObjectGroupPython] G4_Te  # scripted group (container) (typed FeaturePython)
  Dunit = g/cm3
  Dvalue = 6.24
  Group = -> [Te_element002]
  conduct = 2
  density = 1
  expand = 3
  formula = Te
  name = G4_Te
  specific = 4
FEATURE [App::DocumentObjectGroupPython] I_element010  label="I_element : 006"  # scripted group (container) (typed FeaturePython)
  n = 1
  ref = I_element
FEATURE [App::DocumentObjectGroupPython] G4_I  # scripted group (container) (typed FeaturePython)
  Dunit = g/cm3
  Dvalue = 4.93
  Group = -> [I_element010]
  conduct = 2
  density = 1
  expand = 3
  formula = I
  name = G4_I
  specific = 4
FEATURE [App::DocumentObjectGroupPython] Xe_element001  label="Xe_element : 1"  # scripted group (container) (typed FeaturePython)
  n = 1
  ref = Xe_element
FEATURE [App::DocumentObjectGroupPython] G4_Xe  # scripted group (container) (typed FeaturePython)
  Dunit = g/cm3
  Dvalue = 0.00548536
  Group = -> [Xe_element001]
  conduct = 2
  density = 1
  expand = 3
  formula = Xe
  name = G4_Xe
  specific = 4
FEATURE [App::DocumentObjectGroupPython] Cs_element003  label="Cs_element : 003"  # scripted group (container) (typed FeaturePython)
  n = 1
  ref = Cs_element
FEATURE [App::DocumentObjectGroupPython] G4_Cs  # scripted group (container) (typed FeaturePython)
  Dunit = g/cm3
  Dvalue = 1.873
  Group = -> [Cs_element003]
  conduct = 2
  density = 1
  expand = 3
  formula = Cs
  name = G4_Cs
  specific = 4
FEATURE [App::DocumentObjectGroupPython] Ba_element003  label="Ba_element : 003"  # scripted group (container) (typed FeaturePython)
  n = 1
  ref = Ba_element
FEATURE [App::DocumentObjectGroupPython] G4_Ba  # scripted group (container) (typed FeaturePython)
  Dunit = g/cm3
  Dvalue = 3.5
  Group = -> [Ba_element003]
  conduct = 2
  density = 1
  expand = 3
  formula = Ba
  name = G4_Ba
  specific = 4
FEATURE [App::DocumentObjectGroupPython] La_element003  label="La_element : 003"  # scripted group (container) (typed FeaturePython)
  n = 1
  ref = La_element
FEATURE [App::DocumentObjectGroupPython] G4_La  # scripted group (container) (typed FeaturePython)
  Dunit = g/cm3
  Dvalue = 6.154
  Group = -> [La_element003]
  conduct = 2
  density = 1
  expand = 3
  formula = La
  name = G4_La
  specific = 4
FEATURE [App::DocumentObjectGroupPython] Ce_element002  label="Ce_element : 1"  # scripted group (container) (typed FeaturePython)
  n = 1
  ref = Ce_element
FEATURE [App::DocumentObjectGroupPython] G4_Ce  # scripted group (container) (typed FeaturePython)
  Dunit = g/cm3
  Dvalue = 6.657
  Group = -> [Ce_element002]
  conduct = 2
  density = 1
  expand = 3
  formula = Ce
  name = G4_Ce
  specific = 4
FEATURE [App::DocumentObjectGroupPython] Pr_element001  label="Pr_element : 1"  # scripted group (container) (typed FeaturePython)
  n = 1
  ref = Pr_element
FEATURE [App::DocumentObjectGroupPython] G4_Pr  # scripted group (container) (typed FeaturePython)
  Dunit = g/cm3
  Dvalue = 6.71
  Group = -> [Pr_element001]
  conduct = 2
  density = 1
  expand = 3
  formula = Pr
  name = G4_Pr
  specific = 4
FEATURE [App::DocumentObjectGroupPython] Nd_element001  label="Nd_element : 1"  # scripted group (container) (typed FeaturePython)
  n = 1
  ref = Nd_element
FEATURE [App::DocumentObjectGroupPython] G4_Nd  # scripted group (container) (typed FeaturePython)
  Dunit = g/cm3
  Dvalue = 6.9
  Group = -> [Nd_element001]
  conduct = 2
  density = 1
  expand = 3
  formula = Nd
  name = G4_Nd
  specific = 4
FEATURE [App::DocumentObjectGroupPython] Pm_element001  label="Pm_element : 1"  # scripted group (container) (typed FeaturePython)
  n = 1
  ref = Pm_element
FEATURE [App::DocumentObjectGroupPython] G4_Pm  # scripted group (container) (typed FeaturePython)
  Dunit = g/cm3
  Dvalue = 7.22
  Group = -> [Pm_element001]
  conduct = 2
  density = 1
  expand = 3
  formula = Pm
  name = G4_Pm
  specific = 4
FEATURE [App::DocumentObjectGroupPython] Sm_element001  label="Sm_element : 1"  # scripted group (container) (typed FeaturePython)
  n = 1
  ref = Sm_element
FEATURE [App::DocumentObjectGroupPython] G4_Sm  # scripted group (container) (typed FeaturePython)
  Dunit = g/cm3
  Dvalue = 7.46
  Group = -> [Sm_element001]
  conduct = 2
  density = 1
  expand = 3
  formula = Sm
  name = G4_Sm
  specific = 4
FEATURE [App::DocumentObjectGroupPython] Eu_element001  label="Eu_element : 1"  # scripted group (container) (typed FeaturePython)
  n = 1
  ref = Eu_element
FEATURE [App::DocumentObjectGroupPython] G4_Eu  # scripted group (container) (typed FeaturePython)
  Dunit = g/cm3
  Dvalue = 5.243
  Group = -> [Eu_element001]
  conduct = 2
  density = 1
  expand = 3
  formula = Eu
  name = G4_Eu
  specific = 4
FEATURE [App::DocumentObjectGroupPython] Gd_element002  label="Gd_element : 1"  # scripted group (container) (typed FeaturePython)
  n = 1
  ref = Gd_element
FEATURE [App::DocumentObjectGroupPython] G4_Gd  # scripted group (container) (typed FeaturePython)
  Dunit = g/cm3
  Dvalue = 7.9004
  Group = -> [Gd_element002]
  conduct = 2
  density = 1
  expand = 3
  formula = Gd
  name = G4_Gd
  specific = 4
FEATURE [App::DocumentObjectGroupPython] Tb_element001  label="Tb_element : 1"  # scripted group (container) (typed FeaturePython)
  n = 1
  ref = Tb_element
FEATURE [App::DocumentObjectGroupPython] G4_Tb  # scripted group (container) (typed FeaturePython)
  Dunit = g/cm3
  Dvalue = 8.229
  Group = -> [Tb_element001]
  conduct = 2
  density = 1
  expand = 3
  formula = Tb
  name = G4_Tb
  specific = 4
FEATURE [App::DocumentObjectGroupPython] Dy_element001  label="Dy_element : 1"  # scripted group (container) (typed FeaturePython)
  n = 1
  ref = Dy_element
FEATURE [App::DocumentObjectGroupPython] G4_Dy  # scripted group (container) (typed FeaturePython)
  Dunit = g/cm3
  Dvalue = 8.55
  Group = -> [Dy_element001]
  conduct = 2
  density = 1
  expand = 3
  formula = Dy
  name = G4_Dy
  specific = 4
FEATURE [App::DocumentObjectGroupPython] Ho_element001  label="Ho_element : 1"  # scripted group (container) (typed FeaturePython)
  n = 1
  ref = Ho_element
FEATURE [App::DocumentObjectGroupPython] G4_Ho  # scripted group (container) (typed FeaturePython)
  Dunit = g/cm3
  Dvalue = 8.795
  Group = -> [Ho_element001]
  conduct = 2
  density = 1
  expand = 3
  formula = Ho
  name = G4_Ho
  specific = 4
FEATURE [App::DocumentObjectGroupPython] Er_element001  label="Er_element : 1"  # scripted group (container) (typed FeaturePython)
  n = 1
  ref = Er_element
FEATURE [App::DocumentObjectGroupPython] G4_Er  # scripted group (container) (typed FeaturePython)
  Dunit = g/cm3
  Dvalue = 9.066
  Group = -> [Er_element001]
  conduct = 2
  density = 1
  expand = 3
  formula = Er
  name = G4_Er
  specific = 4
FEATURE [App::DocumentObjectGroupPython] Tm_element001  label="Tm_element : 1"  # scripted group (container) (typed FeaturePython)
  n = 1
  ref = Tm_element
FEATURE [App::DocumentObjectGroupPython] G4_Tm  # scripted group (container) (typed FeaturePython)
  Dunit = g/cm3
  Dvalue = 9.321
  Group = -> [Tm_element001]
  conduct = 2
  density = 1
  expand = 3
  formula = Tm
  name = G4_Tm
  specific = 4
FEATURE [App::DocumentObjectGroupPython] Yb_element001  label="Yb_element : 1"  # scripted group (container) (typed FeaturePython)
  n = 1
  ref = Yb_element
FEATURE [App::DocumentObjectGroupPython] G4_Yb  # scripted group (container) (typed FeaturePython)
  Dunit = g/cm3
  Dvalue = 6.73
  Group = -> [Yb_element001]
  conduct = 2
  density = 1
  expand = 3
  formula = Yb
  name = G4_Yb
  specific = 4
FEATURE [App::DocumentObjectGroupPython] Lu_element001  label="Lu_element : 1"  # scripted group (container) (typed FeaturePython)
  n = 1
  ref = Lu_element
FEATURE [App::DocumentObjectGroupPython] G4_Lu  # scripted group (container) (typed FeaturePython)
  Dunit = g/cm3
  Dvalue = 9.84
  Group = -> [Lu_element001]
  conduct = 2
  density = 1
  expand = 3
  formula = Lu
  name = G4_Lu
  specific = 4
FEATURE [App::DocumentObjectGroupPython] Hf_element001  label="Hf_element : 1"  # scripted group (container) (typed FeaturePython)
  n = 1
  ref = Hf_element
FEATURE [App::DocumentObjectGroupPython] G4_Hf  # scripted group (container) (typed FeaturePython)
  Dunit = g/cm3
  Dvalue = 13.31
  Group = -> [Hf_element001]
  conduct = 2
  density = 1
  expand = 3
  formula = Hf
  name = G4_Hf
  specific = 4
FEATURE [App::DocumentObjectGroupPython] Ta_element001  label="Ta_element : 1"  # scripted group (container) (typed FeaturePython)
  n = 1
  ref = Ta_element
FEATURE [App::DocumentObjectGroupPython] G4_Ta  # scripted group (container) (typed FeaturePython)
  Dunit = g/cm3
  Dvalue = 16.654
  Group = -> [Ta_element001]
  conduct = 2
  density = 1
  expand = 3
  formula = Ta
  name = G4_Ta
  specific = 4
FEATURE [App::DocumentObjectGroupPython] W_element004  label="W_element : 004"  # scripted group (container) (typed FeaturePython)
  n = 1
  ref = W_element
FEATURE [App::DocumentObjectGroupPython] G4_W  # scripted group (container) (typed FeaturePython)
  Dunit = g/cm3
  Dvalue = 19.3
  Group = -> [W_element004]
  conduct = 2
  density = 1
  expand = 3
  formula = W
  name = G4_W
  specific = 4
FEATURE [App::DocumentObjectGroupPython] Re_element001  label="Re_element : 1"  # scripted group (container) (typed FeaturePython)
  n = 1
  ref = Re_element
FEATURE [App::DocumentObjectGroupPython] G4_Re  # scripted group (container) (typed FeaturePython)
  Dunit = g/cm3
  Dvalue = 21.02
  Group = -> [Re_element001]
  conduct = 2
  density = 1
  expand = 3
  formula = Re
  name = G4_Re
  specific = 4
FEATURE [App::DocumentObjectGroupPython] Os_element001  label="Os_element : 1"  # scripted group (container) (typed FeaturePython)
  n = 1
  ref = Os_element
FEATURE [App::DocumentObjectGroupPython] G4_Os  # scripted group (container) (typed FeaturePython)
  Dunit = g/cm3
  Dvalue = 22.57
  Group = -> [Os_element001]
  conduct = 2
  density = 1
  expand = 3
  formula = Os
  name = G4_Os
  specific = 4
FEATURE [App::DocumentObjectGroupPython] Ir_element001  label="Ir_element : 1"  # scripted group (container) (typed FeaturePython)
  n = 1
  ref = Ir_element
FEATURE [App::DocumentObjectGroupPython] G4_Ir  # scripted group (container) (typed FeaturePython)
  Dunit = g/cm3
  Dvalue = 22.42
  Group = -> [Ir_element001]
  conduct = 2
  density = 1
  expand = 3
  formula = Ir
  name = G4_Ir
  specific = 4
FEATURE [App::DocumentObjectGroupPython] Pt_element001  label="Pt_element : 1"  # scripted group (container) (typed FeaturePython)
  n = 1
  ref = Pt_element
FEATURE [App::DocumentObjectGroupPython] G4_Pt  # scripted group (container) (typed FeaturePython)
  Dunit = g/cm3
  Dvalue = 21.45
  Group = -> [Pt_element001]
  conduct = 2
  density = 1
  expand = 3
  formula = Pt
  name = G4_Pt
  specific = 4
FEATURE [App::DocumentObjectGroupPython] Au_element001  label="Au_element : 1"  # scripted group (container) (typed FeaturePython)
  n = 1
  ref = Au_element
FEATURE [App::DocumentObjectGroupPython] G4_Au  # scripted group (container) (typed FeaturePython)
  Dunit = g/cm3
  Dvalue = 19.32
  Group = -> [Au_element001]
  conduct = 2
  density = 1
  expand = 3
  formula = Au
  name = G4_Au
  specific = 4
FEATURE [App::DocumentObjectGroupPython] Hg_element002  label="Hg_element : 002"  # scripted group (container) (typed FeaturePython)
  n = 1
  ref = Hg_element
FEATURE [App::DocumentObjectGroupPython] G4_Hg  # scripted group (container) (typed FeaturePython)
  Dunit = g/cm3
  Dvalue = 13.546
  Group = -> [Hg_element002]
  conduct = 2
  density = 1
  expand = 3
  formula = Hg
  name = G4_Hg
  specific = 4
FEATURE [App::DocumentObjectGroupPython] Tl_element002  label="Tl_element : 002"  # scripted group (container) (typed FeaturePython)
  n = 1
  ref = Tl_element
FEATURE [App::DocumentObjectGroupPython] G4_Tl  # scripted group (container) (typed FeaturePython)
  Dunit = g/cm3
  Dvalue = 11.72
  Group = -> [Tl_element002]
  conduct = 2
  density = 1
  expand = 3
  formula = Tl
  name = G4_Tl
  specific = 4
FEATURE [App::DocumentObjectGroupPython] Pb_element003  label="Pb_element : 1"  # scripted group (container) (typed FeaturePython)
  n = 1
  ref = Pb_element
FEATURE [App::DocumentObjectGroupPython] G4_Pb  # scripted group (container) (typed FeaturePython)
  Dunit = g/cm3
  Dvalue = 11.35
  Group = -> [Pb_element003]
  conduct = 2
  density = 1
  expand = 3
  formula = Pb
  name = G4_Pb
  specific = 4
FEATURE [App::DocumentObjectGroupPython] Bi_element002  label="Bi_element : 1"  # scripted group (container) (typed FeaturePython)
  n = 1
  ref = Bi_element
FEATURE [App::DocumentObjectGroupPython] G4_Bi  # scripted group (container) (typed FeaturePython)
  Dunit = g/cm3
  Dvalue = 9.747
  Group = -> [Bi_element002]
  conduct = 2
  density = 1
  expand = 3
  formula = Bi
  name = G4_Bi
  specific = 4
FEATURE [App::DocumentObjectGroupPython] Po_element001  label="Po_element : 1"  # scripted group (container) (typed FeaturePython)
  n = 1
  ref = Po_element
FEATURE [App::DocumentObjectGroupPython] G4_Po  # scripted group (container) (typed FeaturePython)
  Dunit = g/cm3
  Dvalue = 9.32
  Group = -> [Po_element001]
  conduct = 2
  density = 1
  expand = 3
  formula = Po
  name = G4_Po
  specific = 4
FEATURE [App::DocumentObjectGroupPython] At_element001  label="At_element : 1"  # scripted group (container) (typed FeaturePython)
  n = 1
  ref = At_element
FEATURE [App::DocumentObjectGroupPython] G4_At  # scripted group (container) (typed FeaturePython)
  Dunit = g/cm3
  Dvalue = 9.32
  Group = -> [At_element001]
  conduct = 2
  density = 1
  expand = 3
  formula = At
  name = G4_At
  specific = 4
FEATURE [App::DocumentObjectGroupPython] Rn_element001  label="Rn_element : 1"  # scripted group (container) (typed FeaturePython)
  n = 1
  ref = Rn_element
FEATURE [App::DocumentObjectGroupPython] G4_Rn  # scripted group (container) (typed FeaturePython)
  Dunit = g/cm3
  Dvalue = 0.00900662
  Group = -> [Rn_element001]
  conduct = 2
  density = 1
  expand = 3
  formula = Rn
  name = G4_Rn
  specific = 4
FEATURE [App::DocumentObjectGroupPython] Fr_element001  label="Fr_element : 1"  # scripted group (container) (typed FeaturePython)
  n = 1
  ref = Fr_element
FEATURE [App::DocumentObjectGroupPython] G4_Fr  # scripted group (container) (typed FeaturePython)
  Dunit = g/cm3
  Dvalue = 1
  Group = -> [Fr_element001]
  conduct = 2
  density = 1
  expand = 3
  formula = Fr
  name = G4_Fr
  specific = 4
FEATURE [App::DocumentObjectGroupPython] Ra_element001  label="Ra_element : 1"  # scripted group (container) (typed FeaturePython)
  n = 1
  ref = Ra_element
FEATURE [App::DocumentObjectGroupPython] G4_Ra  # scripted group (container) (typed FeaturePython)
  Dunit = g/cm3
  Dvalue = 5
  Group = -> [Ra_element001]
  conduct = 2
  density = 1
  expand = 3
  formula = Ra
  name = G4_Ra
  specific = 4
FEATURE [App::DocumentObjectGroupPython] Ac_element001  label="Ac_element : 1"  # scripted group (container) (typed FeaturePython)
  n = 1
  ref = Ac_element
FEATURE [App::DocumentObjectGroupPython] G4_Ac  # scripted group (container) (typed FeaturePython)
  Dunit = g/cm3
  Dvalue = 10.07
  Group = -> [Ac_element001]
  conduct = 2
  density = 1
  expand = 3
  formula = Ac
  name = G4_Ac
  specific = 4
FEATURE [App::DocumentObjectGroupPython] Th_element001  label="Th_element : 1"  # scripted group (container) (typed FeaturePython)
  n = 1
  ref = Th_element
FEATURE [App::DocumentObjectGroupPython] G4_Th  # scripted group (container) (typed FeaturePython)
  Dunit = g/cm3
  Dvalue = 11.72
  Group = -> [Th_element001]
  conduct = 2
  density = 1
  expand = 3
  formula = Th
  name = G4_Th
  specific = 4
FEATURE [App::DocumentObjectGroupPython] Pa_element001  label="Pa_element : 1"  # scripted group (container) (typed FeaturePython)
  n = 1
  ref = Pa_element
FEATURE [App::DocumentObjectGroupPython] G4_Pa  # scripted group (container) (typed FeaturePython)
  Dunit = g/cm3
  Dvalue = 15.37
  Group = -> [Pa_element001]
  conduct = 2
  density = 1
  expand = 3
  formula = Pa
  name = G4_Pa
  specific = 4
FEATURE [App::DocumentObjectGroupPython] U_element004  label="U_element : 004"  # scripted group (container) (typed FeaturePython)
  n = 1
  ref = U_element
FEATURE [App::DocumentObjectGroupPython] G4_U  # scripted group (container) (typed FeaturePython)
  Dunit = g/cm3
  Dvalue = 18.95
  Group = -> [U_element004]
  conduct = 2
  density = 1
  expand = 3
  formula = U
  name = G4_U
  specific = 4
FEATURE [App::DocumentObjectGroupPython] Np_element001  label="Np_element : 1"  # scripted group (container) (typed FeaturePython)
  n = 1
  ref = Np_element
FEATURE [App::DocumentObjectGroupPython] G4_Np  # scripted group (container) (typed FeaturePython)
  Dunit = g/cm3
  Dvalue = 20.25
  Group = -> [Np_element001]
  conduct = 2
  density = 1
  expand = 3
  formula = Np
  name = G4_Np
  specific = 4
FEATURE [App::DocumentObjectGroupPython] Pu_element002  label="Pu_element : 002"  # scripted group (container) (typed FeaturePython)
  n = 1
  ref = Pu_element
FEATURE [App::DocumentObjectGroupPython] G4_Pu  # scripted group (container) (typed FeaturePython)
  Dunit = g/cm3
  Dvalue = 19.84
  Group = -> [Pu_element002]
  conduct = 2
  density = 1
  expand = 3
  formula = Pu
  name = G4_Pu
  specific = 4
FEATURE [App::DocumentObjectGroupPython] Am_element001  label="Am_element : 1"  # scripted group (container) (typed FeaturePython)
  n = 1
  ref = Am_element
FEATURE [App::DocumentObjectGroupPython] G4_Am  # scripted group (container) (typed FeaturePython)
  Dunit = g/cm3
  Dvalue = 13.67
  Group = -> [Am_element001]
  conduct = 2
  density = 1
  expand = 3
  formula = Am
  name = G4_Am
  specific = 4
FEATURE [App::DocumentObjectGroupPython] Cm_element001  label="Cm_element : 1"  # scripted group (container) (typed FeaturePython)
  n = 1
  ref = Cm_element
FEATURE [App::DocumentObjectGroupPython] G4_Cm  # scripted group (container) (typed FeaturePython)
  Dunit = g/cm3
  Dvalue = 13.51
  Group = -> [Cm_element001]
  conduct = 2
  density = 1
  expand = 3
  formula = Cm
  name = G4_Cm
  specific = 4
FEATURE [App::DocumentObjectGroupPython] Bk_element001  label="Bk_element : 1"  # scripted group (container) (typed FeaturePython)
  n = 1
  ref = Bk_element
FEATURE [App::DocumentObjectGroupPython] G4_Bk  # scripted group (container) (typed FeaturePython)
  Dunit = g/cm3
  Dvalue = 14
  Group = -> [Bk_element001]
  conduct = 2
  density = 1
  expand = 3
  formula = Bk
  name = G4_Bk
  specific = 4
FEATURE [App::DocumentObjectGroupPython] Cf_element001  label="Cf_element : 1"  # scripted group (container) (typed FeaturePython)
  n = 1
  ref = Cf_element
FEATURE [App::DocumentObjectGroupPython] G4_Cf  # scripted group (container) (typed FeaturePython)
  Dunit = g/cm3
  Dvalue = 10
  Group = -> [Cf_element001]
  conduct = 2
  density = 1
  expand = 3
  formula = Cf
  name = G4_Cf
  specific = 4
FEATURE [App::DocumentObjectGroupPython] Element  # scripted group (container) (typed FeaturePython)
  Group = -> [G4_H,G4_He,G4_Li,G4_Be,G4_B,G4_C,G4_N,G4_O,G4_F,G4_Ne,G4_Na,G4_Mg,G4_Al,G4_Si,G4_P,G4_S,G4_Cl,G4_Ar,G4_K,G4_Ca,G4_Sc,G4_Ti,G4_V,G4_Cr,G4_Mn,G4_Fe,G4_Co,G4_Ni,G4_Cu,G4_Zn,G4_Ga,G4_Ge,G4_As,G4_Se,G4_Br,G4_Kr,G4_Rb,G4_Sr,G4_Y,G4_Zr,G4_Nb,G4_Mo,G4_Tc,G4_Ru,G4_Rh,G4_Pd,G4_Ag,G4_Cd,G4_In,G4_Sn,G4_Sb,G4_Te,G4_I,G4_Xe,G4_Cs,G4_Ba,G4_La,G4_Ce,G4_Pr,G4_Nd,G4_Pm,G4_Sm,G4_Eu,G4_Gd,G4_Tb,G4_Dy,G4_Ho,G4_Er,+30 more]
FEATURE [App::DocumentObjectGroupPython] H_element114  label="H_element : 063"  # scripted group (container) (typed FeaturePython)
  n = 2
  ref = H_element
FEATURE [App::DocumentObjectGroupPython] G4_lH2  # scripted group (container) (typed FeaturePython)
  Dunit = g/cm3
  Dvalue = 0.0708
  Group = -> [H_element114]
  conduct = 2
  density = 1
  expand = 3
  formula = G4_lH2
  name = G4_lH2
  specific = 4
FEATURE [App::DocumentObjectGroupPython] N_element049  label="N_element : 022"  # scripted group (container) (typed FeaturePython)
  n = 2
  ref = N_element
FEATURE [App::DocumentObjectGroupPython] G4_lN2  # scripted group (container) (typed FeaturePython)
  Dunit = g/cm3
  Dvalue = 0.807
  Group = -> [N_element049]
  conduct = 2
  density = 1
  expand = 3
  formula = G4_lN2
  name = G4_lN2
  specific = 4
FEATURE [App::DocumentObjectGroupPython] O_element106  label="O_element : 060"  # scripted group (container) (typed FeaturePython)
  n = 2
  ref = O_element
FEATURE [App::DocumentObjectGroupPython] G4_lO2  # scripted group (container) (typed FeaturePython)
  Dunit = g/cm3
  Dvalue = 1.141
  Group = -> [O_element106]
  conduct = 2
  density = 1
  expand = 3
  formula = G4_lO2
  name = G4_lO2
  specific = 4
FEATURE [App::DocumentObjectGroupPython] Ar  label="Ar : 1"  # scripted group (container) (typed FeaturePython)
  n = 1
  ref = Ar
FEATURE [App::DocumentObjectGroupPython] G4_lAr  # scripted group (container) (typed FeaturePython)
  Dunit = g/cm3
  Dvalue = 1.396
  Group = -> [Ar]
  conduct = 2
  density = 1
  expand = 3
  formula = G4_lAr
  name = G4_lAr
  specific = 4
FEATURE [App::DocumentObjectGroupPython] Br  label="Br : 1"  # scripted group (container) (typed FeaturePython)
  n = 1
  ref = Br
FEATURE [App::DocumentObjectGroupPython] G4_lBr  # scripted group (container) (typed FeaturePython)
  Dunit = g/cm3
  Dvalue = 3.1028
  Group = -> [Br]
  conduct = 2
  density = 1
  expand = 3
  formula = G4_lBr
  name = G4_lBr
  specific = 4
FEATURE [App::DocumentObjectGroupPython] Kr  label="Kr : 1"  # scripted group (container) (typed FeaturePython)
  n = 1
  ref = Kr
FEATURE [App::DocumentObjectGroupPython] G4_lKr  # scripted group (container) (typed FeaturePython)
  Dunit = g/cm3
  Dvalue = 2.418
  Group = -> [Kr]
  conduct = 2
  density = 1
  expand = 3
  formula = G4_lKr
  name = G4_lKr
  specific = 4
FEATURE [App::DocumentObjectGroupPython] Xe  label="Xe : 1"  # scripted group (container) (typed FeaturePython)
  n = 1
  ref = Xe
FEATURE [App::DocumentObjectGroupPython] G4_lXe  # scripted group (container) (typed FeaturePython)
  Dunit = g/cm3
  Dvalue = 2.953
  Group = -> [Xe]
  conduct = 2
  density = 1
  expand = 3
  formula = G4_lXe
  name = G4_lXe
  specific = 4
FEATURE [App::DocumentObjectGroupPython] O_element107  label="O_element : 061"  # scripted group (container) (typed FeaturePython)
  n = 4
  ref = O_element
FEATURE [App::DocumentObjectGroupPython] Pb_element004  label="Pb_element : 002"  # scripted group (container) (typed FeaturePython)
  n = 1
  ref = Pb_element
FEATURE [App::DocumentObjectGroupPython] W_element005  label="W_element : 005"  # scripted group (container) (typed FeaturePython)
  n = 1
  ref = W_element
FEATURE [App::DocumentObjectGroupPython] G4_PbWO4  # scripted group (container) (typed FeaturePython)
  Dunit = g/cm3
  Dvalue = 8.28
  Group = -> [O_element107,Pb_element004,W_element005]
  conduct = 2
  density = 1
  expand = 3
  formula = G4_PbWO4
  name = G4_PbWO4
  specific = 4
FEATURE [App::DocumentObjectGroupPython] alactic  label="alactic : 1"  # scripted group (container) (typed FeaturePython)
  n = 1
  ref = alactic
FEATURE [App::DocumentObjectGroupPython] G4_Galactic  # scripted group (container) (typed FeaturePython)
  Dunit = g/cm3
  Dvalue = 0
  Group = -> [alactic]
  conduct = 2
  density = 1
  expand = 3
  formula = G4_Galactic
  name = G4_Galactic
  specific = 4
FEATURE [App::DocumentObjectGroupPython] RAPHITE_POROUS  label="RAPHITE_POROUS : 1"  # scripted group (container) (typed FeaturePython)
  n = 1
  ref = RAPHITE_POROUS
FEATURE [App::DocumentObjectGroupPython] G4_GRAPHITE_POROUS  # scripted group (container) (typed FeaturePython)
  Dunit = g/cm3
  Dvalue = 1.7
  Group = -> [RAPHITE_POROUS]
  conduct = 2
  density = 1
  expand = 3
  formula = G4_GRAPHITE_POROUS
  name = G4_GRAPHITE_POROUS
  specific = 4
FEATURE [App::DocumentObjectGroupPython] H_element115  label="H_element : 0.150"  # scripted group (container) (typed FeaturePython)
  n = 0.080538
FEATURE [App::DocumentObjectGroupPython] C_element125  label="C_element : 0.600"  # scripted group (container) (typed FeaturePython)
  n = 0.599848
FEATURE [App::DocumentObjectGroupPython] O_element108  label="O_element : 0.320"  # scripted group (container) (typed FeaturePython)
  n = 0.319614
FEATURE [App::DocumentObjectGroupPython] G4_LUCITE  # scripted group (container) (typed FeaturePython)
  Dunit = g/cm3
  Dvalue = 1.19
  Group = -> [H_element115,C_element125,O_element108]
  conduct = 2
  density = 1
  expand = 3
  formula = G4_LUCITE
  name = G4_LUCITE
  specific = 4
FEATURE [App::DocumentObjectGroupPython] Cu_element002  label="Cu_element : 62"  # scripted group (container) (typed FeaturePython)
  n = 62
  ref = Cu_element
FEATURE [App::DocumentObjectGroupPython] Zn_element002  label="Zn_element : 35"  # scripted group (container) (typed FeaturePython)
  n = 35
  ref = Zn_element
FEATURE [App::DocumentObjectGroupPython] Pb_element005  label="Pb_element : 3"  # scripted group (container) (typed FeaturePython)
  n = 3
  ref = Pb_element
FEATURE [App::DocumentObjectGroupPython] G4_BRASS  # scripted group (container) (typed FeaturePython)
  Dunit = g/cm3
  Dvalue = 8.52
  Group = -> [Cu_element002,Zn_element002,Pb_element005]
  conduct = 2
  density = 1
  expand = 3
  formula = G4_BRASS
  name = G4_BRASS
  specific = 4
FEATURE [App::DocumentObjectGroupPython] Cu_element003  label="Cu_element : 89"  # scripted group (container) (typed FeaturePython)
  n = 89
  ref = Cu_element
FEATURE [App::DocumentObjectGroupPython] Zn_element003  label="Zn_element : 9"  # scripted group (container) (typed FeaturePython)
  n = 9
  ref = Zn_element
FEATURE [App::DocumentObjectGroupPython] Pb_element006  label="Pb_element : 2"  # scripted group (container) (typed FeaturePython)
  n = 2
  ref = Pb_element
FEATURE [App::DocumentObjectGroupPython] G4_BRONZE  # scripted group (container) (typed FeaturePython)
  Dunit = g/cm3
  Dvalue = 8.82
  Group = -> [Cu_element003,Zn_element003,Pb_element006]
  conduct = 2
  density = 1
  expand = 3
  formula = G4_BRONZE
  name = G4_BRONZE
  specific = 4
FEATURE [App::DocumentObjectGroupPython] Fe_element008  label="Fe_element : 74"  # scripted group (container) (typed FeaturePython)
  n = 74
  ref = Fe_element
FEATURE [App::DocumentObjectGroupPython] Cr_element002  label="Cr_element : 18"  # scripted group (container) (typed FeaturePython)
  n = 18
  ref = Cr_element
FEATURE [App::DocumentObjectGroupPython] Ni_element002  label="Ni_element : 8"  # scripted group (container) (typed FeaturePython)
  n = 8
  ref = Ni_element
FEATURE [App::DocumentObjectGroupPython] G4_STAINLESS_STEEL  label="G4_STAINLESS-STEEL"  # scripted group (container) (typed FeaturePython)
  Dunit = g/cm3
  Dvalue = 8
  Group = -> [Fe_element008,Cr_element002,Ni_element002]
  conduct = 2
  density = 1
  expand = 3
  formula = G4_STAINLESS-STEEL
  name = G4_STAINLESS-STEEL
  specific = 4
FEATURE [App::DocumentObjectGroupPython] H_element116  label="H_element : 064"  # scripted group (container) (typed FeaturePython)
  n = 18
  ref = H_element
FEATURE [App::DocumentObjectGroupPython] C_element126  label="C_element : 071"  # scripted group (container) (typed FeaturePython)
  n = 12
  ref = C_element
FEATURE [App::DocumentObjectGroupPython] O_element109  label="O_element : 062"  # scripted group (container) (typed FeaturePython)
  n = 7
  ref = O_element
FEATURE [App::DocumentObjectGroupPython] G4_CR39  # scripted group (container) (typed FeaturePython)
  Dunit = g/cm3
  Dvalue = 1.32
  Group = -> [H_element116,C_element126,O_element109]
  conduct = 2
  density = 1
  expand = 3
  formula = G4_CR39
  name = G4_CR39
  specific = 4
FEATURE [App::DocumentObjectGroupPython] H_element117  label="H_element : 38"  # scripted group (container) (typed FeaturePython)
  n = 38
  ref = H_element
FEATURE [App::DocumentObjectGroupPython] C_element127  label="C_element : 072"  # scripted group (container) (typed FeaturePython)
  n = 18
  ref = C_element
FEATURE [App::DocumentObjectGroupPython] O_element110  label="O_element : 063"  # scripted group (container) (typed FeaturePython)
  n = 1
  ref = O_element
FEATURE [App::DocumentObjectGroupPython] G4_OCTADECANOL  # scripted group (container) (typed FeaturePython)
  Dunit = g/cm3
  Dvalue = 0.812
  Group = -> [H_element117,C_element127,O_element110]
  conduct = 2
  density = 1
  expand = 3
  formula = G4_OCTADECANOL
  name = G4_OCTADECANOL
  specific = 4
FEATURE [App::DocumentObjectGroupPython] HEP  # scripted group (container) (typed FeaturePython)
  Group = -> [G4_lH2,G4_lN2,G4_lO2,G4_lAr,G4_lBr,G4_lKr,G4_lXe,G4_PbWO4,G4_Galactic,G4_GRAPHITE_POROUS,G4_LUCITE,G4_BRASS,G4_BRONZE,G4_STAINLESS_STEEL,G4_CR39,G4_OCTADECANOL]
FEATURE [App::DocumentObjectGroupPython] C_element128  label="C_element : 073"  # scripted group (container) (typed FeaturePython)
  n = 14
  ref = C_element
FEATURE [App::DocumentObjectGroupPython] H_element118  label="H_element : 065"  # scripted group (container) (typed FeaturePython)
  n = 10
  ref = H_element
FEATURE [App::DocumentObjectGroupPython] O_element111  label="O_element : 064"  # scripted group (container) (typed FeaturePython)
  n = 2
  ref = O_element
FEATURE [App::DocumentObjectGroupPython] N_element050  label="N_element : 023"  # scripted group (container) (typed FeaturePython)
  n = 2
  ref = N_element
FEATURE [App::DocumentObjectGroupPython] G4_KEVLAR  # scripted group (container) (typed FeaturePython)
  Dunit = g/cm3
  Dvalue = 1.44
  Group = -> [C_element128,H_element118,O_element111,N_element050]
  conduct = 2
  density = 1
  expand = 3
  formula = G4_KEVLAR
  name = G4_KEVLAR
  specific = 4
FEATURE [App::DocumentObjectGroupPython] C_element129  label="C_element : 074"  # scripted group (container) (typed FeaturePython)
  n = 10
  ref = C_element
FEATURE [App::DocumentObjectGroupPython] H_element119  label="H_element : 066"  # scripted group (container) (typed FeaturePython)
  n = 8
  ref = H_element
FEATURE [App::DocumentObjectGroupPython] O_element112  label="O_element : 065"  # scripted group (container) (typed FeaturePython)
  n = 4
  ref = O_element
FEATURE [App::DocumentObjectGroupPython] G4_DACRON  # scripted group (container) (typed FeaturePython)
  Dunit = g/cm3
  Dvalue = 1.4
  Group = -> [C_element129,H_element119,O_element112]
  conduct = 2
  density = 1
  expand = 3
  formula = G4_DACRON
  name = G4_DACRON
  specific = 4
FEATURE [App::DocumentObjectGroupPython] C_element130  label="C_element : 075"  # scripted group (container) (typed FeaturePython)
  n = 4
  ref = C_element
FEATURE [App::DocumentObjectGroupPython] H_element120  label="H_element : 067"  # scripted group (container) (typed FeaturePython)
  n = 5
  ref = H_element
FEATURE [App::DocumentObjectGroupPython] Cl_element030  label="Cl_element : 016"  # scripted group (container) (typed FeaturePython)
  n = 1
  ref = Cl_element
FEATURE [App::DocumentObjectGroupPython] G4_NEOPRENE  # scripted group (container) (typed FeaturePython)
  Dunit = g/cm3
  Dvalue = 1.23
  Group = -> [C_element130,H_element120,Cl_element030]
  conduct = 2
  density = 1
  expand = 3
  formula = G4_NEOPRENE
  name = G4_NEOPRENE
  specific = 4
FEATURE [App::DocumentObjectGroupPython] Space  # scripted group (container) (typed FeaturePython)
  Group = -> [G4_KEVLAR,G4_DACRON,G4_NEOPRENE]
FEATURE [App::DocumentObjectGroupPython] H_element121  label="H_element : 068"  # scripted group (container) (typed FeaturePython)
  n = 5
  ref = H_element
FEATURE [App::DocumentObjectGroupPython] C_element131  label="C_element : 076"  # scripted group (container) (typed FeaturePython)
  n = 4
  ref = C_element
FEATURE [App::DocumentObjectGroupPython] N_element051  label="N_element : 3"  # scripted group (container) (typed FeaturePython)
  n = 3
  ref = N_element
FEATURE [App::DocumentObjectGroupPython] O_element113  label="O_element : 066"  # scripted group (container) (typed FeaturePython)
  n = 1
  ref = O_element
FEATURE [App::DocumentObjectGroupPython] G4_CYTOSINE  # scripted group (container) (typed FeaturePython)
  Dunit = g/cm3
  Dvalue = 1.55
  Group = -> [H_element121,C_element131,N_element051,O_element113]
  conduct = 2
  density = 1
  expand = 3
  formula = G4_CYTOSINE
  name = G4_CYTOSINE
  specific = 4
FEATURE [App::DocumentObjectGroupPython] H_element122  label="H_element : 069"  # scripted group (container) (typed FeaturePython)
  n = 6
  ref = H_element
FEATURE [App::DocumentObjectGroupPython] C_element132  label="C_element : 077"  # scripted group (container) (typed FeaturePython)
  n = 5
  ref = C_element
FEATURE [App::DocumentObjectGroupPython] N_element052  label="N_element : 024"  # scripted group (container) (typed FeaturePython)
  n = 2
  ref = N_element
FEATURE [App::DocumentObjectGroupPython] O_element114  label="O_element : 067"  # scripted group (container) (typed FeaturePython)
  n = 2
  ref = O_element
FEATURE [App::DocumentObjectGroupPython] G4_THYMINE  # scripted group (container) (typed FeaturePython)
  Dunit = g/cm3
  Dvalue = 1.23
  Group = -> [H_element122,C_element132,N_element052,O_element114]
  conduct = 2
  density = 1
  expand = 3
  formula = G4_THYMINE
  name = G4_THYMINE
  specific = 4
FEATURE [App::DocumentObjectGroupPython] H_element123  label="H_element : 070"  # scripted group (container) (typed FeaturePython)
  n = 4
  ref = H_element
FEATURE [App::DocumentObjectGroupPython] C_element133  label="C_element : 078"  # scripted group (container) (typed FeaturePython)
  n = 4
  ref = C_element
FEATURE [App::DocumentObjectGroupPython] N_element053  label="N_element : 025"  # scripted group (container) (typed FeaturePython)
  n = 2
  ref = N_element
FEATURE [App::DocumentObjectGroupPython] O_element115  label="O_element : 068"  # scripted group (container) (typed FeaturePython)
  n = 2
  ref = O_element
FEATURE [App::DocumentObjectGroupPython] G4_URACIL  # scripted group (container) (typed FeaturePython)
  Dunit = g/cm3
  Dvalue = 1.32
  Group = -> [H_element123,C_element133,N_element053,O_element115]
  conduct = 2
  density = 1
  expand = 3
  formula = G4_URACIL
  name = G4_URACIL
  specific = 4
FEATURE [App::DocumentObjectGroupPython] H_element124  label="H_element : 071"  # scripted group (container) (typed FeaturePython)
  n = 4
  ref = H_element
FEATURE [App::DocumentObjectGroupPython] C_element134  label="C_element : 079"  # scripted group (container) (typed FeaturePython)
  n = 5
  ref = C_element
FEATURE [App::DocumentObjectGroupPython] N_element054  label="N_element : 026"  # scripted group (container) (typed FeaturePython)
  n = 5
  ref = N_element
FEATURE [App::DocumentObjectGroupPython] G4_DNA_ADENINE  # scripted group (container) (typed FeaturePython)
  Dunit = g/cm3
  Dvalue = 1
  Group = -> [H_element124,C_element134,N_element054]
  conduct = 2
  density = 1
  expand = 3
  formula = G4_DNA_ADENINE
  name = G4_DNA_ADENINE
  specific = 4
FEATURE [App::DocumentObjectGroupPython] H_element125  label="H_element : 072"  # scripted group (container) (typed FeaturePython)
  n = 4
  ref = H_element
FEATURE [App::DocumentObjectGroupPython] C_element135  label="C_element : 080"  # scripted group (container) (typed FeaturePython)
  n = 5
  ref = C_element
FEATURE [App::DocumentObjectGroupPython] N_element055  label="N_element : 027"  # scripted group (container) (typed FeaturePython)
  n = 5
  ref = N_element
FEATURE [App::DocumentObjectGroupPython] O_element116  label="O_element : 069"  # scripted group (container) (typed FeaturePython)
  n = 1
  ref = O_element
FEATURE [App::DocumentObjectGroupPython] G4_DNA_GUANINE  # scripted group (container) (typed FeaturePython)
  Dunit = g/cm3
  Dvalue = 1
  Group = -> [H_element125,C_element135,N_element055,O_element116]
  conduct = 2
  density = 1
  expand = 3
  formula = G4_DNA_GUANINE
  name = G4_DNA_GUANINE
  specific = 4
FEATURE [App::DocumentObjectGroupPython] H_element126  label="H_element : 073"  # scripted group (container) (typed FeaturePython)
  n = 4
  ref = H_element
FEATURE [App::DocumentObjectGroupPython] C_element136  label="C_element : 081"  # scripted group (container) (typed FeaturePython)
  n = 4
  ref = C_element
FEATURE [App::DocumentObjectGroupPython] N_element056  label="N_element : 028"  # scripted group (container) (typed FeaturePython)
  n = 3
  ref = N_element
FEATURE [App::DocumentObjectGroupPython] O_element117  label="O_element : 070"  # scripted group (container) (typed FeaturePython)
  n = 1
  ref = O_element
FEATURE [App::DocumentObjectGroupPython] G4_DNA_CYTOSINE  # scripted group (container) (typed FeaturePython)
  Dunit = g/cm3
  Dvalue = 1
  Group = -> [H_element126,C_element136,N_element056,O_element117]
  conduct = 2
  density = 1
  expand = 3
  formula = G4_DNA_CYTOSINE
  name = G4_DNA_CYTOSINE
  specific = 4
FEATURE [App::DocumentObjectGroupPython] H_element127  label="H_element : 074"  # scripted group (container) (typed FeaturePython)
  n = 5
  ref = H_element
FEATURE [App::DocumentObjectGroupPython] C_element137  label="C_element : 082"  # scripted group (container) (typed FeaturePython)
  n = 5
  ref = C_element
FEATURE [App::DocumentObjectGroupPython] N_element057  label="N_element : 029"  # scripted group (container) (typed FeaturePython)
  n = 2
  ref = N_element
FEATURE [App::DocumentObjectGroupPython] O_element118  label="O_element : 071"  # scripted group (container) (typed FeaturePython)
  n = 2
  ref = O_element
FEATURE [App::DocumentObjectGroupPython] G4_DNA_THYMINE  # scripted group (container) (typed FeaturePython)
  Dunit = g/cm3
  Dvalue = 1
  Group = -> [H_element127,C_element137,N_element057,O_element118]
  conduct = 2
  density = 1
  expand = 3
  formula = G4_DNA_THYMINE
  name = G4_DNA_THYMINE
  specific = 4
FEATURE [App::DocumentObjectGroupPython] H_element128  label="H_element : 075"  # scripted group (container) (typed FeaturePython)
  n = 3
  ref = H_element
FEATURE [App::DocumentObjectGroupPython] C_element138  label="C_element : 083"  # scripted group (container) (typed FeaturePython)
  n = 4
  ref = C_element
FEATURE [App::DocumentObjectGroupPython] N_element058  label="N_element : 030"  # scripted group (container) (typed FeaturePython)
  n = 2
  ref = N_element
FEATURE [App::DocumentObjectGroupPython] O_element119  label="O_element : 072"  # scripted group (container) (typed FeaturePython)
  n = 2
  ref = O_element
FEATURE [App::DocumentObjectGroupPython] G4_DNA_URACIL  # scripted group (container) (typed FeaturePython)
  Dunit = g/cm3
  Dvalue = 1
  Group = -> [H_element128,C_element138,N_element058,O_element119]
  conduct = 2
  density = 1
  expand = 3
  formula = G4_DNA_URACIL
  name = G4_DNA_URACIL
  specific = 4
FEATURE [App::DocumentObjectGroupPython] H_element129  label="H_element : 076"  # scripted group (container) (typed FeaturePython)
  n = 10
  ref = H_element
FEATURE [App::DocumentObjectGroupPython] C_element139  label="C_element : 084"  # scripted group (container) (typed FeaturePython)
  n = 10
  ref = C_element
FEATURE [App::DocumentObjectGroupPython] N_element059  label="N_element : 031"  # scripted group (container) (typed FeaturePython)
  n = 5
  ref = N_element
FEATURE [App::DocumentObjectGroupPython] O_element120  label="O_element : 073"  # scripted group (container) (typed FeaturePython)
  n = 4
  ref = O_element
FEATURE [App::DocumentObjectGroupPython] G4_DNA_ADENOSINE  # scripted group (container) (typed FeaturePython)
  Dunit = g/cm3
  Dvalue = 1
  Group = -> [H_element129,C_element139,N_element059,O_element120]
  conduct = 2
  density = 1
  expand = 3
  formula = G4_DNA_ADENOSINE
  name = G4_DNA_ADENOSINE
  specific = 4
FEATURE [App::DocumentObjectGroupPython] H_element130  label="H_element : 077"  # scripted group (container) (typed FeaturePython)
  n = 10
  ref = H_element
FEATURE [App::DocumentObjectGroupPython] C_element140  label="C_element : 085"  # scripted group (container) (typed FeaturePython)
  n = 10
  ref = C_element
FEATURE [App::DocumentObjectGroupPython] N_element060  label="N_element : 032"  # scripted group (container) (typed FeaturePython)
  n = 5
  ref = N_element
FEATURE [App::DocumentObjectGroupPython] O_element121  label="O_element : 074"  # scripted group (container) (typed FeaturePython)
  n = 5
  ref = O_element
FEATURE [App::DocumentObjectGroupPython] G4_DNA_GUANOSINE  # scripted group (container) (typed FeaturePython)
  Dunit = g/cm3
  Dvalue = 1
  Group = -> [H_element130,C_element140,N_element060,O_element121]
  conduct = 2
  density = 1
  expand = 3
  formula = G4_DNA_GUANOSINE
  name = G4_DNA_GUANOSINE
  specific = 4
FEATURE [App::DocumentObjectGroupPython] H_element131  label="H_element : 078"  # scripted group (container) (typed FeaturePython)
  n = 10
  ref = H_element
FEATURE [App::DocumentObjectGroupPython] C_element141  label="C_element : 086"  # scripted group (container) (typed FeaturePython)
  n = 9
  ref = C_element
FEATURE [App::DocumentObjectGroupPython] N_element061  label="N_element : 033"  # scripted group (container) (typed FeaturePython)
  n = 3
  ref = N_element
FEATURE [App::DocumentObjectGroupPython] O_element122  label="O_element : 075"  # scripted group (container) (typed FeaturePython)
  n = 5
  ref = O_element
FEATURE [App::DocumentObjectGroupPython] G4_DNA_CYTIDINE  # scripted group (container) (typed FeaturePython)
  Dunit = g/cm3
  Dvalue = 1
  Group = -> [H_element131,C_element141,N_element061,O_element122]
  conduct = 2
  density = 1
  expand = 3
  formula = G4_DNA_CYTIDINE
  name = G4_DNA_CYTIDINE
  specific = 4
FEATURE [App::DocumentObjectGroupPython] H_element132  label="H_element : 079"  # scripted group (container) (typed FeaturePython)
  n = 9
  ref = H_element
FEATURE [App::DocumentObjectGroupPython] C_element142  label="C_element : 087"  # scripted group (container) (typed FeaturePython)
  n = 9
  ref = C_element
FEATURE [App::DocumentObjectGroupPython] N_element062  label="N_element : 034"  # scripted group (container) (typed FeaturePython)
  n = 2
  ref = N_element
FEATURE [App::DocumentObjectGroupPython] O_element123  label="O_element : 076"  # scripted group (container) (typed FeaturePython)
  n = 6
  ref = O_element
FEATURE [App::DocumentObjectGroupPython] G4_DNA_URIDINE  # scripted group (container) (typed FeaturePython)
  Dunit = g/cm3
  Dvalue = 1
  Group = -> [H_element132,C_element142,N_element062,O_element123]
  conduct = 2
  density = 1
  expand = 3
  formula = G4_DNA_URIDINE
  name = G4_DNA_URIDINE
  specific = 4
FEATURE [App::DocumentObjectGroupPython] H_element133  label="H_element : 080"  # scripted group (container) (typed FeaturePython)
  n = 11
  ref = H_element
FEATURE [App::DocumentObjectGroupPython] C_element143  label="C_element : 088"  # scripted group (container) (typed FeaturePython)
  n = 10
  ref = C_element
FEATURE [App::DocumentObjectGroupPython] N_element063  label="N_element : 035"  # scripted group (container) (typed FeaturePython)
  n = 2
  ref = N_element
FEATURE [App::DocumentObjectGroupPython] O_element124  label="O_element : 077"  # scripted group (container) (typed FeaturePython)
  n = 6
  ref = O_element
FEATURE [App::DocumentObjectGroupPython] G4_DNA_METHYLURIDINE  # scripted group (container) (typed FeaturePython)
  Dunit = g/cm3
  Dvalue = 1
  Group = -> [H_element133,C_element143,N_element063,O_element124]
  conduct = 2
  density = 1
  expand = 3
  formula = G4_DNA_METHYLURIDINE
  name = G4_DNA_METHYLURIDINE
  specific = 4
FEATURE [App::DocumentObjectGroupPython] P_element014  label="P_element : 003"  # scripted group (container) (typed FeaturePython)
  n = 1
  ref = P_element
FEATURE [App::DocumentObjectGroupPython] O_element125  label="O_element : 078"  # scripted group (container) (typed FeaturePython)
  n = 3
  ref = O_element
FEATURE [App::DocumentObjectGroupPython] G4_DNA_MONOPHOSPHATE  # scripted group (container) (typed FeaturePython)
  Dunit = g/cm3
  Dvalue = 1
  Group = -> [P_element014,O_element125]
  conduct = 2
  density = 1
  expand = 3
  formula = G4_DNA_MONOPHOSPHATE
  name = G4_DNA_MONOPHOSPHATE
  specific = 4
FEATURE [App::DocumentObjectGroupPython] H_element134  label="H_element : 081"  # scripted group (container) (typed FeaturePython)
  n = 10
  ref = H_element
FEATURE [App::DocumentObjectGroupPython] C_element144  label="C_element : 089"  # scripted group (container) (typed FeaturePython)
  n = 10
  ref = C_element
FEATURE [App::DocumentObjectGroupPython] N_element064  label="N_element : 036"  # scripted group (container) (typed FeaturePython)
  n = 5
  ref = N_element
FEATURE [App::DocumentObjectGroupPython] O_element126  label="O_element : 079"  # scripted group (container) (typed FeaturePython)
  n = 7
  ref = O_element
FEATURE [App::DocumentObjectGroupPython] P_element015  label="P_element : 004"  # scripted group (container) (typed FeaturePython)
  n = 1
  ref = P_element
FEATURE [App::DocumentObjectGroupPython] G4_DNA_A  # scripted group (container) (typed FeaturePython)
  Dunit = g/cm3
  Dvalue = 1
  Group = -> [H_element134,C_element144,N_element064,O_element126,P_element015]
  conduct = 2
  density = 1
  expand = 3
  formula = G4_DNA_A
  name = G4_DNA_A
  specific = 4
FEATURE [App::DocumentObjectGroupPython] H_element135  label="H_element : 082"  # scripted group (container) (typed FeaturePython)
  n = 10
  ref = H_element
FEATURE [App::DocumentObjectGroupPython] C_element145  label="C_element : 090"  # scripted group (container) (typed FeaturePython)
  n = 10
  ref = C_element
FEATURE [App::DocumentObjectGroupPython] N_element065  label="N_element : 037"  # scripted group (container) (typed FeaturePython)
  n = 5
  ref = N_element
FEATURE [App::DocumentObjectGroupPython] O_element127  label="O_element : 8"  # scripted group (container) (typed FeaturePython)
  n = 8
  ref = O_element
FEATURE [App::DocumentObjectGroupPython] P_element016  label="P_element : 005"  # scripted group (container) (typed FeaturePython)
  n = 1
  ref = P_element
FEATURE [App::DocumentObjectGroupPython] G4_DNA_G  # scripted group (container) (typed FeaturePython)
  Dunit = g/cm3
  Dvalue = 1
  Group = -> [H_element135,C_element145,N_element065,O_element127,P_element016]
  conduct = 2
  density = 1
  expand = 3
  formula = G4_DNA_G
  name = G4_DNA_G
  specific = 4
FEATURE [App::DocumentObjectGroupPython] H_element136  label="H_element : 083"  # scripted group (container) (typed FeaturePython)
  n = 10
  ref = H_element
FEATURE [App::DocumentObjectGroupPython] C_element146  label="C_element : 091"  # scripted group (container) (typed FeaturePython)
  n = 9
  ref = C_element
FEATURE [App::DocumentObjectGroupPython] N_element066  label="N_element : 038"  # scripted group (container) (typed FeaturePython)
  n = 3
  ref = N_element
FEATURE [App::DocumentObjectGroupPython] O_element128  label="O_element : 080"  # scripted group (container) (typed FeaturePython)
  n = 8
  ref = O_element
FEATURE [App::DocumentObjectGroupPython] P_element017  label="P_element : 006"  # scripted group (container) (typed FeaturePython)
  n = 1
  ref = P_element
FEATURE [App::DocumentObjectGroupPython] G4_DNA_C  # scripted group (container) (typed FeaturePython)
  Dunit = g/cm3
  Dvalue = 1
  Group = -> [H_element136,C_element146,N_element066,O_element128,P_element017]
  conduct = 2
  density = 1
  expand = 3
  formula = G4_DNA_C
  name = G4_DNA_C
  specific = 4
FEATURE [App::DocumentObjectGroupPython] H_element137  label="H_element : 084"  # scripted group (container) (typed FeaturePython)
  n = 9
  ref = H_element
FEATURE [App::DocumentObjectGroupPython] C_element147  label="C_element : 092"  # scripted group (container) (typed FeaturePython)
  n = 9
  ref = C_element
FEATURE [App::DocumentObjectGroupPython] N_element067  label="N_element : 039"  # scripted group (container) (typed FeaturePython)
  n = 2
  ref = N_element
FEATURE [App::DocumentObjectGroupPython] O_element129  label="O_element : 9"  # scripted group (container) (typed FeaturePython)
  n = 9
  ref = O_element
FEATURE [App::DocumentObjectGroupPython] P_element018  label="P_element : 007"  # scripted group (container) (typed FeaturePython)
  n = 1
  ref = P_element
FEATURE [App::DocumentObjectGroupPython] G4_DNA_U  # scripted group (container) (typed FeaturePython)
  Dunit = g/cm3
  Dvalue = 1
  Group = -> [H_element137,C_element147,N_element067,O_element129,P_element018]
  conduct = 2
  density = 1
  expand = 3
  formula = G4_DNA_U
  name = G4_DNA_U
  specific = 4
FEATURE [App::DocumentObjectGroupPython] H_element138  label="H_element : 085"  # scripted group (container) (typed FeaturePython)
  n = 11
  ref = H_element
FEATURE [App::DocumentObjectGroupPython] C_element148  label="C_element : 093"  # scripted group (container) (typed FeaturePython)
  n = 10
  ref = C_element
FEATURE [App::DocumentObjectGroupPython] N_element068  label="N_element : 040"  # scripted group (container) (typed FeaturePython)
  n = 2
  ref = N_element
FEATURE [App::DocumentObjectGroupPython] O_element130  label="O_element : 081"  # scripted group (container) (typed FeaturePython)
  n = 9
  ref = O_element
FEATURE [App::DocumentObjectGroupPython] P_element019  label="P_element : 008"  # scripted group (container) (typed FeaturePython)
  n = 1
  ref = P_element
FEATURE [App::DocumentObjectGroupPython] G4_DNA_MU  # scripted group (container) (typed FeaturePython)
  Dunit = g/cm3
  Dvalue = 1
  Group = -> [H_element138,C_element148,N_element068,O_element130,P_element019]
  conduct = 2
  density = 1
  expand = 3
  formula = G4_DNA_MU
  name = G4_DNA_MU
  specific = 4
FEATURE [App::DocumentObjectGroupPython] BioChemical  # scripted group (container) (typed FeaturePython)
  Group = -> [G4_CYTOSINE,G4_THYMINE,G4_URACIL,G4_DNA_ADENINE,G4_DNA_GUANINE,G4_DNA_CYTOSINE,G4_DNA_THYMINE,G4_DNA_URACIL,G4_DNA_ADENOSINE,G4_DNA_GUANOSINE,G4_DNA_CYTIDINE,G4_DNA_URIDINE,G4_DNA_METHYLURIDINE,G4_DNA_MONOPHOSPHATE,G4_DNA_A,G4_DNA_G,G4_DNA_C,G4_DNA_U,G4_DNA_MU]
FEATURE [App::DocumentObjectGroupPython] G4Materials  # scripted group (container) (typed FeaturePython)
  Group = -> [NIST,Element,HEP,Space,BioChemical]
  version = 1
FEATURE [App::DocumentObjectGroupPython] Geant4  # scripted group (container) (typed FeaturePython)
  Group = -> [G4Isotopes,G4Elements,G4Materials]
FEATURE [Part::FeaturePython] GDMLBox_WorldBox  # WARN: FeaturePython — macro-defined, semantics opaque (R4)
  lunit = 2
  material = 8
  x = 114.01
  y = 147.706
  z = 147.706
FEATURE [App::DocumentObjectGroupPython] G4_Pyrex_Glass001  label="G4_Pyrex_Glass : 1.000"  # scripted group (container) (typed FeaturePython)
  n = 1
FEATURE [App::DocumentObjectGroupPython] Glass  # scripted group (container) (typed FeaturePython)
  Dunit = g/cm3
  Dvalue = 1.032
  Group = -> [G4_Pyrex_Glass001]
  RINDEX = RINDEXLAR
  conduct = 2
  density = 1
  expand = 3
  name = Glass
  specific = 4
FEATURE [App::DocumentObjectGroupPython] G4_CESIUM_IODIDE  label="G4_CESIUM_IODIDE : 1.000"  # scripted group (container) (typed FeaturePython)
  n = 1
FEATURE [App::DocumentObjectGroupPython] LYSO  # scripted group (container) (typed FeaturePython)
  ABSLENGTH = ABSLENGTHLAR
  Dunit = g/cm3
  Dvalue = 7.1
  FASTCOMPONENT = SCINTLAR
  FASTTIMECONSTANT = FTC
  Group = -> [G4_CESIUM_IODIDE]
  RAYLEIGH = RAYLEIGHLAR
  REEMISSIONPROB = SCINTLAR
  RESOLUTIONSCALE = RS
  RINDEX = RINDEXLAR
  SCINTILLATIONYIELD = SY
  SLOWCOMPONENT = SCINTLAR
  SLOWTIMECONSTANT = STC
  YIELDRATIO = YR
  conduct = 2
  density = 1
  expand = 3
  name = LYSO
  specific = 4
FEATURE [App::DocumentObjectGroupPython] Materials  # scripted group (container) (typed FeaturePython)
  Group = -> [Air,Geant4,Glass,LYSO]
FEATURE [Part::FeaturePython] GDMLSphere_Sphere  # WARN: FeaturePython — macro-defined, semantics opaque (R4)
  aunit = 1
  deltaphi = 360
  deltatheta = 180
  lunit = 2
  material = 164
  rmax = 5
  rmin = 0
  startphi = 0
  starttheta = 0
FEATURE [App::Part] LV_Sphere
  Group = -> [GDMLSphere_Sphere]
  Origin = -> Origin004
FEATURE [Part::FeaturePython] GDMLBox_Box004  # WARN: FeaturePython — macro-defined, semantics opaque (R4)
  CopyNumber = 1
  Placement = pos=(0,0,37.85) rot=(0,0,1;0rad)
  lunit = 2
  material = 1
  x = 27.8
  y = 27.8
  z = 8
FEATURE [App::Link] Link_GDMLBox_Box004
  CopyNumber = 2
  LinkPlacement = pos=(26.764,0,26.764) rot=(0,1,0;0.785398rad)
  LinkedObject = -> GDMLBox_Box004
  Placement = pos=(26.764,0,26.764) rot=(0,1,0;0.785398rad)
FEATURE [App::Link] Link_GDMLBox_Box004001
  CopyNumber = 3
  LinkPlacement = pos=(37.85,0,7.1e-15) rot=(0,1,0;1.5708rad)
  LinkedObject = -> GDMLBox_Box004
  Placement = pos=(37.85,0,7.1e-15) rot=(0,1,0;1.5708rad)
FEATURE [App::Link] Link_GDMLBox_Box004002
  CopyNumber = 4
  LinkPlacement = pos=(26.764,0,-26.764) rot=(0,1,0;2.35619rad)
  LinkedObject = -> GDMLBox_Box004
  Placement = pos=(26.764,0,-26.764) rot=(0,1,0;2.35619rad)
FEATURE [App::Link] Link_GDMLBox_Box004003
  CopyNumber = 5
  LinkPlacement = pos=(4.6e-15,0,-37.85) rot=(0,1,0;3.14159rad)
  LinkedObject = -> GDMLBox_Box004
  Placement = pos=(4.6e-15,0,-37.85) rot=(0,1,0;3.14159rad)
FEATURE [App::Link] Link_GDMLBox_Box004004
  CopyNumber = 6
  LinkPlacement = pos=(-26.764,0,-26.764) rot=(0,1,0;3.92699rad)
  LinkedObject = -> GDMLBox_Box004
  Placement = pos=(-26.764,0,-26.764) rot=(0,1,0;3.92699rad)
FEATURE [App::Link] Link_GDMLBox_Box004005
  CopyNumber = 7
  LinkPlacement = pos=(-37.85,0,-7.1e-15) rot=(0,1,0;4.71239rad)
  LinkedObject = -> GDMLBox_Box004
  Placement = pos=(-37.85,0,-7.1e-15) rot=(0,1,0;4.71239rad)
FEATURE [App::Link] Link_GDMLBox_Box004006
  CopyNumber = 8
  LinkPlacement = pos=(-26.764,0,26.764) rot=(0,1,0;5.49779rad)
  LinkedObject = -> GDMLBox_Box004
  Placement = pos=(-26.764,0,26.764) rot=(0,1,0;5.49779rad)
FEATURE [App::Part] Array002001
  Group = -> [GDMLBox_Box004,Link_GDMLBox_Box004,Link_GDMLBox_Box004001,Link_GDMLBox_Box004002,Link_GDMLBox_Box004003,Link_GDMLBox_Box004004,Link_GDMLBox_Box004005,Link_GDMLBox_Box004006]
  Origin = -> Origin005
FEATURE [App::Part] Part001
  Group = -> [Array002001]
  Origin = -> Origin002
  SkinSurface = 0
FEATURE [App::Link] Link_Child_Array
  CopyNumber = 10
  LinkPlacement = pos=(26.764,0,26.764) rot=(0,1,0;0.785398rad)
  LinkedObject = -> Child_Array
  Placement = pos=(26.764,0,26.764) rot=(0,1,0;0.785398rad)
FEATURE [App::Link] Link_Child_Array001
  CopyNumber = 11
  LinkPlacement = pos=(37.85,0,7.1e-15) rot=(0,1,0;1.5708rad)
  LinkedObject = -> Child_Array
  Placement = pos=(37.85,0,7.1e-15) rot=(0,1,0;1.5708rad)
FEATURE [App::Link] Link_Child_Array002
  CopyNumber = 12
  LinkPlacement = pos=(26.764,0,-26.764) rot=(0,1,0;2.35619rad)
  LinkedObject = -> Child_Array
  Placement = pos=(26.764,0,-26.764) rot=(0,1,0;2.35619rad)
FEATURE [App::Link] Link_Child_Array003
  CopyNumber = 13
  LinkPlacement = pos=(4.6e-15,0,-37.85) rot=(0,1,0;3.14159rad)
  LinkedObject = -> Child_Array
  Placement = pos=(4.6e-15,0,-37.85) rot=(0,1,0;3.14159rad)
FEATURE [App::Link] Link_Child_Array004
  CopyNumber = 14
  LinkPlacement = pos=(-26.764,0,-26.764) rot=(0,1,0;3.92699rad)
  LinkedObject = -> Child_Array
  Placement = pos=(-26.764,0,-26.764) rot=(0,1,0;3.92699rad)
FEATURE [App::Link] Link_Child_Array005
  CopyNumber = 15
  LinkPlacement = pos=(-37.85,0,-7.1e-15) rot=(0,1,0;4.71239rad)
  LinkedObject = -> Child_Array
  Placement = pos=(-37.85,0,-7.1e-15) rot=(0,1,0;4.71239rad)
FEATURE [App::Link] Link_Child_Array006
  CopyNumber = 16
  LinkPlacement = pos=(-26.764,0,26.764) rot=(0,1,0;5.49779rad)
  LinkedObject = -> Child_Array
  Placement = pos=(-26.764,0,26.764) rot=(0,1,0;5.49779rad)
FEATURE [Part::FeaturePython] GDMLBox_Box005  # WARN: FeaturePython — macro-defined, semantics opaque (R4)
  CopyNumber = 17
  Placement = pos=(-11.99,-11.99,5) rot=(0,0,1;0rad)
  lunit = 2
  material = 0
  x = 3.22
  y = 3.22
  z = 2
FEATURE [App::Link] Link_GDMLBox_Box005
  CopyNumber = 18
  LinkPlacement = pos=(-11.99,-8.59,5) rot=(0,0,1;0rad)
  LinkedObject = -> GDMLBox_Box005
  Placement = pos=(-11.99,-8.59,5) rot=(0,0,1;0rad)
FEATURE [App::Link] Link_GDMLBox_Box005001
  CopyNumber = 19
  LinkPlacement = pos=(-11.99,-5.19,5) rot=(0,0,1;0rad)
  LinkedObject = -> GDMLBox_Box005
  Placement = pos=(-11.99,-5.19,5) rot=(0,0,1;0rad)
FEATURE [App::Link] Link_GDMLBox_Box005002
  CopyNumber = 20
  LinkPlacement = pos=(-11.99,-1.79,5) rot=(0,0,1;0rad)
  LinkedObject = -> GDMLBox_Box005
  Placement = pos=(-11.99,-1.79,5) rot=(0,0,1;0rad)
FEATURE [App::Link] Link_GDMLBox_Box005003
  CopyNumber = 21
  LinkPlacement = pos=(-11.99,1.61,5) rot=(0,0,1;0rad)
  LinkedObject = -> GDMLBox_Box005
  Placement = pos=(-11.99,1.61,5) rot=(0,0,1;0rad)
FEATURE [App::Link] Link_GDMLBox_Box005004
  CopyNumber = 22
  LinkPlacement = pos=(-11.99,5.01,5) rot=(0,0,1;0rad)
  LinkedObject = -> GDMLBox_Box005
  Placement = pos=(-11.99,5.01,5) rot=(0,0,1;0rad)
FEATURE [App::Link] Link_GDMLBox_Box005005
  CopyNumber = 23
  LinkPlacement = pos=(-11.99,8.41,5) rot=(0,0,1;0rad)
  LinkedObject = -> GDMLBox_Box005
  Placement = pos=(-11.99,8.41,5) rot=(0,0,1;0rad)
FEATURE [App::Link] Link_GDMLBox_Box005006
  CopyNumber = 24
  LinkPlacement = pos=(-11.99,11.81,5) rot=(0,0,1;0rad)
  LinkedObject = -> GDMLBox_Box005
  Placement = pos=(-11.99,11.81,5) rot=(0,0,1;0rad)
FEATURE [App::Link] Link_GDMLBox_Box005007
  CopyNumber = 25
  LinkPlacement = pos=(-8.59,-11.99,5) rot=(0,0,1;0rad)
  LinkedObject = -> GDMLBox_Box005
  Placement = pos=(-8.59,-11.99,5) rot=(0,0,1;0rad)
FEATURE [App::Link] Link_GDMLBox_Box005008
  CopyNumber = 26
  LinkPlacement = pos=(-8.59,-8.59,5) rot=(0,0,1;0rad)
  LinkedObject = -> GDMLBox_Box005
  Placement = pos=(-8.59,-8.59,5) rot=(0,0,1;0rad)
FEATURE [App::Link] Link_GDMLBox_Box005009
  CopyNumber = 27
  LinkPlacement = pos=(-8.59,-5.19,5) rot=(0,0,1;0rad)
  LinkedObject = -> GDMLBox_Box005
  Placement = pos=(-8.59,-5.19,5) rot=(0,0,1;0rad)
FEATURE [App::Link] Link_GDMLBox_Box005010
  CopyNumber = 28
  LinkPlacement = pos=(-8.59,-1.79,5) rot=(0,0,1;0rad)
  LinkedObject = -> GDMLBox_Box005
  Placement = pos=(-8.59,-1.79,5) rot=(0,0,1;0rad)
FEATURE [App::Link] Link_GDMLBox_Box005011
  CopyNumber = 29
  LinkPlacement = pos=(-8.59,1.61,5) rot=(0,0,1;0rad)
  LinkedObject = -> GDMLBox_Box005
  Placement = pos=(-8.59,1.61,5) rot=(0,0,1;0rad)
FEATURE [App::Link] Link_GDMLBox_Box005012
  CopyNumber = 30
  LinkPlacement = pos=(-8.59,5.01,5) rot=(0,0,1;0rad)
  LinkedObject = -> GDMLBox_Box005
  Placement = pos=(-8.59,5.01,5) rot=(0,0,1;0rad)
FEATURE [App::Link] Link_GDMLBox_Box005013
  CopyNumber = 31
  LinkPlacement = pos=(-8.59,8.41,5) rot=(0,0,1;0rad)
  LinkedObject = -> GDMLBox_Box005
  Placement = pos=(-8.59,8.41,5) rot=(0,0,1;0rad)
FEATURE [App::Link] Link_GDMLBox_Box005014
  CopyNumber = 32
  LinkPlacement = pos=(-8.59,11.81,5) rot=(0,0,1;0rad)
  LinkedObject = -> GDMLBox_Box005
  Placement = pos=(-8.59,11.81,5) rot=(0,0,1;0rad)
FEATURE [App::Link] Link_GDMLBox_Box005015
  CopyNumber = 33
  LinkPlacement = pos=(-5.19,-11.99,5) rot=(0,0,1;0rad)
  LinkedObject = -> GDMLBox_Box005
  Placement = pos=(-5.19,-11.99,5) rot=(0,0,1;0rad)
FEATURE [App::Link] Link_GDMLBox_Box005016
  CopyNumber = 34
  LinkPlacement = pos=(-5.19,-8.59,5) rot=(0,0,1;0rad)
  LinkedObject = -> GDMLBox_Box005
  Placement = pos=(-5.19,-8.59,5) rot=(0,0,1;0rad)
FEATURE [App::Link] Link_GDMLBox_Box005017
  CopyNumber = 35
  LinkPlacement = pos=(-5.19,-5.19,5) rot=(0,0,1;0rad)
  LinkedObject = -> GDMLBox_Box005
  Placement = pos=(-5.19,-5.19,5) rot=(0,0,1;0rad)
FEATURE [App::Link] Link_GDMLBox_Box005018
  CopyNumber = 36
  LinkPlacement = pos=(-5.19,-1.79,5) rot=(0,0,1;0rad)
  LinkedObject = -> GDMLBox_Box005
  Placement = pos=(-5.19,-1.79,5) rot=(0,0,1;0rad)
FEATURE [App::Link] Link_GDMLBox_Box005019
  CopyNumber = 37
  LinkPlacement = pos=(-5.19,1.61,5) rot=(0,0,1;0rad)
  LinkedObject = -> GDMLBox_Box005
  Placement = pos=(-5.19,1.61,5) rot=(0,0,1;0rad)
FEATURE [App::Link] Link_GDMLBox_Box005020
  CopyNumber = 38
  LinkPlacement = pos=(-5.19,5.01,5) rot=(0,0,1;0rad)
  LinkedObject = -> GDMLBox_Box005
  Placement = pos=(-5.19,5.01,5) rot=(0,0,1;0rad)
FEATURE [App::Link] Link_GDMLBox_Box005021
  CopyNumber = 39
  LinkPlacement = pos=(-5.19,8.41,5) rot=(0,0,1;0rad)
  LinkedObject = -> GDMLBox_Box005
  Placement = pos=(-5.19,8.41,5) rot=(0,0,1;0rad)
FEATURE [App::Link] Link_GDMLBox_Box005022
  CopyNumber = 40
  LinkPlacement = pos=(-5.19,11.81,5) rot=(0,0,1;0rad)
  LinkedObject = -> GDMLBox_Box005
  Placement = pos=(-5.19,11.81,5) rot=(0,0,1;0rad)
FEATURE [App::Link] Link_GDMLBox_Box005023
  CopyNumber = 41
  LinkPlacement = pos=(-1.79,-11.99,5) rot=(0,0,1;0rad)
  LinkedObject = -> GDMLBox_Box005
  Placement = pos=(-1.79,-11.99,5) rot=(0,0,1;0rad)
FEATURE [App::Link] Link_GDMLBox_Box005024
  CopyNumber = 42
  LinkPlacement = pos=(-1.79,-8.59,5) rot=(0,0,1;0rad)
  LinkedObject = -> GDMLBox_Box005
  Placement = pos=(-1.79,-8.59,5) rot=(0,0,1;0rad)
FEATURE [App::Link] Link_GDMLBox_Box005025
  CopyNumber = 43
  LinkPlacement = pos=(-1.79,-5.19,5) rot=(0,0,1;0rad)
  LinkedObject = -> GDMLBox_Box005
  Placement = pos=(-1.79,-5.19,5) rot=(0,0,1;0rad)
FEATURE [App::Link] Link_GDMLBox_Box005026
  CopyNumber = 44
  LinkPlacement = pos=(-1.79,-1.79,5) rot=(0,0,1;0rad)
  LinkedObject = -> GDMLBox_Box005
  Placement = pos=(-1.79,-1.79,5) rot=(0,0,1;0rad)
FEATURE [App::Link] Link_GDMLBox_Box005027
  CopyNumber = 45
  LinkPlacement = pos=(-1.79,1.61,5) rot=(0,0,1;0rad)
  LinkedObject = -> GDMLBox_Box005
  Placement = pos=(-1.79,1.61,5) rot=(0,0,1;0rad)
FEATURE [App::Link] Link_GDMLBox_Box005028
  CopyNumber = 46
  LinkPlacement = pos=(-1.79,5.01,5) rot=(0,0,1;0rad)
  LinkedObject = -> GDMLBox_Box005
  Placement = pos=(-1.79,5.01,5) rot=(0,0,1;0rad)
FEATURE [App::Link] Link_GDMLBox_Box005029
  CopyNumber = 47
  LinkPlacement = pos=(-1.79,8.41,5) rot=(0,0,1;0rad)
  LinkedObject = -> GDMLBox_Box005
  Placement = pos=(-1.79,8.41,5) rot=(0,0,1;0rad)
FEATURE [App::Link] Link_GDMLBox_Box005030
  CopyNumber = 48
  LinkPlacement = pos=(-1.79,11.81,5) rot=(0,0,1;0rad)
  LinkedObject = -> GDMLBox_Box005
  Placement = pos=(-1.79,11.81,5) rot=(0,0,1;0rad)
FEATURE [App::Link] Link_GDMLBox_Box005031
  CopyNumber = 49
  LinkPlacement = pos=(1.61,-11.99,5) rot=(0,0,1;0rad)
  LinkedObject = -> GDMLBox_Box005
  Placement = pos=(1.61,-11.99,5) rot=(0,0,1;0rad)
FEATURE [App::Link] Link_GDMLBox_Box005032
  CopyNumber = 50
  LinkPlacement = pos=(1.61,-8.59,5) rot=(0,0,1;0rad)
  LinkedObject = -> GDMLBox_Box005
  Placement = pos=(1.61,-8.59,5) rot=(0,0,1;0rad)
FEATURE [App::Link] Link_GDMLBox_Box005033
  CopyNumber = 51
  LinkPlacement = pos=(1.61,-5.19,5) rot=(0,0,1;0rad)
  LinkedObject = -> GDMLBox_Box005
  Placement = pos=(1.61,-5.19,5) rot=(0,0,1;0rad)
FEATURE [App::Link] Link_GDMLBox_Box005034
  CopyNumber = 52
  LinkPlacement = pos=(1.61,-1.79,5) rot=(0,0,1;0rad)
  LinkedObject = -> GDMLBox_Box005
  Placement = pos=(1.61,-1.79,5) rot=(0,0,1;0rad)
FEATURE [App::Link] Link_GDMLBox_Box005035
  CopyNumber = 53
  LinkPlacement = pos=(1.61,1.61,5) rot=(0,0,1;0rad)
  LinkedObject = -> GDMLBox_Box005
  Placement = pos=(1.61,1.61,5) rot=(0,0,1;0rad)
FEATURE [App::Link] Link_GDMLBox_Box005036
  CopyNumber = 54
  LinkPlacement = pos=(1.61,5.01,5) rot=(0,0,1;0rad)
  LinkedObject = -> GDMLBox_Box005
  Placement = pos=(1.61,5.01,5) rot=(0,0,1;0rad)
FEATURE [App::Link] Link_GDMLBox_Box005037
  CopyNumber = 55
  LinkPlacement = pos=(1.61,8.41,5) rot=(0,0,1;0rad)
  LinkedObject = -> GDMLBox_Box005
  Placement = pos=(1.61,8.41,5) rot=(0,0,1;0rad)
FEATURE [App::Link] Link_GDMLBox_Box005038
  CopyNumber = 56
  LinkPlacement = pos=(1.61,11.81,5) rot=(0,0,1;0rad)
  LinkedObject = -> GDMLBox_Box005
  Placement = pos=(1.61,11.81,5) rot=(0,0,1;0rad)
FEATURE [App::Link] Link_GDMLBox_Box005039
  CopyNumber = 57
  LinkPlacement = pos=(5.01,-11.99,5) rot=(0,0,1;0rad)
  LinkedObject = -> GDMLBox_Box005
  Placement = pos=(5.01,-11.99,5) rot=(0,0,1;0rad)
FEATURE [App::Link] Link_GDMLBox_Box005040
  CopyNumber = 58
  LinkPlacement = pos=(5.01,-8.59,5) rot=(0,0,1;0rad)
  LinkedObject = -> GDMLBox_Box005
  Placement = pos=(5.01,-8.59,5) rot=(0,0,1;0rad)
FEATURE [App::Link] Link_GDMLBox_Box005041
  CopyNumber = 59
  LinkPlacement = pos=(5.01,-5.19,5) rot=(0,0,1;0rad)
  LinkedObject = -> GDMLBox_Box005
  Placement = pos=(5.01,-5.19,5) rot=(0,0,1;0rad)
FEATURE [App::Link] Link_GDMLBox_Box005042
  CopyNumber = 60
  LinkPlacement = pos=(5.01,-1.79,5) rot=(0,0,1;0rad)
  LinkedObject = -> GDMLBox_Box005
  Placement = pos=(5.01,-1.79,5) rot=(0,0,1;0rad)
FEATURE [App::Link] Link_GDMLBox_Box005043
  CopyNumber = 61
  LinkPlacement = pos=(5.01,1.61,5) rot=(0,0,1;0rad)
  LinkedObject = -> GDMLBox_Box005
  Placement = pos=(5.01,1.61,5) rot=(0,0,1;0rad)
FEATURE [App::Link] Link_GDMLBox_Box005044
  CopyNumber = 62
  LinkPlacement = pos=(5.01,5.01,5) rot=(0,0,1;0rad)
  LinkedObject = -> GDMLBox_Box005
  Placement = pos=(5.01,5.01,5) rot=(0,0,1;0rad)
FEATURE [App::Link] Link_GDMLBox_Box005045
  CopyNumber = 63
  LinkPlacement = pos=(5.01,8.41,5) rot=(0,0,1;0rad)
  LinkedObject = -> GDMLBox_Box005
  Placement = pos=(5.01,8.41,5) rot=(0,0,1;0rad)
FEATURE [App::Link] Link_GDMLBox_Box005046
  CopyNumber = 64
  LinkPlacement = pos=(5.01,11.81,5) rot=(0,0,1;0rad)
  LinkedObject = -> GDMLBox_Box005
  Placement = pos=(5.01,11.81,5) rot=(0,0,1;0rad)
FEATURE [App::Link] Link_GDMLBox_Box005047
  CopyNumber = 65
  LinkPlacement = pos=(8.41,-11.99,5) rot=(0,0,1;0rad)
  LinkedObject = -> GDMLBox_Box005
  Placement = pos=(8.41,-11.99,5) rot=(0,0,1;0rad)
FEATURE [App::Link] Link_GDMLBox_Box005048
  CopyNumber = 66
  LinkPlacement = pos=(8.41,-8.59,5) rot=(0,0,1;0rad)
  LinkedObject = -> GDMLBox_Box005
  Placement = pos=(8.41,-8.59,5) rot=(0,0,1;0rad)
FEATURE [App::Link] Link_GDMLBox_Box005049
  CopyNumber = 67
  LinkPlacement = pos=(8.41,-5.19,5) rot=(0,0,1;0rad)
  LinkedObject = -> GDMLBox_Box005
  Placement = pos=(8.41,-5.19,5) rot=(0,0,1;0rad)
FEATURE [App::Link] Link_GDMLBox_Box005050
  CopyNumber = 68
  LinkPlacement = pos=(8.41,-1.79,5) rot=(0,0,1;0rad)
  LinkedObject = -> GDMLBox_Box005
  Placement = pos=(8.41,-1.79,5) rot=(0,0,1;0rad)
FEATURE [App::Link] Link_GDMLBox_Box005051
  CopyNumber = 69
  LinkPlacement = pos=(8.41,1.61,5) rot=(0,0,1;0rad)
  LinkedObject = -> GDMLBox_Box005
  Placement = pos=(8.41,1.61,5) rot=(0,0,1;0rad)
FEATURE [App::Link] Link_GDMLBox_Box005052
  CopyNumber = 70
  LinkPlacement = pos=(8.41,5.01,5) rot=(0,0,1;0rad)
  LinkedObject = -> GDMLBox_Box005
  Placement = pos=(8.41,5.01,5) rot=(0,0,1;0rad)
FEATURE [App::Link] Link_GDMLBox_Box005053
  CopyNumber = 71
  LinkPlacement = pos=(8.41,8.41,5) rot=(0,0,1;0rad)
  LinkedObject = -> GDMLBox_Box005
  Placement = pos=(8.41,8.41,5) rot=(0,0,1;0rad)
FEATURE [App::Link] Link_GDMLBox_Box005054
  CopyNumber = 72
  LinkPlacement = pos=(8.41,11.81,5) rot=(0,0,1;0rad)
  LinkedObject = -> GDMLBox_Box005
  Placement = pos=(8.41,11.81,5) rot=(0,0,1;0rad)
FEATURE [App::Link] Link_GDMLBox_Box005055
  CopyNumber = 73
  LinkPlacement = pos=(11.81,-11.99,5) rot=(0,0,1;0rad)
  LinkedObject = -> GDMLBox_Box005
  Placement = pos=(11.81,-11.99,5) rot=(0,0,1;0rad)
FEATURE [App::Link] Link_GDMLBox_Box005056
  CopyNumber = 74
  LinkPlacement = pos=(11.81,-8.59,5) rot=(0,0,1;0rad)
  LinkedObject = -> GDMLBox_Box005
  Placement = pos=(11.81,-8.59,5) rot=(0,0,1;0rad)
FEATURE [App::Link] Link_GDMLBox_Box005057
  CopyNumber = 75
  LinkPlacement = pos=(11.81,-5.19,5) rot=(0,0,1;0rad)
  LinkedObject = -> GDMLBox_Box005
  Placement = pos=(11.81,-5.19,5) rot=(0,0,1;0rad)
FEATURE [App::Link] Link_GDMLBox_Box005058
  CopyNumber = 76
  LinkPlacement = pos=(11.81,-1.79,5) rot=(0,0,1;0rad)
  LinkedObject = -> GDMLBox_Box005
  Placement = pos=(11.81,-1.79,5) rot=(0,0,1;0rad)
FEATURE [App::Link] Link_GDMLBox_Box005059
  CopyNumber = 77
  LinkPlacement = pos=(11.81,1.61,5) rot=(0,0,1;0rad)
  LinkedObject = -> GDMLBox_Box005
  Placement = pos=(11.81,1.61,5) rot=(0,0,1;0rad)
FEATURE [App::Link] Link_GDMLBox_Box005060
  CopyNumber = 78
  LinkPlacement = pos=(11.81,5.01,5) rot=(0,0,1;0rad)
  LinkedObject = -> GDMLBox_Box005
  Placement = pos=(11.81,5.01,5) rot=(0,0,1;0rad)
FEATURE [App::Link] Link_GDMLBox_Box005061
  CopyNumber = 79
  LinkPlacement = pos=(11.81,8.41,5) rot=(0,0,1;0rad)
  LinkedObject = -> GDMLBox_Box005
  Placement = pos=(11.81,8.41,5) rot=(0,0,1;0rad)
FEATURE [App::Link] Link_GDMLBox_Box005062
  CopyNumber = 80
  LinkPlacement = pos=(11.81,11.81,5) rot=(0,0,1;0rad)
  LinkedObject = -> GDMLBox_Box005
  Placement = pos=(11.81,11.81,5) rot=(0,0,1;0rad)
FEATURE [App::Part] Child_Array  label="Child_Array001"
  CopyNumber = 9
  Group = -> [GDMLBox_Box005,Link_GDMLBox_Box005,Link_GDMLBox_Box005001,Link_GDMLBox_Box005002,Link_GDMLBox_Box005003,Link_GDMLBox_Box005004,Link_GDMLBox_Box005005,Link_GDMLBox_Box005006,Link_GDMLBox_Box005007,Link_GDMLBox_Box005008,Link_GDMLBox_Box005009,Link_GDMLBox_Box005010,Link_GDMLBox_Box005011,Link_GDMLBox_Box005012,Link_GDMLBox_Box005013,Link_GDMLBox_Box005014,Link_GDMLBox_Box005015,+47 more]
  Origin = -> Origin007
  Placement = pos=(0,0,37.85) rot=(0,0,1;0rad)
FEATURE [App::Part] Parent_Array  label="Parent_Array001"
  Group = -> [Child_Array,Link_Child_Array,Link_Child_Array001,Link_Child_Array002,Link_Child_Array003,Link_Child_Array004,Link_Child_Array005,Link_Child_Array006]
  Origin = -> Origin006
FEATURE [App::Part] Part
  Group = -> [Parent_Array]
  Origin = -> Origin003
FEATURE [App::Part] worldVOL
  Group = -> [GDMLBox_WorldBox,Part001,Part,LV_Sphere]
  Origin = -> Origin
FEATURE [App::FeaturePython] ScintWrap1  # WARN: FeaturePython — macro-defined, semantics opaque (R4)
  CheckCommonFaces = true
  PV1 = -> Part001
  PV2 = -> LV_Sphere
  Surface = ScintWrap
